FCSTD DOCUMENT  (FreeCAD 0.20R29410 (Git))
Label: trafficModuleV3-1
License: All rights reserved
LicenseURL: http://en.wikipedia.org/wiki/All_rights_reserved
objects: Part::Feature×180, Sketcher::SketchObject×122, Part::Extrusion×62, Part::MultiFuse×53, Part::MultiCommon×31, Part::Loft×30, Part::Cylinder×26, Part::Cut×23, Part::Fillet×23, App::Part×13, Part::Box×11, Part::Compound2×2, Part::Cone×1
note: 562 computed .brp shape members not serialized (recipe doc carries the construction recipe); baked Part::Feature solids carry a one-line shape summary decoded from their .brp

FEATURE [Sketcher::SketchObject] Sketch014
  FullyConstrained = true
  sketch-geometry (4):
    g0: LineSegment StartX=0 StartY=275 StartZ=0 EndX=275 EndY=275 EndZ=0
    g1: LineSegment StartX=275 StartY=275 StartZ=0 EndX=275 EndY=0 EndZ=0
    g2: LineSegment StartX=275 StartY=0 StartZ=0 EndX=0 EndY=0 EndZ=0
    g3: LineSegment StartX=0 StartY=0 StartZ=0 EndX=0 EndY=275 EndZ=0
  constraints (11):
    c: Coincident(g0,g1)
    c: Coincident(g1,g2)
    c: Coincident(g2,g3)
    c: Coincident(g3,g0)
    c: Horizontal(g0)
    c: Horizontal(g2)
    c: Vertical(g1)
    c: Vertical(g3)
    c: Coincident(g2,g-1)
    c: DistanceX(g2,g2) = 275
    c: DistanceY(g3,g3) = 275
FEATURE [Sketcher::SketchObject] Sketch015
  FullyConstrained = true
  Placement = pos=(0,0,175.1) rot=(0,0,1;0rad)
  sketch-geometry (5):
    g0: GeomPoint X=137.5 Y=137.5 Z=0
    g1: LineSegment StartX=137.55 StartY=137.55 StartZ=0 EndX=137.55 EndY=137.45 EndZ=0
    g2: LineSegment StartX=137.55 StartY=137.45 StartZ=0 EndX=137.45 EndY=137.45 EndZ=0
    g3: LineSegment StartX=137.45 StartY=137.45 StartZ=0 EndX=137.45 EndY=137.55 EndZ=0
    g4: LineSegment StartX=137.45 StartY=137.55 StartZ=0 EndX=137.55 EndY=137.55 EndZ=0
  constraints (14):
    c: Coincident(g1,g2)
    c: Horizontal(g2)
    c: Vertical(g1)
    c: DistanceX(g2,g2) = 0.1
    c: DistanceX(g2,g0) = 0.05
    c: DistanceY(g1,g1) = 0.1
    c: DistanceY(g1,g0) = -0.05
    c: DistanceX(g0) = 137.5
    c: DistanceY(g0) = 137.5
    c: Coincident(g3,g2)
    c: Vertical(g3)
    c: Coincident(g4,g3)
    c: Coincident(g4,g1)
    c: Horizontal(g4)
FEATURE [Part::Loft] Loft  label="outerLayer"
  Closed = false
  MaxDegree = 5
  Ruled = false
  Sections = -> [Sketch014,Sketch015]
  Solid = true
FEATURE [Part::Feature] Part__Feature025  label="CUI_VGS-35C-12"
  Placement = pos=(86,137.5,21.5) rot=(1,0,0;1.5708rad)
  shape: bbox 82.03 x 100 x 30.06 mm, 2215 faces, 10 solids (baked)
FEATURE [Part::Cylinder] Cylinder004 .. Cylinder009  x6 (patterned run collapsed; names and placements below)
  Angle = 360
  AttacherType = Attacher::AttachEngine3D
  FirstAngle = 0
  Height = 10
  Radius = 2
  SecondAngle = 0
FEATURE [Part::Cylinder] Cylinder010  label="Cylinder"
  Angle = 360
  AttacherType = Attacher::AttachEngine3D
  FirstAngle = 0
  Height = 10
  Radius = 2
  SecondAngle = 0
FEATURE [Part::Cylinder] Cylinder011 .. Cylinder018  x8 (patterned run collapsed; names and placements below)
  Angle = 360
  AttacherType = Attacher::AttachEngine3D
  FirstAngle = 0
  Height = 10
  Radius = 2
  SecondAngle = 0
FEATURE [Part::Feature] Part__Feature  label="MainBoard"
  shape: bbox 50 x 23 x 1.8 mm, 90 faces (baked)
FEATURE [Part::Feature] Part__Feature029  label="USB Type C Port (SMD Type)"
  Placement = pos=(-18.7,0.12,3.4) rot=(0.707107,-0.707107,0;3.14159rad)
  shape: bbox 7.901 x 8.941 x 4.201 mm, 394 faces, 24 solids (baked)
FEATURE [Part::Feature] Part__Feature030  label="LoRaSTM32Chip"
  Placement = pos=(8.97,0,1.8) rot=(0,0,1;0rad)
  shape: bbox 12 x 12 x 2.5 mm, 68 faces (baked)
FEATURE [Part::Feature] Part__Feature031  label="E10_433M_SMA122"
  Placement = pos=(13,-2.15,1.4) rot=(0,0,1;0rad)
  shape: bbox 11.33 x 1.55 x 1.55 mm, 34 faces (baked)
FEATURE [Part::Feature] Part__Feature032  label="E10_433M_SMA123"
  Placement = pos=(13,-2.15,1.4) rot=(0,0,1;0rad)
  shape: bbox 13.33 x 6.493 x 6.493 mm, 59 faces (baked)
FEATURE [Part::Feature] Part__Feature033  label="CP2012"
  Placement = pos=(-8.75,0.13,1.82) rot=(0,0,1;0rad)
  shape: bbox 4 x 4 x 0.7 mm, 6 faces (baked)
FEATURE [Part::Feature] Part__Feature034  label="u.Fl Antenna Connector - 523-A-1JB"
  Placement = pos=(24.2,5.8,1.8) rot=(0,0.707107,0.707107;3.14159rad)
  shape: bbox 3.1 x 3 x 1.25 mm, 82 faces, 5 solids (baked)
FEATURE [Part::Feature] Part__Feature035  label="Top Traces"
  shape: bbox 49.4 x 23 x 0.02 mm, 7906 faces, 207 solids (baked)
FEATURE [App::Part] LoRa_E5_Mini  label="LoRa-E5-Mini"
  Group = -> [Part__Feature,Part__Feature029,Part__Feature030,Part__Feature031,Part__Feature032,Part__Feature033,Part__Feature034,Part__Feature035,Cylinder004,Cylinder005,Cylinder006,Cylinder007,Cylinder008,Cylinder009,Cylinder010,Cylinder011,Cylinder012,Cylinder013,Cylinder014,Cylinder015,Cylinder016,Cylinder017,Cylinder018]
  Origin = -> Origin
  Placement = pos=(100,164,45) rot=(0,0,-1;4.71239rad)
FEATURE [Part::Feature] Part__Feature037  label="ips7100s"
  Placement = pos=(161.5,115,75) rot=(0,0,1;0rad)
  shape: bbox 48.08 x 13.98 x 44.07 mm, 1935 faces (baked)
FEATURE [Part::Cone] Cone
  Angle = 360
  AttacherType = Attacher::AttachEngine3D
  Height = 1.5
  Placement = pos=(0,0,25.5) rot=(0,0,1;0rad)
  Radius1 = 4
  Radius2 = 3.5
FEATURE [Part::Cylinder] Cylinder020
  Angle = 360
  AttacherType = Attacher::AttachEngine3D
  FirstAngle = 0
  Height = 22
  Placement = pos=(0,0,5) rot=(0,0,1;0rad)
  Radius = 3.2
  SecondAngle = 0
FEATURE [Part::Cylinder] Cylinder021
  Angle = 360
  AttacherType = Attacher::AttachEngine3D
  FirstAngle = 0
  Height = 2
  Placement = pos=(0,0,5) rot=(0,0,1;0rad)
  Radius = 3.55
  SecondAngle = 0
FEATURE [Part::Cylinder] Cylinder022
  Angle = 360
  AttacherType = Attacher::AttachEngine3D
  FirstAngle = 0
  Height = 1
  Placement = pos=(0,0,11) rot=(0,0,1;0rad)
  Radius = 3.55
  SecondAngle = 0
FEATURE [Part::Cylinder] Cylinder023
  Angle = 360
  AttacherType = Attacher::AttachEngine3D
  FirstAngle = 0
  Height = 8
  Placement = pos=(0,0,12) rot=(0,0,1;0rad)
  Radius = 3.25
  SecondAngle = 0
FEATURE [Part::Cylinder] Cylinder024
  Angle = 360
  AttacherType = Attacher::AttachEngine3D
  FirstAngle = 0
  Height = 5.5
  Placement = pos=(0,0,20) rot=(0,0,1;0rad)
  Radius = 4
  SecondAngle = 0
FEATURE [Part::Cylinder] Cylinder025
  Angle = 360
  AttacherType = Attacher::AttachEngine3D
  FirstAngle = 0
  Height = 2
  Placement = pos=(0,0,3) rot=(0,0,1;0rad)
  Radius = 1
  SecondAngle = 0
FEATURE [Part::MultiFuse] Fusion002
  Shapes = -> [Cone,Cylinder020,Cylinder021,Cylinder022,Cylinder023,Cylinder024]
FEATURE [Part::MultiFuse] Fusion055  label="mic"
  Placement = pos=(137.5,137.5,108.25) rot=(0,0,1;3.14159rad)
  Shapes = -> [Cylinder025,Fusion002]
FEATURE [Part::Feature] Part__Feature040  label="CeramicBody (1)"
  shape: bbox 1.8 x 1.23 x 1.23 mm, 10 faces (baked)
FEATURE [Part::Feature] Part__Feature126  label="scd30"
  Placement = pos=(137.5,170,95) rot=(1,0,0;3.14159rad)
  shape: bbox 35.11 x 7.027 x 23.02 mm, 2292 faces, 25 solids (baked)
FEATURE [Part::Feature] Part__Feature127  label="Board"
  shape: bbox 25.4 x 25.4 x 1.57 mm, 211 faces (baked)
FEATURE [Part::Feature] Part__Feature128  label="QFN24_4MM"
  Placement = pos=(12.1412,14.4526,1.57) rot=(0,0,1;3.92699rad)
  shape: bbox 5.657 x 5.657 x 0.9 mm, 172 faces (baked)
FEATURE [Part::Feature] Part__Feature129  label="Part 5"
  shape: bbox 0.48 x 0.6603 x 0.6 mm, 14 faces (baked)
FEATURE [Part::Feature] Part__Feature130  label="Part 6"
  shape: bbox 0.48 x 0.6603 x 0.6 mm, 14 faces (baked)
FEATURE [Part::Feature] Part__Feature131  label="Part 4"
  shape: bbox 0.48 x 0.6603 x 0.6 mm, 14 faces (baked)
FEATURE [Part::Feature] Part__Feature132  label="Part 3"
  shape: bbox 0.48 x 0.6603 x 0.6 mm, 14 faces (baked)
FEATURE [Part::Feature] Part__Feature133  label="Part 010"
  shape: bbox 0.48 x 0.6603 x 0.6 mm, 14 faces (baked)
FEATURE [Part::Feature] Part__Feature134  label="Part 011"
  shape: bbox 3 x 1.4 x 1 mm, 10 faces (baked)
FEATURE [Part::Feature] Part__Feature135  label="Pin1"
  shape: bbox 0.6224 x 1.252 x 1.252 mm, 37 faces (baked)
FEATURE [Part::Feature] Part__Feature136  label="Pin2"
  shape: bbox 0.6224 x 1.252 x 1.252 mm, 37 faces (baked)
FEATURE [Part::Feature] Part__Feature137  label="CeramicBody"
  shape: bbox 1.8 x 1.23 x 1.23 mm, 10 faces (baked)
FEATURE [Part::Feature] Part__Feature138  label="0603-NO (1)"
  Placement = pos=(23.241,6.223,1.57) rot=(0,0,1;0rad)
  shape: bbox 1.7 x 0.9 x 0.55 mm, 52 faces, 3 solids (baked)
FEATURE [Part::Feature] Part__Feature139  label="0603-NO (2)"
  Placement = pos=(13.3858,8.4328,1.57) rot=(0,0,1;0rad)
  shape: bbox 1.7 x 0.9 x 0.55 mm, 52 faces, 3 solids (baked)
FEATURE [Part::Feature] Part__Feature140  label="0603-NO (3)"
  Placement = pos=(1.905,18.923,1.57) rot=(0,0,1;3.14159rad)
  shape: bbox 1.7 x 0.9 x 0.55 mm, 52 faces, 3 solids (baked)
FEATURE [Part::Feature] Part__Feature141  label="Pin1 (1)"
  shape: bbox 0.6224 x 1.252 x 1.252 mm, 37 faces (baked)
FEATURE [Part::Feature] Part__Feature142  label="Pin2 (1)"
  shape: bbox 0.6224 x 1.252 x 1.252 mm, 37 faces (baked)
FEATURE [Part::Feature] Part__Feature143  label="Pin1 (2)"
  shape: bbox 0.6224 x 1.252 x 1.252 mm, 37 faces (baked)
FEATURE [Part::Feature] Part__Feature144  label="Pin2 (2)"
  shape: bbox 0.6224 x 1.252 x 1.252 mm, 37 faces (baked)
FEATURE [Part::Feature] Part__Feature145  label="CeramicBody (2)"
  shape: bbox 1.8 x 1.23 x 1.23 mm, 10 faces (baked)
FEATURE [Part::Feature] Part__Feature146  label="CHIPLED_0603_NOOUTLINE"
  Placement = pos=(23.368,8.509,1.57) rot=(0,0,1;1.5708rad)
  shape: bbox 1.616 x 0.8 x 0.4 mm, 133 faces (baked)
FEATURE [Part::Feature] Part__Feature147  label="CHIPLED_0603_NOOUTLINE (1)"
  Placement = pos=(1.905,16.764,1.57) rot=(0,0,-1;1.5708rad)
  shape: bbox 1.616 x 0.8 x 0.4 mm, 133 faces (baked)
FEATURE [Part::Feature] Part__Feature148  label="JST_SH4"
  Placement = pos=(22.86,12.7,1.57) rot=(0,0,1;1.5708rad)
  shape: bbox 4.95 x 6 x 2.96 mm, 229 faces, 7 solids (baked)
FEATURE [Part::Feature] Part__Feature149  label="JST_SH4 (1)"
  Placement = pos=(2.54,12.7,1.57) rot=(0,0,-1;1.5708rad)
  shape: bbox 4.95 x 6 x 2.96 mm, 229 faces, 7 solids (baked)
FEATURE [Part::Feature] Part__Feature150  label="NEO3535_REVERSE"
  Placement = pos=(12.7,23.114,0) rot=(0,1,0;3.14159rad)
  shape: bbox 5.88 x 2.8 x 1.78 mm, 41 faces, 5 solids (baked)
FEATURE [Part::Feature] Part__Feature151  label="RESPACK_4X0603"
  Placement = pos=(22.86,18.415,1.57) rot=(0,0,1;3.14159rad)
  shape: bbox 3.2 x 1.6 x 0.61 mm, 172 faces (baked)
FEATURE [Part::Feature] Part__Feature152  label="SOT363"
  Placement = pos=(17.399,12.192,1.57) rot=(0,0,-1;1.5708rad)
  shape: bbox 2.208 x 2.208 x 1.121 mm, 178 faces, 4 solids (baked)
FEATURE [Part::Feature] Part__Feature153  label="Printed Circuit Board001"
  shape: bbox 25.4 x 17.78 x 1.6 mm, 42 faces (baked)
FEATURE [Part::Feature] Part__Feature154  label="EAHC2835WD007"
  shape: bbox 3.513 x 2.813 x 0.7485 mm, 108 faces, 4 solids (baked)
FEATURE [Part::Feature] Part__Feature155  label="AS7341 v003"
  Placement = pos=(0,-0.339822,1.6) rot=(0,0,1;0rad)
  shape: bbox 2 x 3.1 x 1.1 mm, 267 faces, 26 solids (baked)
FEATURE [Part::Feature] Part__Feature156  label="CAPC-0805-T0.95-BN v004"
  Placement = pos=(-5.01759,-3.15294,1.6) rot=(0,0,1;0rad)
  shape: bbox 2.1 x 1.35 x 0.95 mm, 42 faces (baked)
FEATURE [Part::Feature] Part__Feature157  label="CAPC-0805-T0.95-BN v005"
  Placement = pos=(-5.48627,2.66154,1.6) rot=(0,0,-1;1.5708rad)
  shape: bbox 1.35 x 2.1 x 0.95 mm, 42 faces (baked)
FEATURE [Part::Feature] Part__Feature158  label="CAPC-0805-T0.95-BN v006"
  Placement = pos=(-3.43627,2.66154,1.6) rot=(0,0,-1;1.5708rad)
  shape: bbox 1.35 x 2.1 x 0.95 mm, 42 faces (baked)
FEATURE [Part::Feature] Part__Feature159  label="CAPC-0603-T0.9-BN v002"
  Placement = pos=(-1.69987,-3.28475,1.6) rot=(0,0,1;0rad)
  shape: bbox 1.7 x 0.9 x 0.9 mm, 42 faces (baked)
FEATURE [Part::Feature] Part__Feature160  label="BODY_MF06A001"
  Placement = pos=(0,0,0.762) rot=(0.57735,-0.57735,-0.57735;2.0944rad)
  shape: bbox 1.601 x 2.921 x 1.016 mm, 42 faces (baked)
FEATURE [Part::Feature] Part__Feature161  label="LEAD_MF06A006"
  Placement = pos=(-0.9652,-0.9525,0.1016) rot=(0.57735,-0.57735,-0.57735;2.0944rad)
  shape: bbox 0.6223 x 0.3749 x 0.8636 mm, 14 faces (baked)
FEATURE [Part::Feature] Part__Feature162  label="LEAD_MF06A007"
  Placement = pos=(-0.9652,0,0.1016) rot=(0.57735,-0.57735,-0.57735;2.0944rad)
  shape: bbox 0.6223 x 0.3749 x 0.8636 mm, 14 faces (baked)
FEATURE [Part::Feature] Part__Feature163  label="LEAD_MF06A008"
  Placement = pos=(-0.9652,0.9525,0.1016) rot=(0.57735,-0.57735,-0.57735;2.0944rad)
  shape: bbox 0.6223 x 0.3749 x 0.8636 mm, 14 faces (baked)
FEATURE [Part::Feature] Part__Feature164  label="LEAD_MF06A009"
  Placement = pos=(0.9652,-0.9525,0.1016) rot=(0.57735,0.57735,0.57735;2.0944rad)
  shape: bbox 0.6223 x 0.3749 x 0.8636 mm, 14 faces (baked)
FEATURE [Part::Feature] Part__Feature165  label="LEAD_MF06A010"
  Placement = pos=(0.9652,0,0.1016) rot=(0.57735,0.57735,0.57735;2.0944rad)
  shape: bbox 0.6223 x 0.3749 x 0.8636 mm, 14 faces (baked)
FEATURE [Part::Feature] Part__Feature166  label="LEAD_MF06A011"
  Placement = pos=(0.9652,0.9525,0.1016) rot=(0.57735,0.57735,0.57735;2.0944rad)
  shape: bbox 0.6223 x 0.3749 x 0.8636 mm, 14 faces (baked)
FEATURE [Part::Feature] Part__Feature167  label="SOT363 v003"
  Placement = pos=(4.97054,-0.645171,1.675) rot=(0,0,1;3.14159rad)
  shape: bbox 2.1 x 2 x 1.1 mm, 94 faces, 7 solids (baked)
FEATURE [Part::Feature] Part__Feature168  label="LED 0603 single color v002"
  Placement = pos=(-9.18406,3.72778,1.60762) rot=(0,0,1;1.5708rad)
  shape: bbox 1.961 x 0.7932 x 0.7145 mm, 63 faces, 5 solids (baked)
FEATURE [Part::Feature] Part__Feature169  label="RESC-0603 v003"
  Placement = pos=(4.83432,-3.67461,1.6) rot=(0,0,1;0rad)
  shape: bbox 1.7 x 0.9 x 0.55 mm, 52 faces, 3 solids (baked)
FEATURE [Part::Feature] Part__Feature170  label="RESC-0603 v004"
  Placement = pos=(-7.14949,3.61248,1.6) rot=(0,0,-1;1.5708rad)
  shape: bbox 0.9 x 1.7 x 0.55 mm, 52 faces, 3 solids (baked)
FEATURE [Part::Feature] Part__Feature171  label="YC164_RESPACK v002"
  Placement = pos=(2.99591,1.52916,1.6) rot=(0,0,1;0rad)
  shape: bbox 3.2 x 1.6 x 0.61 mm, 172 faces (baked)
FEATURE [Part::Feature] Part__Feature172  label="qwicc v004"
  Placement = pos=(-10.8364,0.0607456,1.65) rot=(0,0,-1;1.5708rad)
  shape: bbox 4.95 x 6 x 2.96 mm, 229 faces, 7 solids (baked)
FEATURE [Part::Feature] Part__Feature173  label="qwicc v005"
  Placement = pos=(10.8256,0.00556102,1.65) rot=(0,0,1;1.5708rad)
  shape: bbox 4.95 x 6 x 2.96 mm, 229 faces, 7 solids (baked)
FEATURE [App::Part] _603_NO  label="0603-NO"
  Group = -> [Part__Feature135,Part__Feature136,Part__Feature137]
  Origin = -> Origin012
  Placement = pos=(16.51,8.382,1.57) rot=(0,0,1;0rad)
FEATURE [App::Part] _6700497  label="36700497"
  Group = -> [Part__Feature129,Part__Feature130,Part__Feature131,Part__Feature132,Part__Feature133,Part__Feature134]
  Origin = -> Origin010
  Placement = pos=(0,0,0) rot=(0,0,1;3.14159rad)
FEATURE [App::Part] SOT23_5  label="SOT23-5"
  Group = -> [_6700497]
  Origin = -> Origin011
  Placement = pos=(2.54,6.985,1.57) rot=(0,0,1;3.14159rad)
FEATURE [App::Part] _805_NO  label="0805-NO"
  Group = -> [Part__Feature141,Part__Feature142,Part__Feature040]
  Origin = -> Origin013
  Placement = pos=(7.874,13.589,1.57) rot=(0,0,1;1.5708rad)
FEATURE [App::Part] _805_NO__1_  label="0805-NO (1)"
  Group = -> [Part__Feature143,Part__Feature144,Part__Feature145]
  Origin = -> Origin014
  Placement = pos=(12.827,6.223,1.57) rot=(0,0,1;3.14159rad)
FEATURE [App::Part] Packages
  Group = -> [Part__Feature128,SOT23_5,_603_NO,Part__Feature138,Part__Feature139,Part__Feature140,_805_NO,_805_NO__1_,Part__Feature146,Part__Feature147,Part__Feature148,Part__Feature149,Part__Feature150,Part__Feature151,Part__Feature152]
  Origin = -> Origin015
FEATURE [App::Part] Adafruit_I2C_QT_Rotary_Encoder_v2  label="gps"
  Group = -> [Part__Feature127,Packages]
  Origin = -> Origin016
  Placement = pos=(167.5,167.5,74) rot=(0,0,1;0rad)
FEATURE [App::Part] sot_23_6_v003  label="sot-23-6 v003"
  Group = -> [Part__Feature160,Part__Feature161,Part__Feature162,Part__Feature163,Part__Feature164,Part__Feature165,Part__Feature166]
  Origin = -> Origin017
  Placement = pos=(-4.47945,-0.603742,1.69152) rot=(0,0,1;0rad)
FEATURE [App::Part] Adafruit_AS7341_STEMMA_QT_v003  label="bme280"
  Group = -> [Part__Feature153,Part__Feature154,Part__Feature155,Part__Feature156,Part__Feature157,Part__Feature158,Part__Feature159,sot_23_6_v003,Part__Feature167,Part__Feature168,Part__Feature169,Part__Feature170,Part__Feature171,Part__Feature172,Part__Feature173]
  Origin = -> Origin018
  Placement = pos=(170.5,137.5,95) rot=(-0.707107,0,-0.707107;3.14159rad)
FEATURE [Part::Feature] Part__Feature174  label="Printed Circuit Board002"
  shape: bbox 25.4 x 17.78 x 1.6 mm, 42 faces (baked)
FEATURE [Part::Feature] Part__Feature175  label="EAHC2835WD008"
  shape: bbox 3.513 x 2.813 x 0.7485 mm, 108 faces, 4 solids (baked)
FEATURE [Part::Feature] Part__Feature176  label="AS7341 v004"
  Placement = pos=(0,-0.339822,1.6) rot=(0,0,1;0rad)
  shape: bbox 2 x 3.1 x 1.1 mm, 267 faces, 26 solids (baked)
FEATURE [Part::Feature] Part__Feature177  label="CAPC-0805-T0.95-BN v007"
  Placement = pos=(-5.01759,-3.15294,1.6) rot=(0,0,1;0rad)
  shape: bbox 2.1 x 1.35 x 0.95 mm, 42 faces (baked)
FEATURE [Part::Feature] Part__Feature178  label="CAPC-0805-T0.95-BN v008"
  Placement = pos=(-5.48627,2.66154,1.6) rot=(0,0,-1;1.5708rad)
  shape: bbox 1.35 x 2.1 x 0.95 mm, 42 faces (baked)
FEATURE [Part::Feature] Part__Feature179  label="CAPC-0805-T0.95-BN v009"
  Placement = pos=(-3.43627,2.66154,1.6) rot=(0,0,-1;1.5708rad)
  shape: bbox 1.35 x 2.1 x 0.95 mm, 42 faces (baked)
FEATURE [Part::Feature] Part__Feature180  label="CAPC-0603-T0.9-BN v003"
  Placement = pos=(-1.69987,-3.28475,1.6) rot=(0,0,1;0rad)
  shape: bbox 1.7 x 0.9 x 0.9 mm, 42 faces (baked)
FEATURE [Part::Feature] Part__Feature181  label="BODY_MF06A002"
  Placement = pos=(0,0,0.762) rot=(0.57735,-0.57735,-0.57735;2.0944rad)
  shape: bbox 1.601 x 2.921 x 1.016 mm, 42 faces (baked)
FEATURE [Part::Feature] Part__Feature182  label="LEAD_MF06A012"
  Placement = pos=(-0.9652,-0.9525,0.1016) rot=(0.57735,-0.57735,-0.57735;2.0944rad)
  shape: bbox 0.6223 x 0.3749 x 0.8636 mm, 14 faces (baked)
FEATURE [Part::Feature] Part__Feature183  label="LEAD_MF06A013"
  Placement = pos=(-0.9652,0,0.1016) rot=(0.57735,-0.57735,-0.57735;2.0944rad)
  shape: bbox 0.6223 x 0.3749 x 0.8636 mm, 14 faces (baked)
FEATURE [Part::Feature] Part__Feature184  label="LEAD_MF06A014"
  Placement = pos=(-0.9652,0.9525,0.1016) rot=(0.57735,-0.57735,-0.57735;2.0944rad)
  shape: bbox 0.6223 x 0.3749 x 0.8636 mm, 14 faces (baked)
FEATURE [Part::Feature] Part__Feature185  label="LEAD_MF06A015"
  Placement = pos=(0.9652,-0.9525,0.1016) rot=(0.57735,0.57735,0.57735;2.0944rad)
  shape: bbox 0.6223 x 0.3749 x 0.8636 mm, 14 faces (baked)
FEATURE [Part::Feature] Part__Feature186  label="LEAD_MF06A016"
  Placement = pos=(0.9652,0,0.1016) rot=(0.57735,0.57735,0.57735;2.0944rad)
  shape: bbox 0.6223 x 0.3749 x 0.8636 mm, 14 faces (baked)
FEATURE [Part::Feature] Part__Feature187  label="LEAD_MF06A017"
  Placement = pos=(0.9652,0.9525,0.1016) rot=(0.57735,0.57735,0.57735;2.0944rad)
  shape: bbox 0.6223 x 0.3749 x 0.8636 mm, 14 faces (baked)
FEATURE [Part::Feature] Part__Feature188  label="SOT363 v004"
  Placement = pos=(4.97054,-0.645171,1.675) rot=(0,0,1;3.14159rad)
  shape: bbox 2.1 x 2 x 1.1 mm, 94 faces, 7 solids (baked)
FEATURE [Part::Feature] Part__Feature189  label="LED 0603 single color v003"
  Placement = pos=(-9.18406,3.72778,1.60762) rot=(0,0,1;1.5708rad)
  shape: bbox 1.961 x 0.7932 x 0.7145 mm, 63 faces, 5 solids (baked)
FEATURE [Part::Feature] Part__Feature190  label="RESC-0603 v005"
  Placement = pos=(4.83432,-3.67461,1.6) rot=(0,0,1;0rad)
  shape: bbox 1.7 x 0.9 x 0.55 mm, 52 faces, 3 solids (baked)
FEATURE [Part::Feature] Part__Feature191  label="RESC-0603 v006"
  Placement = pos=(-7.14949,3.61248,1.6) rot=(0,0,-1;1.5708rad)
  shape: bbox 0.9 x 1.7 x 0.55 mm, 52 faces, 3 solids (baked)
FEATURE [Part::Feature] Part__Feature192  label="YC164_RESPACK v003"
  Placement = pos=(2.99591,1.52916,1.6) rot=(0,0,1;0rad)
  shape: bbox 3.2 x 1.6 x 0.61 mm, 172 faces (baked)
FEATURE [Part::Feature] Part__Feature193  label="qwicc v006"
  Placement = pos=(-10.8364,0.0607456,1.65) rot=(0,0,-1;1.5708rad)
  shape: bbox 4.95 x 6 x 2.96 mm, 229 faces, 7 solids (baked)
FEATURE [Part::Feature] Part__Feature194  label="qwicc v007"
  Placement = pos=(10.8256,0.00556102,1.65) rot=(0,0,1;1.5708rad)
  shape: bbox 4.95 x 6 x 2.96 mm, 229 faces, 7 solids (baked)
FEATURE [App::Part] sot_23_6_v004  label="sot-23-6 v004"
  Group = -> [Part__Feature181,Part__Feature182,Part__Feature183,Part__Feature184,Part__Feature185,Part__Feature186,Part__Feature187]
  Origin = -> Origin019
  Placement = pos=(-4.47945,-0.603742,1.69152) rot=(0,0,1;0rad)
FEATURE [App::Part] Adafruit_AS7341_STEMMA_QT_v004  label="bme281"
  Group = -> [Part__Feature174,Part__Feature175,Part__Feature176,Part__Feature177,Part__Feature178,Part__Feature179,Part__Feature180,sot_23_6_v004,Part__Feature188,Part__Feature189,Part__Feature190,Part__Feature191,Part__Feature192,Part__Feature193,Part__Feature194]
  Origin = -> Origin020
  Placement = pos=(104.5,137.5,95) rot=(0,1,0;4.71239rad)
FEATURE [Sketcher::SketchObject] Sketch016
  FullyConstrained = true
  sketch-geometry (4):
    g0: LineSegment StartX=0 StartY=275 StartZ=0 EndX=275 EndY=275 EndZ=0
    g1: LineSegment StartX=275 StartY=275 StartZ=0 EndX=275 EndY=0 EndZ=0
    g2: LineSegment StartX=275 StartY=0 StartZ=0 EndX=0 EndY=0 EndZ=0
    g3: LineSegment StartX=0 StartY=0 StartZ=0 EndX=0 EndY=275 EndZ=0
  constraints (11):
    c: Coincident(g0,g1)
    c: Coincident(g1,g2)
    c: Coincident(g2,g3)
    c: Coincident(g3,g0)
    c: Horizontal(g0)
    c: Horizontal(g2)
    c: Vertical(g1)
    c: Vertical(g3)
    c: Coincident(g2,g-1)
    c: DistanceX(g2,g2) = 275
    c: DistanceY(g3,g3) = 275
FEATURE [Sketcher::SketchObject] Sketch017
  FullyConstrained = true
  Placement = pos=(0,0,175.1) rot=(0,0,1;0rad)
  sketch-geometry (5):
    g0: GeomPoint X=137.5 Y=137.5 Z=0
    g1: LineSegment StartX=137.55 StartY=137.55 StartZ=0 EndX=137.55 EndY=137.45 EndZ=0
    g2: LineSegment StartX=137.55 StartY=137.45 StartZ=0 EndX=137.45 EndY=137.45 EndZ=0
    g3: LineSegment StartX=137.45 StartY=137.45 StartZ=0 EndX=137.45 EndY=137.55 EndZ=0
    g4: LineSegment StartX=137.45 StartY=137.55 StartZ=0 EndX=137.55 EndY=137.55 EndZ=0
  constraints (14):
    c: Coincident(g1,g2)
    c: Horizontal(g2)
    c: Vertical(g1)
    c: DistanceX(g2,g2) = 0.1
    c: DistanceX(g2,g0) = 0.05
    c: DistanceY(g1,g1) = 0.1
    c: DistanceY(g1,g0) = -0.05
    c: DistanceX(g0) = 137.5
    c: DistanceY(g0) = 137.5
    c: Coincident(g3,g2)
    c: Vertical(g3)
    c: Coincident(g4,g3)
    c: Coincident(g4,g1)
    c: Horizontal(g4)
FEATURE [Part::Loft] Loft001  label="outerLayer001"
  Closed = false
  MaxDegree = 5
  Ruled = false
  Sections = -> [Sketch016,Sketch017]
  Solid = true
FEATURE [Sketcher::SketchObject] Sketch018
  FullyConstrained = true
  sketch-geometry (4):
    g0: LineSegment StartX=0 StartY=275 StartZ=0 EndX=275 EndY=275 EndZ=0
    g1: LineSegment StartX=275 StartY=275 StartZ=0 EndX=275 EndY=0 EndZ=0
    g2: LineSegment StartX=275 StartY=0 StartZ=0 EndX=0 EndY=0 EndZ=0
    g3: LineSegment StartX=0 StartY=0 StartZ=0 EndX=0 EndY=275 EndZ=0
  constraints (11):
    c: Coincident(g0,g1)
    c: Coincident(g1,g2)
    c: Coincident(g2,g3)
    c: Coincident(g3,g0)
    c: Horizontal(g0)
    c: Horizontal(g2)
    c: Vertical(g1)
    c: Vertical(g3)
    c: Coincident(g2,g-1)
    c: DistanceX(g2,g2) = 275
    c: DistanceY(g3,g3) = 275
FEATURE [Sketcher::SketchObject] Sketch019
  FullyConstrained = true
  Placement = pos=(0,0,175.1) rot=(0,0,1;0rad)
  sketch-geometry (5):
    g0: GeomPoint X=137.5 Y=137.5 Z=0
    g1: LineSegment StartX=137.55 StartY=137.55 StartZ=0 EndX=137.55 EndY=137.45 EndZ=0
    g2: LineSegment StartX=137.55 StartY=137.45 StartZ=0 EndX=137.45 EndY=137.45 EndZ=0
    g3: LineSegment StartX=137.45 StartY=137.45 StartZ=0 EndX=137.45 EndY=137.55 EndZ=0
    g4: LineSegment StartX=137.45 StartY=137.55 StartZ=0 EndX=137.55 EndY=137.55 EndZ=0
  constraints (14):
    c: Coincident(g1,g2)
    c: Horizontal(g2)
    c: Vertical(g1)
    c: DistanceX(g2,g2) = 0.1
    c: DistanceX(g2,g0) = 0.05
    c: DistanceY(g1,g1) = 0.1
    c: DistanceY(g1,g0) = -0.05
    c: DistanceX(g0) = 137.5
    c: DistanceY(g0) = 137.5
    c: Coincident(g3,g2)
    c: Vertical(g3)
    c: Coincident(g4,g3)
    c: Coincident(g4,g1)
    c: Horizontal(g4)
FEATURE [Part::Loft] Loft002  label="outerLayer002"
  Closed = false
  MaxDegree = 5
  Placement = pos=(0,0,-8) rot=(0,0,1;0rad)
  Ruled = false
  Sections = -> [Sketch018,Sketch019]
  Solid = true
FEATURE [Part::Cut] Cut  label="Shell-Ref"
  Base = -> Loft001
  Tool = -> Loft002
FEATURE [Sketcher::SketchObject] Sketch020
  FullyConstrained = true
  sketch-geometry (4):
    g0: LineSegment StartX=0 StartY=275 StartZ=0 EndX=275 EndY=275 EndZ=0
    g1: LineSegment StartX=275 StartY=275 StartZ=0 EndX=275 EndY=0 EndZ=0
    g2: LineSegment StartX=275 StartY=0 StartZ=0 EndX=0 EndY=0 EndZ=0
    g3: LineSegment StartX=0 StartY=0 StartZ=0 EndX=0 EndY=275 EndZ=0
  constraints (11):
    c: Coincident(g0,g1)
    c: Coincident(g1,g2)
    c: Coincident(g2,g3)
    c: Coincident(g3,g0)
    c: Horizontal(g0)
    c: Horizontal(g2)
    c: Vertical(g1)
    c: Vertical(g3)
    c: Coincident(g2,g-1)
    c: DistanceX(g2,g2) = 275
    c: DistanceY(g3,g3) = 275
FEATURE [Part::Extrusion] Extrude  label="level01s"
  Base = -> Sketch020
  Dir = (0,0,1)
  DirMode = 2
  FaceMakerClass = Part::FaceMakerBullseye
  LengthFwd = 10
  LengthRev = 0
  Placement = pos=(0,0,64) rot=(0,0,1;0rad)
  Solid = true
  Symmetric = false
FEATURE [Sketcher::SketchObject] Sketch021
  FullyConstrained = true
  sketch-geometry (4):
    g0: LineSegment StartX=0 StartY=275 StartZ=0 EndX=275 EndY=275 EndZ=0
    g1: LineSegment StartX=275 StartY=275 StartZ=0 EndX=275 EndY=0 EndZ=0
    g2: LineSegment StartX=275 StartY=0 StartZ=0 EndX=0 EndY=0 EndZ=0
    g3: LineSegment StartX=0 StartY=0 StartZ=0 EndX=0 EndY=275 EndZ=0
  constraints (11):
    c: Coincident(g0,g1)
    c: Coincident(g1,g2)
    c: Coincident(g2,g3)
    c: Coincident(g3,g0)
    c: Horizontal(g0)
    c: Horizontal(g2)
    c: Vertical(g1)
    c: Vertical(g3)
    c: Coincident(g2,g-1)
    c: DistanceX(g2,g2) = 275
    c: DistanceY(g3,g3) = 275
FEATURE [Sketcher::SketchObject] Sketch022
  FullyConstrained = true
  Placement = pos=(0,0,175.1) rot=(0,0,1;0rad)
  sketch-geometry (5):
    g0: GeomPoint X=137.5 Y=137.5 Z=0
    g1: LineSegment StartX=137.55 StartY=137.55 StartZ=0 EndX=137.55 EndY=137.45 EndZ=0
    g2: LineSegment StartX=137.55 StartY=137.45 StartZ=0 EndX=137.45 EndY=137.45 EndZ=0
    g3: LineSegment StartX=137.45 StartY=137.45 StartZ=0 EndX=137.45 EndY=137.55 EndZ=0
    g4: LineSegment StartX=137.45 StartY=137.55 StartZ=0 EndX=137.55 EndY=137.55 EndZ=0
  constraints (14):
    c: Coincident(g1,g2)
    c: Horizontal(g2)
    c: Vertical(g1)
    c: DistanceX(g2,g2) = 0.1
    c: DistanceX(g2,g0) = 0.05
    c: DistanceY(g1,g1) = 0.1
    c: DistanceY(g1,g0) = -0.05
    c: DistanceX(g0) = 137.5
    c: DistanceY(g0) = 137.5
    c: Coincident(g3,g2)
    c: Vertical(g3)
    c: Coincident(g4,g3)
    c: Coincident(g4,g1)
    c: Horizontal(g4)
FEATURE [Part::Loft] Loft003  label="outerLayer003"
  Closed = false
  MaxDegree = 5
  Placement = pos=(0,0,-8.25) rot=(0,0,1;0rad)
  Ruled = false
  Sections = -> [Sketch021,Sketch022]
  Solid = true
FEATURE [Part::MultiCommon] Common  label="level1"
  Shapes = -> [Extrude,Loft003]
FEATURE [Sketcher::SketchObject] Sketch
  FullyConstrained = true
  sketch-geometry (5):
    g0: Circle CenterX=75 CenterY=200 CenterZ=0 NormalX=0 NormalY=0 NormalZ=1 AngleXU=0 Radius=7.5
    g1: Circle CenterX=125 CenterY=200 CenterZ=0 NormalX=0 NormalY=0 NormalZ=1 AngleXU=0 Radius=7.5
    g2: Circle CenterX=75 CenterY=75 CenterZ=0 NormalX=0 NormalY=0 NormalZ=1 AngleXU=0 Radius=7.5
    g3: Circle CenterX=200 CenterY=200 CenterZ=0 NormalX=0 NormalY=0 NormalZ=1 AngleXU=0 Radius=7.5
    g4: Circle CenterX=125 CenterY=75 CenterZ=0 NormalX=0 NormalY=0 NormalZ=1 AngleXU=0 Radius=7.5
  constraints (15):
    c: Equal(g0,g1)
    c: Equal(g0,g2)
    c: Diameter(g0) = 15
    c: DistanceX(g2) = 75
    c: DistanceY(g2) = 75
    c: DistanceX(g2,g0) = 0
    c: DistanceY(g0) = 200
    c: DistanceY(g1,g0) = 0
    c: DistanceX(g0,g1) = 50
    c: DistanceX(g3) = 200
    c: Horizontal(g3,g1)
    c: Equal(g3,g1)
    c: Equal(g1,g4)
    c: Horizontal(g4,g2)
    c: Vertical(g1,g4)
FEATURE [Part::Extrusion] Extrude001
  Base = -> Sketch
  Dir = (0,0,1)
  DirMode = 2
  FaceMakerClass = Part::FaceMakerBullseye
  LengthFwd = 63.75
  LengthRev = 0
  Solid = true
  Symmetric = false
FEATURE [Sketcher::SketchObject] Sketch023
  FullyConstrained = true
  sketch-geometry (4):
    g0: LineSegment StartX=0 StartY=275 StartZ=0 EndX=275 EndY=275 EndZ=0
    g1: LineSegment StartX=275 StartY=275 StartZ=0 EndX=275 EndY=0 EndZ=0
    g2: LineSegment StartX=275 StartY=0 StartZ=0 EndX=0 EndY=0 EndZ=0
    g3: LineSegment StartX=0 StartY=0 StartZ=0 EndX=0 EndY=275 EndZ=0
  constraints (11):
    c: Coincident(g0,g1)
    c: Coincident(g1,g2)
    c: Coincident(g2,g3)
    c: Coincident(g3,g0)
    c: Horizontal(g0)
    c: Horizontal(g2)
    c: Vertical(g1)
    c: Vertical(g3)
    c: Coincident(g2,g-1)
    c: DistanceX(g2,g2) = 275
    c: DistanceY(g3,g3) = 275
FEATURE [Sketcher::SketchObject] Sketch024
  FullyConstrained = true
  Placement = pos=(0,0,175.1) rot=(0,0,1;0rad)
  sketch-geometry (5):
    g0: GeomPoint X=137.5 Y=137.5 Z=0
    g1: LineSegment StartX=137.55 StartY=137.55 StartZ=0 EndX=137.55 EndY=137.45 EndZ=0
    g2: LineSegment StartX=137.55 StartY=137.45 StartZ=0 EndX=137.45 EndY=137.45 EndZ=0
    g3: LineSegment StartX=137.45 StartY=137.45 StartZ=0 EndX=137.45 EndY=137.55 EndZ=0
    g4: LineSegment StartX=137.45 StartY=137.55 StartZ=0 EndX=137.55 EndY=137.55 EndZ=0
  constraints (14):
    c: Coincident(g1,g2)
    c: Horizontal(g2)
    c: Vertical(g1)
    c: DistanceX(g2,g2) = 0.1
    c: DistanceX(g2,g0) = 0.05
    c: DistanceY(g1,g1) = 0.1
    c: DistanceY(g1,g0) = -0.05
    c: DistanceX(g0) = 137.5
    c: DistanceY(g0) = 137.5
    c: Coincident(g3,g2)
    c: Vertical(g3)
    c: Coincident(g4,g3)
    c: Coincident(g4,g1)
    c: Horizontal(g4)
FEATURE [Part::Loft] Loft004  label="outerLayer004"
  Closed = false
  MaxDegree = 5
  Placement = pos=(0,0,-8.25) rot=(0,0,1;0rad)
  Ruled = false
  Sections = -> [Sketch023,Sketch024]
  Solid = true
FEATURE [Sketcher::SketchObject] Sketch025
  FullyConstrained = true
  sketch-geometry (4):
    g0: LineSegment StartX=0 StartY=275 StartZ=0 EndX=275 EndY=275 EndZ=0
    g1: LineSegment StartX=275 StartY=275 StartZ=0 EndX=275 EndY=0 EndZ=0
    g2: LineSegment StartX=275 StartY=0 StartZ=0 EndX=0 EndY=0 EndZ=0
    g3: LineSegment StartX=0 StartY=0 StartZ=0 EndX=0 EndY=275 EndZ=0
  constraints (11):
    c: Coincident(g0,g1)
    c: Coincident(g1,g2)
    c: Coincident(g2,g3)
    c: Coincident(g3,g0)
    c: Horizontal(g0)
    c: Horizontal(g2)
    c: Vertical(g1)
    c: Vertical(g3)
    c: Coincident(g2,g-1)
    c: DistanceX(g2,g2) = 275
    c: DistanceY(g3,g3) = 275
FEATURE [Part::Extrusion] Extrude002  label="level01s001"
  Base = -> Sketch025
  Dir = (0,0,1)
  DirMode = 2
  FaceMakerClass = Part::FaceMakerBullseye
  LengthFwd = 5
  LengthRev = 0
  Solid = true
  Symmetric = false
FEATURE [Part::MultiCommon] Common001  label="BaseLevel"
  Shapes = -> [Loft004,Extrude002]
FEATURE [Part::MultiFuse] Fusion  label="level2"
  Shapes = -> [Extrude001,Common001]
FEATURE [Sketcher::SketchObject] Sketch026
  FullyConstrained = true
  Placement = pos=(0,0,0) rot=(1,0,0;1.5708rad)
  sketch-geometry (6):
    g0: LineSegment StartX=46 StartY=5 StartZ=0 EndX=40 EndY=5 EndZ=0
    g1: LineSegment StartX=40 StartY=5 StartZ=0 EndX=40 EndY=41.5 EndZ=0
    g2: LineSegment StartX=40 StartY=41.5 StartZ=0 EndX=115 EndY=41.5 EndZ=0
    g3: LineSegment StartX=115 StartY=41.5 StartZ=0 EndX=115 EndY=35.5 EndZ=0
    g4: LineSegment StartX=115 StartY=35.5 StartZ=0 EndX=46 EndY=35.5 EndZ=0
    g5: LineSegment StartX=46 StartY=35.5 StartZ=0 EndX=46 EndY=5 EndZ=0
  constraints (18):
    c: Horizontal(g0)
    c: Coincident(g1,g0)
    c: Vertical(g1)
    c: Coincident(g2,g1)
    c: Horizontal(g2)
    c: Coincident(g3,g2)
    c: Coincident(g4,g3)
    c: Horizontal(g4)
    c: Coincident(g5,g4)
    c: Coincident(g5,g0)
    c: Vertical(g5)
    c: Vertical(g3)
    c: DistanceY(g0) = 5
    c: DistanceY(g3,g3) = 6
    c: DistanceX(g0,g0) = 6
    c: DistanceX(g1) = 40
    c: DistanceX(g2) = 115
    c: DistanceY(g4) = 35.5
FEATURE [Part::Extrusion] Extrude003
  Base = -> Sketch026
  Dir = (0,-1,2e-16)
  DirMode = 2
  FaceMakerClass = Part::FaceMakerBullseye
  LengthFwd = 45
  LengthRev = 0
  Placement = pos=(0,190,0) rot=(0,0,1;0rad)
  Solid = true
  Symmetric = false
FEATURE [Part::MultiFuse] Fusion056  label="level2s"
  Shapes = -> [Fusion,Extrude003]
FEATURE [Sketcher::SketchObject] Sketch027
  FullyConstrained = true
  sketch-geometry (21):
    g0: Circle CenterX=51.75 CenterY=92.5 CenterZ=0 NormalX=0 NormalY=0 NormalZ=1 AngleXU=0 Radius=1.625
    g1: Circle CenterX=87.75 CenterY=108.5 CenterZ=0 NormalX=0 NormalY=0 NormalZ=1 AngleXU=0 Radius=1.625
    g2: Circle CenterX=121.75 CenterY=185.5 CenterZ=0 NormalX=0 NormalY=0 NormalZ=1 AngleXU=0 Radius=2
    g3: Circle CenterX=147.3 CenterY=147.75 CenterZ=0 NormalX=0 NormalY=0 NormalZ=1 AngleXU=0 Radius=1.625
    g4: Circle CenterX=218.8 CenterY=147.75 CenterZ=0 NormalX=0 NormalY=0 NormalZ=1 AngleXU=0 Radius=1.625
    g5: Circle CenterX=218.8 CenterY=219.25 CenterZ=0 NormalX=0 NormalY=0 NormalZ=1 AngleXU=0 Radius=1.625
    g6: Circle CenterX=147.3 CenterY=219.25 CenterZ=0 NormalX=0 NormalY=0 NormalZ=1 AngleXU=0 Radius=1.625
    g7: Circle CenterX=75 CenterY=200 CenterZ=0 NormalX=0 NormalY=0 NormalZ=1 AngleXU=0 Radius=2.8
    g8: Circle CenterX=125 CenterY=200 CenterZ=0 NormalX=0 NormalY=0 NormalZ=1 AngleXU=0 Radius=2.8
    g9: Circle CenterX=200 CenterY=75 CenterZ=0 NormalX=0 NormalY=0 NormalZ=1 AngleXU=0 Radius=2.8
    g10: Circle CenterX=75 CenterY=75 CenterZ=0 NormalX=0 NormalY=0 NormalZ=1 AngleXU=0 Radius=2.8
    g11: Circle CenterX=91 CenterY=186.5 CenterZ=0 NormalX=0 NormalY=0 NormalZ=1 AngleXU=0 Radius=1.65
    g12: Circle CenterX=109 CenterY=186.5 CenterZ=0 NormalX=0 NormalY=0 NormalZ=1 AngleXU=0 Radius=1.65
    g13: Circle CenterX=91 CenterY=151.5 CenterZ=0 NormalX=0 NormalY=0 NormalZ=1 AngleXU=0 Radius=1.65
    g14: Circle CenterX=109 CenterY=151.5 CenterZ=0 NormalX=0 NormalY=0 NormalZ=1 AngleXU=0 Radius=1.65
    g15: Circle CenterX=147.3 CenterY=128.25 CenterZ=0 NormalX=0 NormalY=0 NormalZ=1 AngleXU=0 Radius=1.625
    g16: Circle CenterX=218.8 CenterY=128.25 CenterZ=0 NormalX=0 NormalY=0 NormalZ=1 AngleXU=0 Radius=1.625
    g17: Circle CenterX=147.3 CenterY=56.75 CenterZ=0 NormalX=0 NormalY=0 NormalZ=1 AngleXU=0 Radius=1.625
    g18: Circle CenterX=218.8 CenterY=56.75 CenterZ=0 NormalX=0 NormalY=0 NormalZ=1 AngleXU=0 Radius=1.625
    g19: Circle CenterX=125 CenterY=75 CenterZ=0 NormalX=0 NormalY=0 NormalZ=1 AngleXU=0 Radius=2.8
    g20: Circle CenterX=200 CenterY=200 CenterZ=0 NormalX=0 NormalY=0 NormalZ=1 AngleXU=0 Radius=2.8
  constraints (60):
    c: Equal(g0,g1)
    c: Equal(g0, g3-g6) x4
    c: Diameter(g0) = 3.25
    c: DistanceX(g0) = 51.75
    c: DistanceY(g0) = 92.5
    c: DistanceY(g0,g1) = 16
    c: DistanceX(g0,g1) = 36
    c: DistanceY(g1,g2) = 77
    c: DistanceX(g1,g2) = 34
    c: Diameter(g2) = 4
    c: DistanceY(g3) = 147.75
    c: DistanceX(g3) = 147.3
    c: DistanceX(g3,g4) = 71.5
    c: DistanceY(g4,g3) = 0
    c: DistanceX(g3,g6) = 0
    c: DistanceY(g3,g6) = 71.5
    c: DistanceY(g6,g5) = 0
    c: DistanceX(g4,g5) = 0
    c: DistanceY(g10) = 75
    c: DistanceY(g10,g9) = 0
    c: DistanceX(g10) = 75
    c: DistanceX(g10,g9) = 125
    c: DistanceY(g10,g7) = 125
    c: DistanceX(g7,g10) = 0
    c: DistanceX(g7,g8) = 50
    c: DistanceY(g8,g7) = 0
    c: Equal(g7,g8)
    c: Equal(g7,g10)
    c: Equal(g7,g9)
    c: Diameter(g7) = 5.6
    c: Equal(g11,g12)
    c: Equal(g11,g13)
    c: Equal(g11,g14)
    c: Diameter(g11) = 3.3
    c: DistanceY(g13) = 151.5
    c: DistanceX(g13) = 91
    c: DistanceY(g14,g13) = 0
    c: DistanceX(g13,g14) = 18
    c: DistanceY(g13,g11) = 35
    c: DistanceX(g13,g11) = 0
    c: DistanceY(g11,g12) = 0
    c: DistanceX(g12,g14) = 0
    c: Equal(g16,g15)
    c: Equal(g16,g17)
    c: Equal(g16,g18)
    c: Diameter(g16) = 3.25
    c: Vertical(g15,g17)
    c: Vertical(g17,g3)
    c: Vertical(g18,g16)
    c: Vertical(g16,g4)
    c: Horizontal(g15,g16)
    c: Horizontal(g18,g17)
    c: DistanceY(g15,g3) = 19.5
    c: DistanceY(g17,g15) = 71.5
    c: Horizontal(g19,g10)
    c: Vertical(g19,g8)
    c: Equal(g19,g10)
    c: Horizontal(g8,g20)
    c: Vertical(g9,g20)
    c: Equal(g20,g8)
FEATURE [Part::Extrusion] Extrude004
  Base = -> Sketch027
  Dir = (0,0,1)
  DirMode = 2
  FaceMakerClass = Part::FaceMakerBullseye
  LengthFwd = 80
  LengthRev = 0
  Solid = true
  Symmetric = false
FEATURE [Part::Cut] Cut001  label="level02"
  Base = -> Fusion056
  Tool = -> Extrude004
FEATURE [Sketcher::SketchObject] Sketch029
  FullyConstrained = true
  Placement = pos=(0,0,0) rot=(1,0,0;1.5708rad)
  sketch-geometry (8):
    g0: LineSegment StartX=105 StartY=74 StartZ=0 EndX=111 EndY=74 EndZ=0
    g1: LineSegment StartX=164 StartY=115.5 StartZ=0 EndX=164 EndY=74 EndZ=0
    g2: LineSegment StartX=164 StartY=74 StartZ=0 EndX=170 EndY=74 EndZ=0
    g3: LineSegment StartX=170 StartY=74 StartZ=0 EndX=170 EndY=119 EndZ=0
    g4: LineSegment StartX=170 StartY=119 StartZ=0 EndX=105 EndY=119 EndZ=0
    g5: LineSegment StartX=105 StartY=119 StartZ=0 EndX=105 EndY=74 EndZ=0
    g6: LineSegment StartX=111 StartY=74 StartZ=0 EndX=111 EndY=115.5 EndZ=0
    g7: LineSegment StartX=111 StartY=115.5 StartZ=0 EndX=164 EndY=115.5 EndZ=0
  constraints (24):
    c: Horizontal(g0)
    c: Vertical(g1)
    c: Horizontal(g2)
    c: Vertical(g3)
    c: Coincident(g4,g3)
    c: Horizontal(g4)
    c: Coincident(g5,g4)
    c: Coincident(g5,g0)
    c: Vertical(g5)
    c: Coincident(g1,g2)
    c: Coincident(g2,g3)
    c: DistanceY(g0,g1) = 0
    c: DistanceY(g0) = 74
    c: DistanceX(g0) = 105
    c: DistanceX(g1,g2) = 6
    c: DistanceX(g2) = 170
    c: Vertical(g6)
    c: Coincident(g7,g6)
    c: Horizontal(g7)
    c: Coincident(g1,g7)
    c: DistanceY(g1,g3) = 3.5
    c: DistanceX(g4,g6) = 6
    c: Coincident(g0,g6)
    c: DistanceY(g0,g6) = 41.5
FEATURE [Part::Extrusion] Extrude005
  Base = -> Sketch029
  Dir = (0,-1,-6e-16)
  DirMode = 2
  FaceMakerClass = Part::FaceMakerBullseye
  LengthFwd = 20
  LengthRev = 0
  Placement = pos=(0,127.5,0) rot=(0,0,1;0rad)
  Reversed = true
  Solid = true
  Symmetric = false
FEATURE [Sketcher::SketchObject] Sketch030
  FullyConstrained = true
  Placement = pos=(0,0,0) rot=(1,0,0;1.5708rad)
  sketch-geometry (10):
    g0: LineSegment StartX=112 StartY=84 StartZ=0 EndX=122 EndY=84 EndZ=0
    g1: LineSegment StartX=122 StartY=84 StartZ=0 EndX=122 EndY=74 EndZ=0
    g2: LineSegment StartX=122 StartY=74 StartZ=0 EndX=112 EndY=74 EndZ=0
    g3: LineSegment StartX=112 StartY=74 StartZ=0 EndX=112 EndY=84 EndZ=0
    g4: LineSegment StartX=153 StartY=120 StartZ=0 EndX=163 EndY=120 EndZ=0
    g5: LineSegment StartX=163 StartY=120 StartZ=0 EndX=163 EndY=74 EndZ=0
    g6: LineSegment StartX=163 StartY=74 StartZ=0 EndX=153 EndY=74 EndZ=0
    g7: LineSegment StartX=153 StartY=74 StartZ=0 EndX=153 EndY=120 EndZ=0
    g8: Circle CenterX=117.1 CenterY=78.6 CenterZ=0 NormalX=0 NormalY=0 NormalZ=1 AngleXU=0 Radius=1.6
    g9: Circle CenterX=157.85 CenterY=115.4 CenterZ=0 NormalX=0 NormalY=0 NormalZ=1 AngleXU=0 Radius=1.6
  constraints (30):
    c: Coincident(g0,g1)
    c: Coincident(g1,g2)
    c: Coincident(g2,g3)
    c: Coincident(g3,g0)
    c: Horizontal(g0)
    c: Horizontal(g2)
    c: Vertical(g1)
    c: Vertical(g3)
    c: Coincident(g4,g5)
    c: Coincident(g5,g6)
    c: Coincident(g6,g7)
    c: Coincident(g7,g4)
    c: Horizontal(g4)
    c: Horizontal(g6)
    c: Vertical(g5)
    c: Vertical(g7)
    c: DistanceX(g2) = 112
    c: DistanceY(g2,g0) = 10
    c: DistanceX(g2,g0) = 10
    c: DistanceY(g2) = 74
    c: DistanceY(g1,g6) = 0
    c: DistanceX(g1,g6) = 31
    c: DistanceX(g4,g4) = 10
    c: DistanceY(g6,g4) = 46
    c: Equal(g8,g9)
    c: Diameter(g8) = 3.2
    c: DistanceY(g2,g8) = 4.6
    c: DistanceX(g2,g8) = 5.1
    c: DistanceX(g8,g9) = 40.75
    c: DistanceY(g8,g9) = 36.8
FEATURE [Part::Extrusion] Extrude006
  Base = -> Sketch030
  Dir = (0,-1,-6e-16)
  DirMode = 2
  FaceMakerClass = Part::FaceMakerBullseye
  LengthFwd = 10
  LengthRev = 0
  Placement = pos=(0,115.25,0) rot=(0,0,1;0rad)
  Reversed = true
  Solid = true
  Symmetric = false
FEATURE [Sketcher::SketchObject] Sketch031
  FullyConstrained = true
  Placement = pos=(0,0,0) rot=(1,0,0;1.5708rad)
  sketch-geometry (10):
    g0: LineSegment StartX=118 StartY=109 StartZ=0 EndX=128 EndY=109 EndZ=0
    g1: LineSegment StartX=128 StartY=109 StartZ=0 EndX=128 EndY=74 EndZ=0
    g2: LineSegment StartX=128 StartY=74 StartZ=0 EndX=118 EndY=74 EndZ=0
    g3: LineSegment StartX=118 StartY=74 StartZ=0 EndX=118 EndY=109 EndZ=0
    g4: LineSegment StartX=150 StartY=92 StartZ=0 EndX=160 EndY=92 EndZ=0
    g5: LineSegment StartX=160 StartY=92 StartZ=0 EndX=160 EndY=74 EndZ=0
    g6: LineSegment StartX=160 StartY=74 StartZ=0 EndX=150 EndY=74 EndZ=0
    g7: LineSegment StartX=150 StartY=74 StartZ=0 EndX=150 EndY=92 EndZ=0
    g8: Circle CenterX=122.95 CenterY=104.43 CenterZ=0 NormalX=0 NormalY=0 NormalZ=1 AngleXU=0 Radius=1.6
    g9: Circle CenterX=154.95 CenterY=88.19 CenterZ=0 NormalX=0 NormalY=0 NormalZ=1 AngleXU=0 Radius=1.6
  constraints (30):
    c: Coincident(g0,g1)
    c: Coincident(g1,g2)
    c: Coincident(g2,g3)
    c: Coincident(g3,g0)
    c: Horizontal(g0)
    c: Horizontal(g2)
    c: Vertical(g1)
    c: Vertical(g3)
    c: Coincident(g4,g5)
    c: Coincident(g5,g6)
    c: Coincident(g6,g7)
    c: Coincident(g7,g4)
    c: Horizontal(g4)
    c: Horizontal(g6)
    c: Vertical(g5)
    c: Vertical(g7)
    c: DistanceY(g2) = 74
    c: DistanceY(g2,g0) = 35
    c: DistanceX(g2,g2) = 10
    c: DistanceX(g2) = 118
    c: DistanceX(g1,g6) = 22
    c: DistanceX(g4,g4) = 10
    c: DistanceY(g6,g4) = 18
    c: DistanceY(g1,g6) = 0
    c: DistanceX(g2,g8) = 4.95
    c: DistanceY(g2,g8) = 30.43
    c: DistanceX(g8,g9) = 32
    c: DistanceY(g9,g8) = 16.24
    c: Equal(g8,g9)
    c: Diameter(g8) = 3.2
FEATURE [Part::Extrusion] Extrude007
  Base = -> Sketch031
  Dir = (0,-1,-3e-16)
  DirMode = 2
  FaceMakerClass = Part::FaceMakerBullseye
  LengthFwd = 10
  LengthRev = 0
  Placement = pos=(0,162.5,0) rot=(0,0,1;0rad)
  Solid = true
  Symmetric = false
FEATURE [Part::MultiFuse] Fusion057  label="levell1s"
  Shapes = -> [Extrude005,Extrude006,Extrude007,Common]
FEATURE [Sketcher::SketchObject] Sketch032
  FullyConstrained = true
  MapMode = 2
  Support = -> [Fusion057]
  sketch-geometry (17):
    g0: ArcOfCircle CenterX=137.5 CenterY=137.5 CenterZ=0 NormalX=0 NormalY=0 NormalZ=1 AngleXU=0 Radius=3.2 StartAngle=3.14159 EndAngle=6.28319
    g1: LineSegment StartX=134.3 StartY=137.5 StartZ=0 EndX=134.3 EndY=147.5 EndZ=0
    g2: LineSegment StartX=134.3 StartY=147.5 StartZ=0 EndX=140.7 EndY=147.5 EndZ=0
    g3: LineSegment StartX=140.7 StartY=147.5 StartZ=0 EndX=140.7 EndY=137.5 EndZ=0
    g4: Circle CenterX=75 CenterY=75 CenterZ=0 NormalX=0 NormalY=0 NormalZ=1 AngleXU=0 Radius=2.125
    g5: Circle CenterX=200 CenterY=75 CenterZ=0 NormalX=0 NormalY=0 NormalZ=1 AngleXU=0 Radius=2.125
    g6: Circle CenterX=75 CenterY=200 CenterZ=0 NormalX=0 NormalY=0 NormalZ=1 AngleXU=0 Radius=2.125
    g7: Circle CenterX=125 CenterY=200 CenterZ=0 NormalX=0 NormalY=0 NormalZ=1 AngleXU=0 Radius=2.125
    g8: Circle CenterX=200 CenterY=200 CenterZ=0 NormalX=0 NormalY=0 NormalZ=1 AngleXU=0 Radius=2.125
    g9: Circle CenterX=170.05 CenterY=190.35 CenterZ=0 NormalX=0 NormalY=0 NormalZ=1 AngleXU=0 Radius=1.6
    g10: Circle CenterX=190.35 CenterY=190.35 CenterZ=0 NormalX=0 NormalY=0 NormalZ=1 AngleXU=0 Radius=1.6
    g11: Circle CenterX=190.4 CenterY=170.05 CenterZ=0 NormalX=0 NormalY=0 NormalZ=1 AngleXU=0 Radius=1.6
    g12: Circle CenterX=170.05 CenterY=170.05 CenterZ=0 NormalX=0 NormalY=0 NormalZ=1 AngleXU=0 Radius=1.6
    g13: Circle CenterX=137.5 CenterY=85 CenterZ=0 NormalX=0 NormalY=0 NormalZ=1 AngleXU=0 Radius=2
    g14: Circle CenterX=85 CenterY=137.5 CenterZ=0 NormalX=0 NormalY=0 NormalZ=1 AngleXU=0 Radius=2
    g15: Circle CenterX=190 CenterY=137.5 CenterZ=0 NormalX=0 NormalY=0 NormalZ=1 AngleXU=0 Radius=2
    g16: Circle CenterX=137.5 CenterY=190 CenterZ=0 NormalX=0 NormalY=0 NormalZ=1 AngleXU=0 Radius=2
  constraints (50):
    c: Coincident(g1,g0)
    c: Vertical(g1)
    c: Coincident(g2,g1)
    c: Horizontal(g2)
    c: Coincident(g3,g2)
    c: Coincident(g3,g0)
    c: Vertical(g3)
    c: DistanceX(g0,g0) = 6.4
    c: Diameter(g0) = 6.4
    c: DistanceY(g0,g0) = 0
    c: DistanceX(g0) = 137.5
    c: DistanceY(g0) = 137.5
    c: DistanceY(g0,g1) = 10
    c: DistanceX(g4) = 75
    c: DistanceY(g4) = 75
    c: DistanceX(g4,g5) = 125
    c: DistanceX(g4,g6) = 0
    c: DistanceY(g4,g6) = 125
    c: DistanceY(g7,g6) = 0
    c: DistanceY(g7,g8) = 0
    c: DistanceX(g8,g5) = 0
    c: Equal(g5,g4)
    c: Equal(g5,g6)
    c: Equal(g5,g7)
    c: Equal(g5,g8)
    c: Diameter(g5) = 4.25
    c: DistanceX(g6,g7) = 50
    c: DistanceY(g5,g4) = 0
    c: DistanceX(g10,g8) = 9.65
    c: DistanceY(g11,g10) = 20.3
    c: DistanceY(g10,g8) = 9.65
    c: Equal(g9,g10)
    c: Equal(g9,g11)
    c: Equal(g9,g12)
    c: Diameter(g9) = 3.2
    c: DistanceX(g12,g11) = 20.35
    c: DistanceY(g12,g9) = 20.3
    c: DistanceX(g9,g10) = 20.3
    c: DistanceY(g12,g11) = 0
    c: DistanceX(g12,g9) = 0
    c: Equal(g14,g13)
    c: Equal(g14,g15)
    c: Equal(g14,g16)
    c: Diameter(g14) = 4
    c: DistanceX(g14) = 85
    c: Horizontal(g14,g0)
    c: Symmetric(g14,g15,g0)
    c: Vertical(g16,g13)
    c: Symmetric(g13,g16,g0)
    c: DistanceY(g13,g0) = 52.5
FEATURE [Part::Extrusion] Extrude008
  Base = -> Sketch032
  Dir = (0,0,1)
  DirMode = 2
  FaceMakerClass = Part::FaceMakerBullseye
  LengthFwd = 60
  LengthRev = 0
  Placement = pos=(0,0,64) rot=(0,0,1;0rad)
  Solid = true
  Symmetric = false
FEATURE [Part::Cut] Cut002
  Base = -> Fusion057
  Tool = -> Extrude008
FEATURE [Sketcher::SketchObject] Sketch033
  FullyConstrained = true
  MapMode = 4
  Placement = pos=(0,0,0) rot=(0.57735,0.57735,0.57735;2.0944rad)
  Support = -> [Cut002]
  sketch-geometry (4):
    g0: Circle CenterX=131.15 CenterY=84.85 CenterZ=0 NormalX=0 NormalY=0 NormalZ=1 AngleXU=0 Radius=1.6
    g1: Circle CenterX=143.85 CenterY=84.85 CenterZ=0 NormalX=0 NormalY=0 NormalZ=1 AngleXU=0 Radius=1.6
    g2: Circle CenterX=143.85 CenterY=105.15 CenterZ=0 NormalX=0 NormalY=0 NormalZ=1 AngleXU=0 Radius=1.6
    g3: Circle CenterX=131.15 CenterY=105.15 CenterZ=0 NormalX=0 NormalY=0 NormalZ=1 AngleXU=0 Radius=1.6
  constraints (12):
    c: Equal(g0,g1)
    c: Equal(g0,g2)
    c: Equal(g0,g3)
    c: Diameter(g0) = 3.2
    c: DistanceX(g0) = 131.15
    c: DistanceY(g0) = 84.85
    c: DistanceY(g0,g1) = 0
    c: DistanceX(g0,g1) = 12.7
    c: DistanceX(g0,g3) = 0
    c: DistanceX(g2,g1) = 0
    c: DistanceY(g0,g3) = 20.3
    c: DistanceY(g3,g2) = 0
FEATURE [Part::Extrusion] Extrude009
  Base = -> Sketch033
  Dir = (1,0,0)
  DirMode = 2
  FaceMakerClass = Part::FaceMakerBullseye
  LengthFwd = 75
  LengthRev = 0
  Placement = pos=(100,0,0) rot=(0,0,1;0rad)
  Solid = true
  Symmetric = false
FEATURE [Part::Cut] Cut003  label="level01s002"
  Base = -> Cut002
  Tool = -> Extrude009
FEATURE [Sketcher::SketchObject] Sketch035
  FullyConstrained = true
  Placement = pos=(0,0,0) rot=(1,0,0;1.5708rad)
  sketch-geometry (36):
    g0: LineSegment StartX=50 StartY=66 StartZ=0 EndX=97.5 EndY=93.4241 EndZ=0
    g1: LineSegment StartX=97.5 StartY=93.4241 StartZ=0 EndX=97.5 EndY=97.4241 EndZ=0
    g2: LineSegment StartX=97.5 StartY=97.4241 StartZ=0 EndX=50 EndY=70 EndZ=0
    g3: LineSegment StartX=50 StartY=70 StartZ=0 EndX=50 EndY=66 EndZ=0
    g4: LineSegment StartX=50 StartY=78 StartZ=0 EndX=97.5 EndY=105.424 EndZ=0
    g5: LineSegment StartX=97.5 StartY=105.424 StartZ=0 EndX=97.5 EndY=101.424 EndZ=0
    g6: LineSegment StartX=97.5 StartY=101.424 StartZ=0 EndX=50 EndY=74 EndZ=0
    g7: LineSegment StartX=50 StartY=78 StartZ=0 EndX=50 EndY=74 EndZ=0
    g8: LineSegment StartX=50 StartY=86 StartZ=0 EndX=50 EndY=82 EndZ=0
    g9: LineSegment StartX=50 StartY=82 StartZ=0 EndX=97.5 EndY=109.424 EndZ=0
    g10: LineSegment StartX=97.5 StartY=109.424 StartZ=0 EndX=97.5 EndY=113.424 EndZ=0
    g11: LineSegment StartX=97.5 StartY=113.424 StartZ=0 EndX=50 EndY=86 EndZ=0
    g12: LineSegment StartX=75 StartY=120.424 StartZ=0 EndX=137.5 EndY=156.509 EndZ=0
    g13: LineSegment StartX=75 StartY=120.424 StartZ=0 EndX=75 EndY=116.424 EndZ=0
    g14: LineSegment StartX=75 StartY=116.424 StartZ=0 EndX=137.5 EndY=152.509 EndZ=0
    g15: LineSegment StartX=75 StartY=112.424 StartZ=0 EndX=137.5 EndY=148.509 EndZ=0
    g16: LineSegment StartX=137.5 StartY=144.509 StartZ=0 EndX=75 EndY=108.424 EndZ=0
    g17: LineSegment StartX=75 StartY=108.424 StartZ=0 EndX=75 EndY=112.424 EndZ=0
    g18: LineSegment StartX=137.5 StartY=156.509 StartZ=0 EndX=200 EndY=120.424 EndZ=0
    g19: LineSegment StartX=200 StartY=120.424 StartZ=0 EndX=200 EndY=116.424 EndZ=0
    g20: LineSegment StartX=200 StartY=116.424 StartZ=0 EndX=137.5 EndY=152.509 EndZ=0
    g21: LineSegment StartX=137.5 StartY=148.509 StartZ=0 EndX=200 EndY=112.424 EndZ=0
    g22: LineSegment StartX=200 StartY=112.424 StartZ=0 EndX=200 EndY=108.424 EndZ=0
    g23: LineSegment StartX=200 StartY=108.424 StartZ=0 EndX=137.5 EndY=144.509 EndZ=0
    g24: LineSegment StartX=177.5 StartY=113.424 StartZ=0 EndX=225 EndY=86 EndZ=0
    g25: LineSegment StartX=225 StartY=86 StartZ=0 EndX=225 EndY=82 EndZ=0
    g26: LineSegment StartX=225 StartY=82 StartZ=0 EndX=177.5 EndY=109.424 EndZ=0
    g27: LineSegment StartX=177.5 StartY=109.424 StartZ=0 EndX=177.5 EndY=113.424 EndZ=0
    g28: LineSegment StartX=177.5 StartY=105.424 StartZ=0 EndX=225 EndY=78 EndZ=0
    g29: LineSegment StartX=225 StartY=78 StartZ=0 EndX=225 EndY=74 EndZ=0
    g30: LineSegment StartX=225 StartY=74 StartZ=0 EndX=177.5 EndY=101.424 EndZ=0
    g31: LineSegment StartX=177.5 StartY=101.424 StartZ=0 EndX=177.5 EndY=105.424 EndZ=0
    g32: LineSegment StartX=177.5 StartY=97.4241 StartZ=0 EndX=225 EndY=70 EndZ=0
    g33: LineSegment StartX=225 StartY=70 StartZ=0 EndX=225 EndY=66 EndZ=0
    g34: LineSegment StartX=225 StartY=66 StartZ=0 EndX=177.5 EndY=93.4241 EndZ=0
    g35: LineSegment StartX=177.5 StartY=97.4241 StartZ=0 EndX=177.5 EndY=93.4241 EndZ=0
  constraints (108):
    c: Angle(g0) = 0.523599
    c: DistanceX(g0) = 50
    c: Coincident(g1,g0)
    c: Vertical(g1)
    c: Coincident(g2,g1)
    c: Coincident(g3,g2)
    c: Vertical(g3)
    c: DistanceY(g0,g2) = 4
    c: Parallel(g0,g2)
    c: Coincident(g0,g3)
    c: Coincident(g5,g4)
    c: Coincident(g7,g4)
    c: Coincident(g7,g6)
    c: Coincident(g10,g9)
    c: Coincident(g11,g8)
    c: Vertical(g8)
    c: Vertical(g7)
    c: Vertical(g5)
    c: Vertical(g10)
    c: Coincident(g5,g6)
    c: Coincident(g10,g11)
    c: Coincident(g8,g9)
    c: Parallel(g2,g6)
    c: Parallel(g6,g4)
    c: Parallel(g4,g9)
    c: Parallel(g9,g11)
    c: DistanceX(g6,g2) = 0
    c: DistanceX(g8,g4) = 0
    c: DistanceY(g2,g6) = 4
    c: DistanceY(g6,g4) = 4
    c: DistanceY(g4,g8) = 4
    c: DistanceY(g8,g8) = 4
    c: DistanceX(g5,g1) = 0
    c: DistanceX(g4,g9) = 0
    c: DistanceY(g0) = 66
    c: Coincident(g13,g12)
    c: Vertical(g13)
    c: Coincident(g17,g16)
    c: Coincident(g17,g15)
    c: DistanceY(g16,g10) = 5
    c: Vertical(g17)
    c: Parallel(g16,g11)
    c: DistanceY(g16,g15) = 4
    c: DistanceY(g15,g13) = 4
    c: Coincident(g13,g14)
    c: Parallel(g12,g14)
    c: Parallel(g14,g15)
    c: Parallel(g15,g16)
    c: DistanceY(g13,g12) = 4
    c: DistanceX(g15,g13) = 0
    c: DistanceX(g16,g16) = 62.5
    c: DistanceX(g14,g15) = 0
    c: Coincident(g18,g12)
    c: Coincident(g19,g18)
    c: Vertical(g19)
    c: Coincident(g20,g19)
    c: Coincident(g20,g14)
    c: Coincident(g21,g15)
    c: Coincident(g22,g21)
    c: Coincident(g23,g22)
    c: Coincident(g23,g16)
    c: Parallel(g23,g21)
    c: Parallel(g21,g20)
    c: Parallel(g20,g18)
    c: DistanceX(g14,g12) = 0
    c: DistanceX(g21,g19) = 0
    c: Vertical(g22)
    c: Coincident(g25,g24)
    c: Coincident(g26,g25)
    c: Coincident(g27,g26)
    c: Coincident(g27,g24)
    c: Vertical(g27)
    c: Coincident(g29,g28)
    c: Vertical(g29)
    c: Coincident(g31,g30)
    c: Coincident(g31,g28)
    c: Coincident(g33,g32)
    c: Vertical(g33)
    c: Coincident(g34,g33)
    c: Coincident(g35,g32)
    c: Coincident(g35,g34)
    c: DistanceY(g10,g24) = 0
    c: Vertical(g35)
    c: Vertical(g31)
    c: DistanceX(g28,g24) = 0
    c: DistanceX(g32,g30) = 0
    c: Vertical(g25)
    c: DistanceY(g26,g24) = 4
    c: DistanceY(g28,g26) = 4
    c: DistanceY(g30,g28) = 4
    c: DistanceY(g32,g30) = 4
    c: DistanceY(g34,g32) = 4
    c: Parallel(g34,g32)
    c: Parallel(g32,g30)
    c: Parallel(g30,g28)
    c: Parallel(g28,g26)
    c: Parallel(g26,g24)
    c: Parallel(g24,g23)
    c: Coincident(g29,g30)
    c: DistanceY(g33,g0) = 0
    c: DistanceX(g32,g29) = 0
    c: DistanceX(g28,g25) = 0
    c: DistanceX(g12) = 137.5
    c: DistanceY(g16,g15) = 4
    c: DistanceX(g12,g18) = 125
    c: DistanceY(g22,g16) = 0
    c: DistanceX(g10) = 97.5
    c: DistanceX(g10,g24) = 80
FEATURE [Part::Extrusion] Extrude010
  Base = -> Sketch035
  Dir = (0,-1,2e-16)
  DirMode = 2
  FaceMakerClass = Part::FaceMakerBullseye
  LengthFwd = 275
  LengthRev = 0
  Reversed = true
  Solid = true
  Symmetric = false
FEATURE [Sketcher::SketchObject] Sketch036
  FullyConstrained = true
  Placement = pos=(0,0,0) rot=(1,0,0;1.5708rad)
  sketch-geometry (36):
    g0: LineSegment StartX=50 StartY=66 StartZ=0 EndX=97.5 EndY=93.4241 EndZ=0
    g1: LineSegment StartX=97.5 StartY=93.4241 StartZ=0 EndX=97.5 EndY=97.4241 EndZ=0
    g2: LineSegment StartX=97.5 StartY=97.4241 StartZ=0 EndX=50 EndY=70 EndZ=0
    g3: LineSegment StartX=50 StartY=70 StartZ=0 EndX=50 EndY=66 EndZ=0
    g4: LineSegment StartX=50 StartY=78 StartZ=0 EndX=97.5 EndY=105.424 EndZ=0
    g5: LineSegment StartX=97.5 StartY=105.424 StartZ=0 EndX=97.5 EndY=101.424 EndZ=0
    g6: LineSegment StartX=97.5 StartY=101.424 StartZ=0 EndX=50 EndY=74 EndZ=0
    g7: LineSegment StartX=50 StartY=78 StartZ=0 EndX=50 EndY=74 EndZ=0
    g8: LineSegment StartX=50 StartY=86 StartZ=0 EndX=50 EndY=82 EndZ=0
    g9: LineSegment StartX=50 StartY=82 StartZ=0 EndX=97.5 EndY=109.424 EndZ=0
    g10: LineSegment StartX=97.5 StartY=109.424 StartZ=0 EndX=97.5 EndY=113.424 EndZ=0
    g11: LineSegment StartX=97.5 StartY=113.424 StartZ=0 EndX=50 EndY=86 EndZ=0
    g12: LineSegment StartX=75 StartY=120.424 StartZ=0 EndX=75 EndY=116.424 EndZ=0
    g13: LineSegment StartX=75 StartY=112.424 StartZ=0 EndX=137.5 EndY=148.509 EndZ=0
    g14: LineSegment StartX=137.5 StartY=144.509 StartZ=0 EndX=75 EndY=108.424 EndZ=0
    g15: LineSegment StartX=75 StartY=108.424 StartZ=0 EndX=75 EndY=112.424 EndZ=0
    g16: LineSegment StartX=137.5 StartY=148.509 StartZ=0 EndX=200 EndY=112.424 EndZ=0
    g17: LineSegment StartX=200 StartY=112.424 StartZ=0 EndX=200 EndY=108.424 EndZ=0
    g18: LineSegment StartX=200 StartY=108.424 StartZ=0 EndX=137.5 EndY=144.509 EndZ=0
    g19: LineSegment StartX=177.5 StartY=113.424 StartZ=0 EndX=225 EndY=86 EndZ=0
    g20: LineSegment StartX=225 StartY=86 StartZ=0 EndX=225 EndY=82 EndZ=0
    g21: LineSegment StartX=225 StartY=82 StartZ=0 EndX=177.5 EndY=109.424 EndZ=0
    g22: LineSegment StartX=177.5 StartY=109.424 StartZ=0 EndX=177.5 EndY=113.424 EndZ=0
    g23: LineSegment StartX=177.5 StartY=105.424 StartZ=0 EndX=225 EndY=78 EndZ=0
    g24: LineSegment StartX=225 StartY=78 StartZ=0 EndX=225 EndY=74 EndZ=0
    g25: LineSegment StartX=225 StartY=74 StartZ=0 EndX=177.5 EndY=101.424 EndZ=0
    g26: LineSegment StartX=177.5 StartY=101.424 StartZ=0 EndX=177.5 EndY=105.424 EndZ=0
    g27: LineSegment StartX=177.5 StartY=97.4241 StartZ=0 EndX=225 EndY=70 EndZ=0
    g28: LineSegment StartX=225 StartY=70 StartZ=0 EndX=225 EndY=66 EndZ=0
    g29: LineSegment StartX=225 StartY=66 StartZ=0 EndX=177.5 EndY=93.4241 EndZ=0
    g30: LineSegment StartX=177.5 StartY=97.4241 StartZ=0 EndX=177.5 EndY=93.4241 EndZ=0
    g31: LineSegment StartX=75 StartY=116.424 StartZ=0 EndX=137.5 EndY=152.509 EndZ=0
    g32: LineSegment StartX=137.5 StartY=152.509 StartZ=0 EndX=200 EndY=116.424 EndZ=0
    g33: LineSegment StartX=200 StartY=116.424 StartZ=0 EndX=200 EndY=120.424 EndZ=0
    g34: LineSegment StartX=200 StartY=120.424 StartZ=0 EndX=137.5 EndY=156.509 EndZ=0
    g35: LineSegment StartX=137.5 StartY=156.509 StartZ=0 EndX=75 EndY=120.424 EndZ=0
  constraints (108):
    c: Angle(g0) = 0.523599
    c: DistanceX(g0) = 50
    c: Coincident(g1,g0)
    c: Vertical(g1)
    c: Coincident(g2,g1)
    c: Coincident(g3,g2)
    c: Vertical(g3)
    c: DistanceY(g0,g2) = 4
    c: Parallel(g0,g2)
    c: Coincident(g0,g3)
    c: Coincident(g5,g4)
    c: Coincident(g7,g4)
    c: Coincident(g7,g6)
    c: Coincident(g10,g9)
    c: Coincident(g11,g8)
    c: Vertical(g8)
    c: Vertical(g7)
    c: Vertical(g5)
    c: Vertical(g10)
    c: Coincident(g5,g6)
    c: Coincident(g10,g11)
    c: Coincident(g8,g9)
    c: Parallel(g2,g6)
    c: Parallel(g6,g4)
    c: Parallel(g4,g9)
    c: Parallel(g9,g11)
    c: DistanceX(g6,g2) = 0
    c: DistanceX(g8,g4) = 0
    c: DistanceY(g2,g6) = 4
    c: DistanceY(g6,g4) = 4
    c: DistanceY(g4,g8) = 4
    c: DistanceY(g8,g8) = 4
    c: DistanceX(g5,g1) = 0
    c: DistanceX(g4,g9) = 0
    c: DistanceY(g0) = 66
    c: Vertical(g12)
    c: Coincident(g15,g14)
    c: Coincident(g15,g13)
    c: DistanceY(g14,g10) = 5
    c: Vertical(g15)
    c: Parallel(g14,g11)
    c: DistanceY(g14,g13) = 4
    c: DistanceY(g13,g12) = 4
    c: Parallel(g13,g14)
    c: DistanceY(g12,g12) = 4
    c: DistanceX(g13,g12) = 0
    c: DistanceX(g14,g14) = 62.5
    c: Coincident(g16,g13)
    c: Coincident(g17,g16)
    c: Coincident(g18,g17)
    c: Coincident(g18,g14)
    c: Parallel(g18,g16)
    c: Vertical(g17)
    c: Coincident(g20,g19)
    c: Coincident(g21,g20)
    c: Coincident(g22,g21)
    c: Coincident(g22,g19)
    c: Vertical(g22)
    c: Coincident(g24,g23)
    c: Vertical(g24)
    c: Coincident(g26,g25)
    c: Coincident(g26,g23)
    c: Coincident(g28,g27)
    c: Vertical(g28)
    c: Coincident(g29,g28)
    c: Coincident(g30,g27)
    c: Coincident(g30,g29)
    c: DistanceY(g10,g19) = 0
    c: Vertical(g30)
    c: Vertical(g26)
    c: DistanceX(g23,g19) = 0
    c: DistanceX(g27,g25) = 0
    c: Vertical(g20)
    c: DistanceY(g21,g19) = 4
    c: DistanceY(g23,g21) = 4
    c: DistanceY(g25,g23) = 4
    c: DistanceY(g27,g25) = 4
    c: DistanceY(g29,g27) = 4
    c: Parallel(g29,g27)
    c: Parallel(g27,g25)
    c: Parallel(g25,g23)
    c: Parallel(g23,g21)
    c: Parallel(g21,g19)
    c: Parallel(g19,g18)
    c: Coincident(g24,g25)
    c: DistanceY(g28,g0) = 0
    c: DistanceX(g27,g24) = 0
    c: DistanceX(g23,g20) = 0
    c: DistanceX(g13) = 137.5
    c: DistanceX(g14,g10) = 22.5
    c: DistanceX(g19,g17) = 22.5
    c: DistanceX(g14,g17) = 125
    c: DistanceX(g14,g13) = 0
    c: DistanceY(g17,g14) = 0
    c: Coincident(g31,g12)
    c: Coincident(g32,g31)
    c: Vertical(g33)
    c: Coincident(g34,g33)
    c: Coincident(g35,g12)
    c: DistanceX(g13,g31) = 0
    c: Coincident(g34,g35)
    c: DistanceX(g34,g31) = 0
    c: Parallel(g13,g31)
    c: Parallel(g31,g35)
    c: Parallel(g16,g32)
    c: Parallel(g32,g34)
    c: Coincident(g32,g33)
    c: DistanceX(g16,g32) = 0
FEATURE [Part::Extrusion] Extrude011
  Base = -> Sketch036
  Dir = (0,-1,2e-16)
  DirMode = 2
  FaceMakerClass = Part::FaceMakerBullseye
  LengthFwd = 275
  LengthRev = 0
  Placement = pos=(275,0,0) rot=(0,0,1;1.5708rad)
  Reversed = true
  Solid = true
  Symmetric = false
FEATURE [Part::MultiFuse] Fusion058  label="keeps-legacy"
  Shapes = -> [Extrude010,Extrude011]
FEATURE [Sketcher::SketchObject] Sketch037
  FullyConstrained = true
  sketch-geometry (4):
    g0: LineSegment StartX=0 StartY=275 StartZ=0 EndX=275 EndY=275 EndZ=0
    g1: LineSegment StartX=275 StartY=275 StartZ=0 EndX=275 EndY=0 EndZ=0
    g2: LineSegment StartX=275 StartY=0 StartZ=0 EndX=0 EndY=0 EndZ=0
    g3: LineSegment StartX=0 StartY=0 StartZ=0 EndX=0 EndY=275 EndZ=0
  constraints (11):
    c: Coincident(g0,g1)
    c: Coincident(g1,g2)
    c: Coincident(g2,g3)
    c: Coincident(g3,g0)
    c: Horizontal(g0)
    c: Horizontal(g2)
    c: Vertical(g1)
    c: Vertical(g3)
    c: Coincident(g2,g-1)
    c: DistanceX(g2,g2) = 275
    c: DistanceY(g3,g3) = 275
FEATURE [Sketcher::SketchObject] Sketch038
  FullyConstrained = true
  Placement = pos=(0,0,175.1) rot=(0,0,1;0rad)
  sketch-geometry (5):
    g0: GeomPoint X=137.5 Y=137.5 Z=0
    g1: LineSegment StartX=137.55 StartY=137.55 StartZ=0 EndX=137.55 EndY=137.45 EndZ=0
    g2: LineSegment StartX=137.55 StartY=137.45 StartZ=0 EndX=137.45 EndY=137.45 EndZ=0
    g3: LineSegment StartX=137.45 StartY=137.45 StartZ=0 EndX=137.45 EndY=137.55 EndZ=0
    g4: LineSegment StartX=137.45 StartY=137.55 StartZ=0 EndX=137.55 EndY=137.55 EndZ=0
  constraints (14):
    c: Coincident(g1,g2)
    c: Horizontal(g2)
    c: Vertical(g1)
    c: DistanceX(g2,g2) = 0.1
    c: DistanceX(g2,g0) = 0.05
    c: DistanceY(g1,g1) = 0.1
    c: DistanceY(g1,g0) = -0.05
    c: DistanceX(g0) = 137.5
    c: DistanceY(g0) = 137.5
    c: Coincident(g3,g2)
    c: Vertical(g3)
    c: Coincident(g4,g3)
    c: Coincident(g4,g1)
    c: Horizontal(g4)
FEATURE [Part::Loft] Loft005  label="outerLayer005"
  Closed = false
  MaxDegree = 5
  Ruled = false
  Sections = -> [Sketch037,Sketch038]
  Solid = true
FEATURE [Sketcher::SketchObject] Sketch039
  FullyConstrained = true
  Placement = pos=(0,0,0) rot=(1,0,0;1.5708rad)
  sketch-geometry (28):
    g0: LineSegment StartX=50 StartY=70 StartZ=0 EndX=97.5 EndY=97.4241 EndZ=0
    g1: LineSegment StartX=97.5 StartY=97.4241 StartZ=0 EndX=97.5 EndY=101.424 EndZ=0
    g2: LineSegment StartX=97.5 StartY=101.424 StartZ=0 EndX=50 EndY=74 EndZ=0
    g3: LineSegment StartX=50 StartY=74 StartZ=0 EndX=50 EndY=70 EndZ=0
    g4: LineSegment StartX=50 StartY=82 StartZ=0 EndX=97.5 EndY=109.424 EndZ=0
    g5: LineSegment StartX=97.5 StartY=109.424 StartZ=0 EndX=97.5 EndY=105.424 EndZ=0
    g6: LineSegment StartX=97.5 StartY=105.424 StartZ=0 EndX=50 EndY=78 EndZ=0
    g7: LineSegment StartX=50 StartY=82 StartZ=0 EndX=50 EndY=78 EndZ=0
    g8: LineSegment StartX=75 StartY=116.424 StartZ=0 EndX=137.5 EndY=152.509 EndZ=0
    g9: LineSegment StartX=137.5 StartY=148.509 StartZ=0 EndX=75 EndY=112.424 EndZ=0
    g10: LineSegment StartX=75 StartY=112.424 StartZ=0 EndX=75 EndY=116.424 EndZ=0
    g11: LineSegment StartX=137.5 StartY=152.509 StartZ=0 EndX=200 EndY=116.424 EndZ=0
    g12: LineSegment StartX=200 StartY=116.424 StartZ=0 EndX=200 EndY=112.424 EndZ=0
    g13: LineSegment StartX=200 StartY=112.424 StartZ=0 EndX=137.5 EndY=148.509 EndZ=0
    g14: LineSegment StartX=177.5 StartY=109.424 StartZ=0 EndX=225 EndY=82 EndZ=0
    g15: LineSegment StartX=225 StartY=82 StartZ=0 EndX=225 EndY=78 EndZ=0
    g16: LineSegment StartX=225 StartY=78 StartZ=0 EndX=177.5 EndY=105.424 EndZ=0
    g17: LineSegment StartX=177.5 StartY=105.424 StartZ=0 EndX=177.5 EndY=109.424 EndZ=0
    g18: LineSegment StartX=177.5 StartY=101.424 StartZ=0 EndX=225 EndY=74 EndZ=0
    g19: LineSegment StartX=225 StartY=74 StartZ=0 EndX=225 EndY=70 EndZ=0
    g20: LineSegment StartX=225 StartY=70 StartZ=0 EndX=177.5 EndY=97.4241 EndZ=0
    g21: LineSegment StartX=177.5 StartY=101.424 StartZ=0 EndX=177.5 EndY=97.4241 EndZ=0
    g22: LineSegment StartX=75 StartY=120.424 StartZ=0 EndX=137.5 EndY=156.509 EndZ=0
    g23: LineSegment StartX=137.5 StartY=156.509 StartZ=0 EndX=200 EndY=120.424 EndZ=0
    g24: LineSegment StartX=200 StartY=120.424 StartZ=0 EndX=200 EndY=124.424 EndZ=0
    g25: LineSegment StartX=200 StartY=124.424 StartZ=0 EndX=137.5 EndY=160.509 EndZ=0
    g26: LineSegment StartX=137.5 StartY=160.509 StartZ=0 EndX=75 EndY=124.424 EndZ=0
    g27: LineSegment StartX=75 StartY=124.424 StartZ=0 EndX=75 EndY=120.424 EndZ=0
  constraints (84):
    c: Angle(g0) = 0.523599
    c: DistanceX(g0) = 50
    c: Coincident(g1,g0)
    c: Vertical(g1)
    c: Coincident(g2,g1)
    c: Coincident(g3,g2)
    c: Vertical(g3)
    c: DistanceY(g0,g2) = 4
    c: Parallel(g0,g2)
    c: Coincident(g0,g3)
    c: Coincident(g5,g4)
    c: Coincident(g7,g4)
    c: Coincident(g7,g6)
    c: Vertical(g7)
    c: Vertical(g5)
    c: Coincident(g5,g6)
    c: Parallel(g2,g6)
    c: Parallel(g6,g4)
    c: DistanceX(g6,g2) = 0
    c: DistanceY(g2,g6) = 4
    c: DistanceY(g6,g4) = 4
    c: DistanceX(g5,g1) = 0
    c: DistanceY(g0) = 70
    c: Coincident(g10,g9)
    c: Coincident(g10,g8)
    c: Vertical(g10)
    c: DistanceY(g9,g8) = 4
    c: Parallel(g8,g9)
    c: DistanceX(g9,g9) = 62.5
    c: Coincident(g11,g8)
    c: Coincident(g12,g11)
    c: Coincident(g13,g12)
    c: Coincident(g13,g9)
    c: Parallel(g13,g11)
    c: Vertical(g12)
    c: Coincident(g15,g14)
    c: Vertical(g15)
    c: Coincident(g17,g16)
    c: Coincident(g17,g14)
    c: Coincident(g19,g18)
    c: Vertical(g19)
    c: Coincident(g20,g19)
    c: Coincident(g21,g18)
    c: Coincident(g21,g20)
    c: Vertical(g21)
    c: Vertical(g17)
    c: DistanceX(g18,g16) = 0
    c: DistanceY(g16,g14) = 4
    c: DistanceY(g18,g16) = 4
    c: DistanceY(g20,g18) = 4
    c: Parallel(g20,g18)
    c: Parallel(g18,g16)
    c: Parallel(g16,g14)
    c: Coincident(g15,g16)
    c: DistanceY(g19,g0) = 0
    c: DistanceX(g18,g15) = 0
    c: DistanceY(g4,g9) = 3
    c: DistanceY(g4,g14) = 0
    c: DistanceY(g9,g12) = 0
    c: DistanceX(g9,g8) = 0
    c: Angle(g9) = -2.61799
    c: DistanceX(g9,g4) = 22.5
    c: DistanceX(g14,g12) = 22.5
    c: DistanceX(g9,g14) = 87.5
    c: DistanceX(g8) = 137.5
    c: DistanceX(g9,g12) = 125
    c: Coincident(g23,g22)
    c: Coincident(g24,g23)
    c: Vertical(g24)
    c: Coincident(g26,g25)
    c: Coincident(g27,g22)
    c: Vertical(g27)
    c: DistanceX(g22,g8) = 0
    c: DistanceX(g8,g22) = 0
    c: DistanceX(g25,g22) = 0
    c: Coincident(g24,g25)
    c: Coincident(g26,g27)
    c: DistanceY(g8,g22) = 4
    c: DistanceY(g22,g25) = 4
    c: DistanceY(g11,g23) = 4
    c: DistanceY(g23,g24) = 4
    c: DistanceX(g23,g11) = 0
    c: DistanceY(g8,g22) = 4
    c: DistanceY(g22,g26) = 4
FEATURE [Part::Extrusion] Extrude012  label="cuts"
  Base = -> Sketch039
  Dir = (0,-1,2e-16)
  DirMode = 2
  FaceMakerClass = Part::FaceMakerBullseye
  LengthFwd = 275
  LengthRev = 0
  Reversed = true
  Solid = true
  Symmetric = false
FEATURE [Sketcher::SketchObject] Sketch040
  FullyConstrained = true
  Placement = pos=(0,0,0) rot=(1,0,0;1.5708rad)
  sketch-geometry (28):
    g0: LineSegment StartX=50 StartY=70 StartZ=0 EndX=97.5 EndY=97.4241 EndZ=0
    g1: LineSegment StartX=97.5 StartY=97.4241 StartZ=0 EndX=97.5 EndY=101.424 EndZ=0
    g2: LineSegment StartX=97.5 StartY=101.424 StartZ=0 EndX=50 EndY=74 EndZ=0
    g3: LineSegment StartX=50 StartY=74 StartZ=0 EndX=50 EndY=70 EndZ=0
    g4: LineSegment StartX=50 StartY=82 StartZ=0 EndX=97.5 EndY=109.424 EndZ=0
    g5: LineSegment StartX=97.5 StartY=109.424 StartZ=0 EndX=97.5 EndY=105.424 EndZ=0
    g6: LineSegment StartX=97.5 StartY=105.424 StartZ=0 EndX=50 EndY=78 EndZ=0
    g7: LineSegment StartX=50 StartY=82 StartZ=0 EndX=50 EndY=78 EndZ=0
    g8: LineSegment StartX=75 StartY=116.424 StartZ=0 EndX=137.5 EndY=152.509 EndZ=0
    g9: LineSegment StartX=137.5 StartY=148.509 StartZ=0 EndX=75 EndY=112.424 EndZ=0
    g10: LineSegment StartX=75 StartY=112.424 StartZ=0 EndX=75 EndY=116.424 EndZ=0
    g11: LineSegment StartX=137.5 StartY=152.509 StartZ=0 EndX=200 EndY=116.424 EndZ=0
    g12: LineSegment StartX=200 StartY=116.424 StartZ=0 EndX=200 EndY=112.424 EndZ=0
    g13: LineSegment StartX=200 StartY=112.424 StartZ=0 EndX=137.5 EndY=148.509 EndZ=0
    g14: LineSegment StartX=177.5 StartY=109.424 StartZ=0 EndX=225 EndY=82 EndZ=0
    g15: LineSegment StartX=225 StartY=82 StartZ=0 EndX=225 EndY=78 EndZ=0
    g16: LineSegment StartX=225 StartY=78 StartZ=0 EndX=177.5 EndY=105.424 EndZ=0
    g17: LineSegment StartX=177.5 StartY=105.424 StartZ=0 EndX=177.5 EndY=109.424 EndZ=0
    g18: LineSegment StartX=177.5 StartY=101.424 StartZ=0 EndX=225 EndY=74 EndZ=0
    g19: LineSegment StartX=225 StartY=74 StartZ=0 EndX=225 EndY=70 EndZ=0
    g20: LineSegment StartX=225 StartY=70 StartZ=0 EndX=177.5 EndY=97.4241 EndZ=0
    g21: LineSegment StartX=177.5 StartY=101.424 StartZ=0 EndX=177.5 EndY=97.4241 EndZ=0
    g22: LineSegment StartX=75 StartY=120.424 StartZ=0 EndX=75 EndY=124.424 EndZ=0
    g23: LineSegment StartX=75 StartY=124.424 StartZ=0 EndX=137.5 EndY=160.509 EndZ=0
    g24: LineSegment StartX=137.5 StartY=160.509 StartZ=0 EndX=200 EndY=124.424 EndZ=0
    g25: LineSegment StartX=200 StartY=124.424 StartZ=0 EndX=200 EndY=120.424 EndZ=0
    g26: LineSegment StartX=200 StartY=120.424 StartZ=0 EndX=137.5 EndY=156.509 EndZ=0
    g27: LineSegment StartX=137.5 StartY=156.509 StartZ=0 EndX=75 EndY=120.424 EndZ=0
  constraints (84):
    c: Angle(g0) = 0.523599
    c: DistanceX(g0) = 50
    c: Coincident(g1,g0)
    c: Vertical(g1)
    c: Coincident(g2,g1)
    c: Coincident(g3,g2)
    c: Vertical(g3)
    c: DistanceY(g0,g2) = 4
    c: Parallel(g0,g2)
    c: Coincident(g0,g3)
    c: Coincident(g5,g4)
    c: Coincident(g7,g4)
    c: Coincident(g7,g6)
    c: Vertical(g7)
    c: Vertical(g5)
    c: Coincident(g5,g6)
    c: Parallel(g2,g6)
    c: Parallel(g6,g4)
    c: DistanceX(g6,g2) = 0
    c: DistanceY(g2,g6) = 4
    c: DistanceY(g6,g4) = 4
    c: DistanceX(g5,g1) = 0
    c: DistanceY(g0) = 70
    c: Coincident(g10,g9)
    c: Coincident(g10,g8)
    c: Vertical(g10)
    c: DistanceY(g9,g8) = 4
    c: Parallel(g8,g9)
    c: DistanceX(g9,g9) = 62.5
    c: Coincident(g11,g8)
    c: Coincident(g12,g11)
    c: Coincident(g13,g12)
    c: Coincident(g13,g9)
    c: Parallel(g13,g11)
    c: Vertical(g12)
    c: Coincident(g15,g14)
    c: Vertical(g15)
    c: Coincident(g17,g16)
    c: Coincident(g17,g14)
    c: Coincident(g19,g18)
    c: Vertical(g19)
    c: Coincident(g20,g19)
    c: Coincident(g21,g18)
    c: Coincident(g21,g20)
    c: Vertical(g21)
    c: Vertical(g17)
    c: DistanceX(g18,g16) = 0
    c: DistanceY(g16,g14) = 4
    c: DistanceY(g18,g16) = 4
    c: DistanceY(g20,g18) = 4
    c: Parallel(g20,g18)
    c: Parallel(g18,g16)
    c: Parallel(g16,g14)
    c: Coincident(g15,g16)
    c: DistanceY(g19,g0) = 0
    c: DistanceX(g18,g15) = 0
    c: DistanceX(g14,g14) = 47.5
    c: DistanceX(g4,g4) = 47.5
    c: DistanceX(g4,g14) = 80
    c: Parallel(g9,g4)
    c: DistanceX(g9,g8) = 0
    c: DistanceY(g4,g9) = 3
    c: DistanceY(g14,g12) = 3
    c: DistanceY(g14,g4) = 0
    c: DistanceX(g8) = 137.5
    c: DistanceX(g9,g12) = 125
    c: Vertical(g22)
    c: Coincident(g23,g22)
    c: Coincident(g24,g23)
    c: Coincident(g25,g24)
    c: Vertical(g25)
    c: Coincident(g26,g25)
    c: Coincident(g27,g22)
    c: DistanceX(g22,g8) = 0
    c: DistanceY(g8,g22) = 4
    c: DistanceY(g22,g22) = 4
    c: Coincident(g26,g27)
    c: DistanceX(g26,g8) = 0
    c: DistanceY(g26,g23) = 4
    c: DistanceY(g8,g26) = 4
    c: DistanceX(g23,g26) = 0
    c: DistanceX(g25,g11) = 0
    c: DistanceY(g11,g25) = 4
    c: DistanceY(g25,g24) = 4
FEATURE [Part::Extrusion] Extrude013  label="cuts001"
  Base = -> Sketch040
  Dir = (0,-1,2e-16)
  DirMode = 2
  FaceMakerClass = Part::FaceMakerBullseye
  LengthFwd = 275
  LengthRev = 0
  Placement = pos=(275,0,0) rot=(0,0,1;1.5708rad)
  Reversed = true
  Solid = true
  Symmetric = false
FEATURE [Sketcher::SketchObject] Sketch041
  FullyConstrained = true
  sketch-geometry (4):
    g0: LineSegment StartX=0 StartY=275 StartZ=0 EndX=275 EndY=275 EndZ=0
    g1: LineSegment StartX=275 StartY=275 StartZ=0 EndX=275 EndY=0 EndZ=0
    g2: LineSegment StartX=275 StartY=0 StartZ=0 EndX=0 EndY=0 EndZ=0
    g3: LineSegment StartX=0 StartY=0 StartZ=0 EndX=0 EndY=275 EndZ=0
  constraints (11):
    c: Coincident(g0,g1)
    c: Coincident(g1,g2)
    c: Coincident(g2,g3)
    c: Coincident(g3,g0)
    c: Horizontal(g0)
    c: Horizontal(g2)
    c: Vertical(g1)
    c: Vertical(g3)
    c: Coincident(g2,g-1)
    c: DistanceX(g2,g2) = 275
    c: DistanceY(g3,g3) = 275
FEATURE [Sketcher::SketchObject] Sketch042
  FullyConstrained = true
  Placement = pos=(0,0,175.1) rot=(0,0,1;0rad)
  sketch-geometry (5):
    g0: GeomPoint X=137.5 Y=137.5 Z=0
    g1: LineSegment StartX=137.55 StartY=137.55 StartZ=0 EndX=137.55 EndY=137.45 EndZ=0
    g2: LineSegment StartX=137.55 StartY=137.45 StartZ=0 EndX=137.45 EndY=137.45 EndZ=0
    g3: LineSegment StartX=137.45 StartY=137.45 StartZ=0 EndX=137.45 EndY=137.55 EndZ=0
    g4: LineSegment StartX=137.45 StartY=137.55 StartZ=0 EndX=137.55 EndY=137.55 EndZ=0
  constraints (14):
    c: Coincident(g1,g2)
    c: Horizontal(g2)
    c: Vertical(g1)
    c: DistanceX(g2,g2) = 0.1
    c: DistanceX(g2,g0) = 0.05
    c: DistanceY(g1,g1) = 0.1
    c: DistanceY(g1,g0) = -0.05
    c: DistanceX(g0) = 137.5
    c: DistanceY(g0) = 137.5
    c: Coincident(g3,g2)
    c: Vertical(g3)
    c: Coincident(g4,g3)
    c: Coincident(g4,g1)
    c: Horizontal(g4)
FEATURE [Part::Loft] Loft006  label="outerLayer006"
  Closed = false
  MaxDegree = 5
  Ruled = false
  Sections = -> [Sketch041,Sketch042]
  Solid = true
FEATURE [Sketcher::SketchObject] Sketch043
  FullyConstrained = true
  sketch-geometry (4):
    g0: LineSegment StartX=0 StartY=275 StartZ=0 EndX=275 EndY=275 EndZ=0
    g1: LineSegment StartX=275 StartY=275 StartZ=0 EndX=275 EndY=0 EndZ=0
    g2: LineSegment StartX=275 StartY=0 StartZ=0 EndX=0 EndY=0 EndZ=0
    g3: LineSegment StartX=0 StartY=0 StartZ=0 EndX=0 EndY=275 EndZ=0
  constraints (11):
    c: Coincident(g0,g1)
    c: Coincident(g1,g2)
    c: Coincident(g2,g3)
    c: Coincident(g3,g0)
    c: Horizontal(g0)
    c: Horizontal(g2)
    c: Vertical(g1)
    c: Vertical(g3)
    c: Coincident(g2,g-1)
    c: DistanceX(g2,g2) = 275
    c: DistanceY(g3,g3) = 275
FEATURE [Sketcher::SketchObject] Sketch044
  FullyConstrained = true
  Placement = pos=(0,0,175.1) rot=(0,0,1;0rad)
  sketch-geometry (5):
    g0: GeomPoint X=137.5 Y=137.5 Z=0
    g1: LineSegment StartX=137.55 StartY=137.55 StartZ=0 EndX=137.55 EndY=137.45 EndZ=0
    g2: LineSegment StartX=137.55 StartY=137.45 StartZ=0 EndX=137.45 EndY=137.45 EndZ=0
    g3: LineSegment StartX=137.45 StartY=137.45 StartZ=0 EndX=137.45 EndY=137.55 EndZ=0
    g4: LineSegment StartX=137.45 StartY=137.55 StartZ=0 EndX=137.55 EndY=137.55 EndZ=0
  constraints (14):
    c: Coincident(g1,g2)
    c: Horizontal(g2)
    c: Vertical(g1)
    c: DistanceX(g2,g2) = 0.1
    c: DistanceX(g2,g0) = 0.05
    c: DistanceY(g1,g1) = 0.1
    c: DistanceY(g1,g0) = -0.05
    c: DistanceX(g0) = 137.5
    c: DistanceY(g0) = 137.5
    c: Coincident(g3,g2)
    c: Vertical(g3)
    c: Coincident(g4,g3)
    c: Coincident(g4,g1)
    c: Horizontal(g4)
FEATURE [Part::Loft] Loft007  label="outerLayer007"
  Closed = false
  MaxDegree = 5
  Placement = pos=(0,0,-8) rot=(0,0,1;0rad)
  Ruled = false
  Sections = -> [Sketch043,Sketch044]
  Solid = true
FEATURE [Part::Cut] Cut004  label="Shell001"
  Base = -> Loft006
  Tool = -> Loft007
FEATURE [Sketcher::SketchObject] Sketch045
  FullyConstrained = true
  Placement = pos=(0,0,0) rot=(1,0,0;1.5708rad)
  sketch-geometry (3):
    g0: LineSegment StartX=15 StartY=0 StartZ=0 EndX=260 EndY=0 EndZ=0
    g1: LineSegment StartX=260 StartY=0 StartZ=0 EndX=137.5 EndY=160 EndZ=0
    g2: LineSegment StartX=137.5 StartY=160 StartZ=0 EndX=15 EndY=0 EndZ=0
  constraints (9):
    c: Horizontal(g0)
    c: Coincident(g1,g0)
    c: Coincident(g2,g1)
    c: DistanceX(g0) = 260
    c: DistanceX(g1) = 137.5
    c: DistanceY(g1) = 160
    c: Coincident(g0,g2)
    c: DistanceY(g0,g-1) = 0
    c: DistanceX(g-1,g0) = 15
FEATURE [Part::Extrusion] Extrude014
  Base = -> Sketch045
  Dir = (0,-1,-6e-16)
  DirMode = 2
  FaceMakerClass = Part::FaceMakerBullseye
  LengthFwd = 275
  LengthRev = 0
  Placement = pos=(0,0,0) rot=(0,0,1;1.5708rad)
  Solid = true
  Symmetric = false
FEATURE [Sketcher::SketchObject] Sketch046
  FullyConstrained = true
  Placement = pos=(0,0,0) rot=(1,0,0;1.5708rad)
  sketch-geometry (3):
    g0: LineSegment StartX=15 StartY=0 StartZ=0 EndX=260 EndY=0 EndZ=0
    g1: LineSegment StartX=260 StartY=0 StartZ=0 EndX=137.5 EndY=160 EndZ=0
    g2: LineSegment StartX=137.5 StartY=160 StartZ=0 EndX=15 EndY=0 EndZ=0
  constraints (9):
    c: Horizontal(g0)
    c: Coincident(g1,g0)
    c: Coincident(g2,g1)
    c: DistanceX(g0) = 260
    c: DistanceX(g1) = 137.5
    c: DistanceY(g1) = 160
    c: Coincident(g0,g2)
    c: DistanceY(g0,g-1) = 0
    c: DistanceX(g-1,g0) = 15
FEATURE [Part::Extrusion] Extrude015
  Base = -> Sketch046
  Dir = (0,-1,2e-16)
  DirMode = 2
  FaceMakerClass = Part::FaceMakerBullseye
  LengthFwd = 275
  LengthRev = 0
  Reversed = true
  Solid = true
  Symmetric = false
FEATURE [Part::MultiCommon] Common003  label="cuts002"
  Shapes = -> [Extrude014,Extrude012]
FEATURE [Part::MultiCommon] Common004  label="cuts003"
  Shapes = -> [Extrude015,Extrude013]
FEATURE [Part::MultiFuse] Fusion059  label="cuts004"
  Shapes = -> [Common004,Common003]
FEATURE [Sketcher::SketchObject] Sketch047
  FullyConstrained = true
  Placement = pos=(0,0,0) rot=(1,0,0;1.5708rad)
  sketch-geometry (28):
    g0: LineSegment StartX=50 StartY=70 StartZ=0 EndX=97.5 EndY=97.4241 EndZ=0
    g1: LineSegment StartX=97.5 StartY=97.4241 StartZ=0 EndX=97.5 EndY=101.424 EndZ=0
    g2: LineSegment StartX=97.5 StartY=101.424 StartZ=0 EndX=50 EndY=74 EndZ=0
    g3: LineSegment StartX=50 StartY=74 StartZ=0 EndX=50 EndY=70 EndZ=0
    g4: LineSegment StartX=50 StartY=82 StartZ=0 EndX=97.5 EndY=109.424 EndZ=0
    g5: LineSegment StartX=97.5 StartY=109.424 StartZ=0 EndX=97.5 EndY=105.424 EndZ=0
    g6: LineSegment StartX=97.5 StartY=105.424 StartZ=0 EndX=50 EndY=78 EndZ=0
    g7: LineSegment StartX=50 StartY=82 StartZ=0 EndX=50 EndY=78 EndZ=0
    g8: LineSegment StartX=75 StartY=116.424 StartZ=0 EndX=137.5 EndY=152.509 EndZ=0
    g9: LineSegment StartX=137.5 StartY=148.509 StartZ=0 EndX=75 EndY=112.424 EndZ=0
    g10: LineSegment StartX=75 StartY=112.424 StartZ=0 EndX=75 EndY=116.424 EndZ=0
    g11: LineSegment StartX=137.5 StartY=152.509 StartZ=0 EndX=200 EndY=116.424 EndZ=0
    g12: LineSegment StartX=200 StartY=116.424 StartZ=0 EndX=200 EndY=112.424 EndZ=0
    g13: LineSegment StartX=200 StartY=112.424 StartZ=0 EndX=137.5 EndY=148.509 EndZ=0
    g14: LineSegment StartX=177.5 StartY=109.424 StartZ=0 EndX=225 EndY=82 EndZ=0
    g15: LineSegment StartX=225 StartY=82 StartZ=0 EndX=225 EndY=78 EndZ=0
    g16: LineSegment StartX=225 StartY=78 StartZ=0 EndX=177.5 EndY=105.424 EndZ=0
    g17: LineSegment StartX=177.5 StartY=105.424 StartZ=0 EndX=177.5 EndY=109.424 EndZ=0
    g18: LineSegment StartX=177.5 StartY=101.424 StartZ=0 EndX=225 EndY=74 EndZ=0
    g19: LineSegment StartX=225 StartY=74 StartZ=0 EndX=225 EndY=70 EndZ=0
    g20: LineSegment StartX=225 StartY=70 StartZ=0 EndX=177.5 EndY=97.4241 EndZ=0
    g21: LineSegment StartX=177.5 StartY=101.424 StartZ=0 EndX=177.5 EndY=97.4241 EndZ=0
    g22: LineSegment StartX=75 StartY=120.424 StartZ=0 EndX=137.5 EndY=156.509 EndZ=0
    g23: LineSegment StartX=137.5 StartY=156.509 StartZ=0 EndX=200 EndY=120.424 EndZ=0
    g24: LineSegment StartX=200 StartY=120.424 StartZ=0 EndX=200 EndY=124.424 EndZ=0
    g25: LineSegment StartX=200 StartY=124.424 StartZ=0 EndX=137.5 EndY=160.509 EndZ=0
    g26: LineSegment StartX=137.5 StartY=160.509 StartZ=0 EndX=75 EndY=124.424 EndZ=0
    g27: LineSegment StartX=75 StartY=124.424 StartZ=0 EndX=75 EndY=120.424 EndZ=0
  constraints (84):
    c: Angle(g0) = 0.523599
    c: DistanceX(g0) = 50
    c: Coincident(g1,g0)
    c: Vertical(g1)
    c: Coincident(g2,g1)
    c: Coincident(g3,g2)
    c: Vertical(g3)
    c: DistanceY(g0,g2) = 4
    c: Parallel(g0,g2)
    c: Coincident(g0,g3)
    c: Coincident(g5,g4)
    c: Coincident(g7,g4)
    c: Coincident(g7,g6)
    c: Vertical(g7)
    c: Vertical(g5)
    c: Coincident(g5,g6)
    c: Parallel(g2,g6)
    c: Parallel(g6,g4)
    c: DistanceX(g6,g2) = 0
    c: DistanceY(g2,g6) = 4
    c: DistanceY(g6,g4) = 4
    c: DistanceX(g5,g1) = 0
    c: DistanceY(g0) = 70
    c: Coincident(g10,g9)
    c: Coincident(g10,g8)
    c: Vertical(g10)
    c: DistanceY(g9,g8) = 4
    c: Parallel(g8,g9)
    c: DistanceX(g9,g9) = 62.5
    c: Coincident(g11,g8)
    c: Coincident(g12,g11)
    c: Coincident(g13,g12)
    c: Coincident(g13,g9)
    c: Parallel(g13,g11)
    c: Vertical(g12)
    c: Coincident(g15,g14)
    c: Vertical(g15)
    c: Coincident(g17,g16)
    c: Coincident(g17,g14)
    c: Coincident(g19,g18)
    c: Vertical(g19)
    c: Coincident(g20,g19)
    c: Coincident(g21,g18)
    c: Coincident(g21,g20)
    c: Vertical(g21)
    c: Vertical(g17)
    c: DistanceX(g18,g16) = 0
    c: DistanceY(g16,g14) = 4
    c: DistanceY(g18,g16) = 4
    c: DistanceY(g20,g18) = 4
    c: Parallel(g20,g18)
    c: Parallel(g18,g16)
    c: Parallel(g16,g14)
    c: Coincident(g15,g16)
    c: DistanceY(g19,g0) = 0
    c: DistanceX(g18,g15) = 0
    c: DistanceY(g4,g9) = 3
    c: DistanceY(g4,g14) = 0
    c: DistanceY(g9,g12) = 0
    c: DistanceX(g9,g8) = 0
    c: Angle(g9) = -2.61799
    c: DistanceX(g9,g4) = 22.5
    c: DistanceX(g14,g12) = 22.5
    c: DistanceX(g9,g14) = 87.5
    c: DistanceX(g8) = 137.5
    c: DistanceX(g9,g12) = 125
    c: Coincident(g23,g22)
    c: Coincident(g24,g23)
    c: Vertical(g24)
    c: Coincident(g26,g25)
    c: Coincident(g27,g22)
    c: Vertical(g27)
    c: DistanceX(g22,g8) = 0
    c: DistanceX(g8,g22) = 0
    c: DistanceX(g25,g22) = 0
    c: Coincident(g24,g25)
    c: Coincident(g26,g27)
    c: DistanceY(g8,g22) = 4
    c: DistanceY(g22,g25) = 4
    c: DistanceY(g11,g23) = 4
    c: DistanceY(g23,g24) = 4
    c: DistanceX(g23,g11) = 0
    c: DistanceY(g8,g22) = 4
    c: DistanceY(g22,g26) = 4
FEATURE [Part::Extrusion] Extrude016  label="cuts007"
  Base = -> Sketch047
  Dir = (0,-1,2e-16)
  DirMode = 2
  FaceMakerClass = Part::FaceMakerBullseye
  LengthFwd = 275
  LengthRev = 0
  Reversed = true
  Solid = true
  Symmetric = false
FEATURE [Sketcher::SketchObject] Sketch048
  FullyConstrained = true
  Placement = pos=(0,0,0) rot=(1,0,0;1.5708rad)
  sketch-geometry (28):
    g0: LineSegment StartX=50 StartY=70 StartZ=0 EndX=97.5 EndY=97.4241 EndZ=0
    g1: LineSegment StartX=97.5 StartY=97.4241 StartZ=0 EndX=97.5 EndY=101.424 EndZ=0
    g2: LineSegment StartX=97.5 StartY=101.424 StartZ=0 EndX=50 EndY=74 EndZ=0
    g3: LineSegment StartX=50 StartY=74 StartZ=0 EndX=50 EndY=70 EndZ=0
    g4: LineSegment StartX=50 StartY=82 StartZ=0 EndX=97.5 EndY=109.424 EndZ=0
    g5: LineSegment StartX=97.5 StartY=109.424 StartZ=0 EndX=97.5 EndY=105.424 EndZ=0
    g6: LineSegment StartX=97.5 StartY=105.424 StartZ=0 EndX=50 EndY=78 EndZ=0
    g7: LineSegment StartX=50 StartY=82 StartZ=0 EndX=50 EndY=78 EndZ=0
    g8: LineSegment StartX=75 StartY=116.424 StartZ=0 EndX=137.5 EndY=152.509 EndZ=0
    g9: LineSegment StartX=137.5 StartY=148.509 StartZ=0 EndX=75 EndY=112.424 EndZ=0
    g10: LineSegment StartX=75 StartY=112.424 StartZ=0 EndX=75 EndY=116.424 EndZ=0
    g11: LineSegment StartX=137.5 StartY=152.509 StartZ=0 EndX=200 EndY=116.424 EndZ=0
    g12: LineSegment StartX=200 StartY=116.424 StartZ=0 EndX=200 EndY=112.424 EndZ=0
    g13: LineSegment StartX=200 StartY=112.424 StartZ=0 EndX=137.5 EndY=148.509 EndZ=0
    g14: LineSegment StartX=177.5 StartY=109.424 StartZ=0 EndX=225 EndY=82 EndZ=0
    g15: LineSegment StartX=225 StartY=82 StartZ=0 EndX=225 EndY=78 EndZ=0
    g16: LineSegment StartX=225 StartY=78 StartZ=0 EndX=177.5 EndY=105.424 EndZ=0
    g17: LineSegment StartX=177.5 StartY=105.424 StartZ=0 EndX=177.5 EndY=109.424 EndZ=0
    g18: LineSegment StartX=177.5 StartY=101.424 StartZ=0 EndX=225 EndY=74 EndZ=0
    g19: LineSegment StartX=225 StartY=74 StartZ=0 EndX=225 EndY=70 EndZ=0
    g20: LineSegment StartX=225 StartY=70 StartZ=0 EndX=177.5 EndY=97.4241 EndZ=0
    g21: LineSegment StartX=177.5 StartY=101.424 StartZ=0 EndX=177.5 EndY=97.4241 EndZ=0
    g22: LineSegment StartX=75 StartY=120.424 StartZ=0 EndX=75 EndY=124.424 EndZ=0
    g23: LineSegment StartX=75 StartY=124.424 StartZ=0 EndX=137.5 EndY=160.509 EndZ=0
    g24: LineSegment StartX=137.5 StartY=160.509 StartZ=0 EndX=200 EndY=124.424 EndZ=0
    g25: LineSegment StartX=200 StartY=124.424 StartZ=0 EndX=200 EndY=120.424 EndZ=0
    g26: LineSegment StartX=200 StartY=120.424 StartZ=0 EndX=137.5 EndY=156.509 EndZ=0
    g27: LineSegment StartX=137.5 StartY=156.509 StartZ=0 EndX=75 EndY=120.424 EndZ=0
  constraints (84):
    c: Angle(g0) = 0.523599
    c: DistanceX(g0) = 50
    c: Coincident(g1,g0)
    c: Vertical(g1)
    c: Coincident(g2,g1)
    c: Coincident(g3,g2)
    c: Vertical(g3)
    c: DistanceY(g0,g2) = 4
    c: Parallel(g0,g2)
    c: Coincident(g0,g3)
    c: Coincident(g5,g4)
    c: Coincident(g7,g4)
    c: Coincident(g7,g6)
    c: Vertical(g7)
    c: Vertical(g5)
    c: Coincident(g5,g6)
    c: Parallel(g2,g6)
    c: Parallel(g6,g4)
    c: DistanceX(g6,g2) = 0
    c: DistanceY(g2,g6) = 4
    c: DistanceY(g6,g4) = 4
    c: DistanceX(g5,g1) = 0
    c: DistanceY(g0) = 70
    c: Coincident(g10,g9)
    c: Coincident(g10,g8)
    c: Vertical(g10)
    c: DistanceY(g9,g8) = 4
    c: Parallel(g8,g9)
    c: DistanceX(g9,g9) = 62.5
    c: Coincident(g11,g8)
    c: Coincident(g12,g11)
    c: Coincident(g13,g12)
    c: Coincident(g13,g9)
    c: Parallel(g13,g11)
    c: Vertical(g12)
    c: Coincident(g15,g14)
    c: Vertical(g15)
    c: Coincident(g17,g16)
    c: Coincident(g17,g14)
    c: Coincident(g19,g18)
    c: Vertical(g19)
    c: Coincident(g20,g19)
    c: Coincident(g21,g18)
    c: Coincident(g21,g20)
    c: Vertical(g21)
    c: Vertical(g17)
    c: DistanceX(g18,g16) = 0
    c: DistanceY(g16,g14) = 4
    c: DistanceY(g18,g16) = 4
    c: DistanceY(g20,g18) = 4
    c: Parallel(g20,g18)
    c: Parallel(g18,g16)
    c: Parallel(g16,g14)
    c: Coincident(g15,g16)
    c: DistanceY(g19,g0) = 0
    c: DistanceX(g18,g15) = 0
    c: DistanceX(g14,g14) = 47.5
    c: DistanceX(g4,g4) = 47.5
    c: DistanceX(g4,g14) = 80
    c: Parallel(g9,g4)
    c: DistanceX(g9,g8) = 0
    c: DistanceY(g4,g9) = 3
    c: DistanceY(g14,g12) = 3
    c: DistanceY(g14,g4) = 0
    c: DistanceX(g8) = 137.5
    c: DistanceX(g9,g12) = 125
    c: Vertical(g22)
    c: Coincident(g23,g22)
    c: Coincident(g24,g23)
    c: Coincident(g25,g24)
    c: Vertical(g25)
    c: Coincident(g26,g25)
    c: Coincident(g27,g22)
    c: DistanceX(g22,g8) = 0
    c: DistanceY(g8,g22) = 4
    c: DistanceY(g22,g22) = 4
    c: Coincident(g26,g27)
    c: DistanceX(g26,g8) = 0
    c: DistanceY(g26,g23) = 4
    c: DistanceY(g8,g26) = 4
    c: DistanceX(g23,g26) = 0
    c: DistanceX(g25,g11) = 0
    c: DistanceY(g11,g25) = 4
    c: DistanceY(g25,g24) = 4
FEATURE [Part::Extrusion] Extrude017  label="cuts008"
  Base = -> Sketch048
  Dir = (0,-1,2e-16)
  DirMode = 2
  FaceMakerClass = Part::FaceMakerBullseye
  LengthFwd = 275
  LengthRev = 0
  Placement = pos=(275,0,0) rot=(0,0,1;1.5708rad)
  Reversed = true
  Solid = true
  Symmetric = false
FEATURE [Sketcher::SketchObject] Sketch049
  FullyConstrained = true
  Placement = pos=(0,0,0) rot=(1,0,0;1.5708rad)
  sketch-geometry (3):
    g0: LineSegment StartX=15 StartY=0 StartZ=0 EndX=260 EndY=0 EndZ=0
    g1: LineSegment StartX=260 StartY=0 StartZ=0 EndX=137.5 EndY=160 EndZ=0
    g2: LineSegment StartX=137.5 StartY=160 StartZ=0 EndX=15 EndY=0 EndZ=0
  constraints (9):
    c: Horizontal(g0)
    c: Coincident(g1,g0)
    c: Coincident(g2,g1)
    c: DistanceX(g0) = 260
    c: DistanceX(g1) = 137.5
    c: DistanceY(g1) = 160
    c: Coincident(g0,g2)
    c: DistanceY(g0,g-1) = 0
    c: DistanceX(g-1,g0) = 15
FEATURE [Part::Extrusion] Extrude018
  Base = -> Sketch049
  Dir = (0,-1,-6e-16)
  DirMode = 2
  FaceMakerClass = Part::FaceMakerBullseye
  LengthFwd = 275
  LengthRev = 0
  Placement = pos=(0,0,0) rot=(0,0,1;1.5708rad)
  Solid = true
  Symmetric = false
FEATURE [Part::MultiCommon] Common005  label="cuts005"
  Shapes = -> [Extrude018,Extrude016]
FEATURE [Sketcher::SketchObject] Sketch050
  FullyConstrained = true
  Placement = pos=(0,0,0) rot=(1,0,0;1.5708rad)
  sketch-geometry (3):
    g0: LineSegment StartX=15 StartY=0 StartZ=0 EndX=260 EndY=0 EndZ=0
    g1: LineSegment StartX=260 StartY=0 StartZ=0 EndX=137.5 EndY=160 EndZ=0
    g2: LineSegment StartX=137.5 StartY=160 StartZ=0 EndX=15 EndY=0 EndZ=0
  constraints (9):
    c: Horizontal(g0)
    c: Coincident(g1,g0)
    c: Coincident(g2,g1)
    c: DistanceX(g0) = 260
    c: DistanceX(g1) = 137.5
    c: DistanceY(g1) = 160
    c: Coincident(g0,g2)
    c: DistanceY(g0,g-1) = 0
    c: DistanceX(g-1,g0) = 15
FEATURE [Part::Extrusion] Extrude019
  Base = -> Sketch050
  Dir = (0,-1,2e-16)
  DirMode = 2
  FaceMakerClass = Part::FaceMakerBullseye
  LengthFwd = 275
  LengthRev = 0
  Reversed = true
  Solid = true
  Symmetric = false
FEATURE [Part::MultiCommon] Common006  label="cuts006"
  Shapes = -> [Extrude019,Extrude017]
FEATURE [Part::MultiFuse] Fusion060  label="keep001"
  Placement = pos=(0,0,4) rot=(0,0,1;0rad)
  Shapes = -> [Common006,Common005]
FEATURE [Part::MultiCommon] Common007  label="keeps001"
  Shapes = -> [Loft005,Fusion060]
FEATURE [Part::MultiFuse] Fusion061  label="shell"
  Shapes = -> [Cut004,Common007]
FEATURE [Part::Cut] Cut005  label="shell001-Ref"
  Base = -> Fusion061
  Tool = -> Fusion059
FEATURE [Sketcher::SketchObject] Sketch051
  FullyConstrained = true
  sketch-geometry (4):
    g0: LineSegment StartX=0 StartY=275 StartZ=0 EndX=275 EndY=275 EndZ=0
    g1: LineSegment StartX=275 StartY=275 StartZ=0 EndX=275 EndY=0 EndZ=0
    g2: LineSegment StartX=275 StartY=0 StartZ=0 EndX=0 EndY=0 EndZ=0
    g3: LineSegment StartX=0 StartY=0 StartZ=0 EndX=0 EndY=275 EndZ=0
  constraints (11):
    c: Coincident(g0,g1)
    c: Coincident(g1,g2)
    c: Coincident(g2,g3)
    c: Coincident(g3,g0)
    c: Horizontal(g0)
    c: Horizontal(g2)
    c: Vertical(g1)
    c: Vertical(g3)
    c: Coincident(g2,g-1)
    c: DistanceX(g2,g2) = 275
    c: DistanceY(g3,g3) = 275
FEATURE [Sketcher::SketchObject] Sketch052
  FullyConstrained = true
  Placement = pos=(0,0,175.1) rot=(0,0,1;0rad)
  sketch-geometry (5):
    g0: GeomPoint X=137.5 Y=137.5 Z=0
    g1: LineSegment StartX=137.55 StartY=137.55 StartZ=0 EndX=137.55 EndY=137.45 EndZ=0
    g2: LineSegment StartX=137.55 StartY=137.45 StartZ=0 EndX=137.45 EndY=137.45 EndZ=0
    g3: LineSegment StartX=137.45 StartY=137.45 StartZ=0 EndX=137.45 EndY=137.55 EndZ=0
    g4: LineSegment StartX=137.45 StartY=137.55 StartZ=0 EndX=137.55 EndY=137.55 EndZ=0
  constraints (14):
    c: Coincident(g1,g2)
    c: Horizontal(g2)
    c: Vertical(g1)
    c: DistanceX(g2,g2) = 0.1
    c: DistanceX(g2,g0) = 0.05
    c: DistanceY(g1,g1) = 0.1
    c: DistanceY(g1,g0) = -0.05
    c: DistanceX(g0) = 137.5
    c: DistanceY(g0) = 137.5
    c: Coincident(g3,g2)
    c: Vertical(g3)
    c: Coincident(g4,g3)
    c: Coincident(g4,g1)
    c: Horizontal(g4)
FEATURE [Part::Loft] Loft008  label="outerLayer008"
  Closed = false
  MaxDegree = 5
  Ruled = false
  Sections = -> [Sketch051,Sketch052]
  Solid = true
FEATURE [Sketcher::SketchObject] Sketch053
  FullyConstrained = true
  sketch-geometry (4):
    g0: LineSegment StartX=0 StartY=275 StartZ=0 EndX=275 EndY=275 EndZ=0
    g1: LineSegment StartX=275 StartY=275 StartZ=0 EndX=275 EndY=0 EndZ=0
    g2: LineSegment StartX=275 StartY=0 StartZ=0 EndX=0 EndY=0 EndZ=0
    g3: LineSegment StartX=0 StartY=0 StartZ=0 EndX=0 EndY=275 EndZ=0
  constraints (11):
    c: Coincident(g0,g1)
    c: Coincident(g1,g2)
    c: Coincident(g2,g3)
    c: Coincident(g3,g0)
    c: Horizontal(g0)
    c: Horizontal(g2)
    c: Vertical(g1)
    c: Vertical(g3)
    c: Coincident(g2,g-1)
    c: DistanceX(g2,g2) = 275
    c: DistanceY(g3,g3) = 275
FEATURE [Sketcher::SketchObject] Sketch054
  FullyConstrained = true
  Placement = pos=(0,0,175.1) rot=(0,0,1;0rad)
  sketch-geometry (5):
    g0: GeomPoint X=137.5 Y=137.5 Z=0
    g1: LineSegment StartX=137.55 StartY=137.55 StartZ=0 EndX=137.55 EndY=137.45 EndZ=0
    g2: LineSegment StartX=137.55 StartY=137.45 StartZ=0 EndX=137.45 EndY=137.45 EndZ=0
    g3: LineSegment StartX=137.45 StartY=137.45 StartZ=0 EndX=137.45 EndY=137.55 EndZ=0
    g4: LineSegment StartX=137.45 StartY=137.55 StartZ=0 EndX=137.55 EndY=137.55 EndZ=0
  constraints (14):
    c: Coincident(g1,g2)
    c: Horizontal(g2)
    c: Vertical(g1)
    c: DistanceX(g2,g2) = 0.1
    c: DistanceX(g2,g0) = 0.05
    c: DistanceY(g1,g1) = 0.1
    c: DistanceY(g1,g0) = -0.05
    c: DistanceX(g0) = 137.5
    c: DistanceY(g0) = 137.5
    c: Coincident(g3,g2)
    c: Vertical(g3)
    c: Coincident(g4,g3)
    c: Coincident(g4,g1)
    c: Horizontal(g4)
FEATURE [Part::Loft] Loft009  label="outerLayer009"
  Closed = false
  MaxDegree = 5
  Placement = pos=(0,0,-8) rot=(0,0,1;0rad)
  Ruled = false
  Sections = -> [Sketch053,Sketch054]
  Solid = true
FEATURE [Part::Cut] Cut006  label="Shell002"
  Base = -> Loft008
  Tool = -> Loft009
FEATURE [Part::MultiCommon] Common008  label="keepLegacy"
  Shapes = -> [Fusion058,Cut006]
FEATURE [Sketcher::SketchObject] Sketch055
  FullyConstrained = true
  Placement = pos=(0,0,0) rot=(1,0,0;1.5708rad)
  sketch-geometry (28):
    g0: LineSegment StartX=50 StartY=70 StartZ=0 EndX=97.5 EndY=97.4241 EndZ=0
    g1: LineSegment StartX=97.5 StartY=97.4241 StartZ=0 EndX=97.5 EndY=101.424 EndZ=0
    g2: LineSegment StartX=97.5 StartY=101.424 StartZ=0 EndX=50 EndY=74 EndZ=0
    g3: LineSegment StartX=50 StartY=74 StartZ=0 EndX=50 EndY=70 EndZ=0
    g4: LineSegment StartX=50 StartY=82 StartZ=0 EndX=97.5 EndY=109.424 EndZ=0
    g5: LineSegment StartX=97.5 StartY=109.424 StartZ=0 EndX=97.5 EndY=105.424 EndZ=0
    g6: LineSegment StartX=97.5 StartY=105.424 StartZ=0 EndX=50 EndY=78 EndZ=0
    g7: LineSegment StartX=50 StartY=82 StartZ=0 EndX=50 EndY=78 EndZ=0
    g8: LineSegment StartX=75 StartY=116.424 StartZ=0 EndX=137.5 EndY=152.509 EndZ=0
    g9: LineSegment StartX=137.5 StartY=148.509 StartZ=0 EndX=75 EndY=112.424 EndZ=0
    g10: LineSegment StartX=75 StartY=112.424 StartZ=0 EndX=75 EndY=116.424 EndZ=0
    g11: LineSegment StartX=137.5 StartY=152.509 StartZ=0 EndX=200 EndY=116.424 EndZ=0
    g12: LineSegment StartX=200 StartY=116.424 StartZ=0 EndX=200 EndY=112.424 EndZ=0
    g13: LineSegment StartX=200 StartY=112.424 StartZ=0 EndX=137.5 EndY=148.509 EndZ=0
    g14: LineSegment StartX=177.5 StartY=109.424 StartZ=0 EndX=225 EndY=82 EndZ=0
    g15: LineSegment StartX=225 StartY=82 StartZ=0 EndX=225 EndY=78 EndZ=0
    g16: LineSegment StartX=225 StartY=78 StartZ=0 EndX=177.5 EndY=105.424 EndZ=0
    g17: LineSegment StartX=177.5 StartY=105.424 StartZ=0 EndX=177.5 EndY=109.424 EndZ=0
    g18: LineSegment StartX=177.5 StartY=101.424 StartZ=0 EndX=225 EndY=74 EndZ=0
    g19: LineSegment StartX=225 StartY=74 StartZ=0 EndX=225 EndY=70 EndZ=0
    g20: LineSegment StartX=225 StartY=70 StartZ=0 EndX=177.5 EndY=97.4241 EndZ=0
    g21: LineSegment StartX=177.5 StartY=101.424 StartZ=0 EndX=177.5 EndY=97.4241 EndZ=0
    g22: LineSegment StartX=75 StartY=120.424 StartZ=0 EndX=137.5 EndY=156.509 EndZ=0
    g23: LineSegment StartX=137.5 StartY=156.509 StartZ=0 EndX=200 EndY=120.424 EndZ=0
    g24: LineSegment StartX=200 StartY=120.424 StartZ=0 EndX=200 EndY=124.424 EndZ=0
    g25: LineSegment StartX=200 StartY=124.424 StartZ=0 EndX=137.5 EndY=160.509 EndZ=0
    g26: LineSegment StartX=137.5 StartY=160.509 StartZ=0 EndX=75 EndY=124.424 EndZ=0
    g27: LineSegment StartX=75 StartY=124.424 StartZ=0 EndX=75 EndY=120.424 EndZ=0
  constraints (84):
    c: Angle(g0) = 0.523599
    c: DistanceX(g0) = 50
    c: Coincident(g1,g0)
    c: Vertical(g1)
    c: Coincident(g2,g1)
    c: Coincident(g3,g2)
    c: Vertical(g3)
    c: DistanceY(g0,g2) = 4
    c: Parallel(g0,g2)
    c: Coincident(g0,g3)
    c: Coincident(g5,g4)
    c: Coincident(g7,g4)
    c: Coincident(g7,g6)
    c: Vertical(g7)
    c: Vertical(g5)
    c: Coincident(g5,g6)
    c: Parallel(g2,g6)
    c: Parallel(g6,g4)
    c: DistanceX(g6,g2) = 0
    c: DistanceY(g2,g6) = 4
    c: DistanceY(g6,g4) = 4
    c: DistanceX(g5,g1) = 0
    c: DistanceY(g0) = 70
    c: Coincident(g10,g9)
    c: Coincident(g10,g8)
    c: Vertical(g10)
    c: DistanceY(g9,g8) = 4
    c: Parallel(g8,g9)
    c: DistanceX(g9,g9) = 62.5
    c: Coincident(g11,g8)
    c: Coincident(g12,g11)
    c: Coincident(g13,g12)
    c: Coincident(g13,g9)
    c: Parallel(g13,g11)
    c: Vertical(g12)
    c: Coincident(g15,g14)
    c: Vertical(g15)
    c: Coincident(g17,g16)
    c: Coincident(g17,g14)
    c: Coincident(g19,g18)
    c: Vertical(g19)
    c: Coincident(g20,g19)
    c: Coincident(g21,g18)
    c: Coincident(g21,g20)
    c: Vertical(g21)
    c: Vertical(g17)
    c: DistanceX(g18,g16) = 0
    c: DistanceY(g16,g14) = 4
    c: DistanceY(g18,g16) = 4
    c: DistanceY(g20,g18) = 4
    c: Parallel(g20,g18)
    c: Parallel(g18,g16)
    c: Parallel(g16,g14)
    c: Coincident(g15,g16)
    c: DistanceY(g19,g0) = 0
    c: DistanceX(g18,g15) = 0
    c: DistanceY(g4,g9) = 3
    c: DistanceY(g4,g14) = 0
    c: DistanceY(g9,g12) = 0
    c: DistanceX(g9,g8) = 0
    c: Angle(g9) = -2.61799
    c: DistanceX(g9,g4) = 22.5
    c: DistanceX(g14,g12) = 22.5
    c: DistanceX(g9,g14) = 87.5
    c: DistanceX(g8) = 137.5
    c: DistanceX(g9,g12) = 125
    c: Coincident(g23,g22)
    c: Coincident(g24,g23)
    c: Vertical(g24)
    c: Coincident(g26,g25)
    c: Coincident(g27,g22)
    c: Vertical(g27)
    c: DistanceX(g22,g8) = 0
    c: DistanceX(g8,g22) = 0
    c: DistanceX(g25,g22) = 0
    c: Coincident(g24,g25)
    c: Coincident(g26,g27)
    c: DistanceY(g8,g22) = 4
    c: DistanceY(g22,g25) = 4
    c: DistanceY(g11,g23) = 4
    c: DistanceY(g23,g24) = 4
    c: DistanceX(g23,g11) = 0
    c: DistanceY(g8,g22) = 4
    c: DistanceY(g22,g26) = 4
FEATURE [Part::Extrusion] Extrude020  label="cuts011"
  Base = -> Sketch055
  Dir = (0,-1,2e-16)
  DirMode = 2
  FaceMakerClass = Part::FaceMakerBullseye
  LengthFwd = 275
  LengthRev = 0
  Reversed = true
  Solid = true
  Symmetric = false
FEATURE [Sketcher::SketchObject] Sketch056
  FullyConstrained = true
  Placement = pos=(0,0,0) rot=(1,0,0;1.5708rad)
  sketch-geometry (28):
    g0: LineSegment StartX=50 StartY=70 StartZ=0 EndX=97.5 EndY=97.4241 EndZ=0
    g1: LineSegment StartX=97.5 StartY=97.4241 StartZ=0 EndX=97.5 EndY=101.424 EndZ=0
    g2: LineSegment StartX=97.5 StartY=101.424 StartZ=0 EndX=50 EndY=74 EndZ=0
    g3: LineSegment StartX=50 StartY=74 StartZ=0 EndX=50 EndY=70 EndZ=0
    g4: LineSegment StartX=50 StartY=82 StartZ=0 EndX=97.5 EndY=109.424 EndZ=0
    g5: LineSegment StartX=97.5 StartY=109.424 StartZ=0 EndX=97.5 EndY=105.424 EndZ=0
    g6: LineSegment StartX=97.5 StartY=105.424 StartZ=0 EndX=50 EndY=78 EndZ=0
    g7: LineSegment StartX=50 StartY=82 StartZ=0 EndX=50 EndY=78 EndZ=0
    g8: LineSegment StartX=75 StartY=116.424 StartZ=0 EndX=137.5 EndY=152.509 EndZ=0
    g9: LineSegment StartX=137.5 StartY=148.509 StartZ=0 EndX=75 EndY=112.424 EndZ=0
    g10: LineSegment StartX=75 StartY=112.424 StartZ=0 EndX=75 EndY=116.424 EndZ=0
    g11: LineSegment StartX=137.5 StartY=152.509 StartZ=0 EndX=200 EndY=116.424 EndZ=0
    g12: LineSegment StartX=200 StartY=116.424 StartZ=0 EndX=200 EndY=112.424 EndZ=0
    g13: LineSegment StartX=200 StartY=112.424 StartZ=0 EndX=137.5 EndY=148.509 EndZ=0
    g14: LineSegment StartX=177.5 StartY=109.424 StartZ=0 EndX=225 EndY=82 EndZ=0
    g15: LineSegment StartX=225 StartY=82 StartZ=0 EndX=225 EndY=78 EndZ=0
    g16: LineSegment StartX=225 StartY=78 StartZ=0 EndX=177.5 EndY=105.424 EndZ=0
    g17: LineSegment StartX=177.5 StartY=105.424 StartZ=0 EndX=177.5 EndY=109.424 EndZ=0
    g18: LineSegment StartX=177.5 StartY=101.424 StartZ=0 EndX=225 EndY=74 EndZ=0
    g19: LineSegment StartX=225 StartY=74 StartZ=0 EndX=225 EndY=70 EndZ=0
    g20: LineSegment StartX=225 StartY=70 StartZ=0 EndX=177.5 EndY=97.4241 EndZ=0
    g21: LineSegment StartX=177.5 StartY=101.424 StartZ=0 EndX=177.5 EndY=97.4241 EndZ=0
    g22: LineSegment StartX=75 StartY=120.424 StartZ=0 EndX=75 EndY=124.424 EndZ=0
    g23: LineSegment StartX=75 StartY=124.424 StartZ=0 EndX=137.5 EndY=160.509 EndZ=0
    g24: LineSegment StartX=137.5 StartY=160.509 StartZ=0 EndX=200 EndY=124.424 EndZ=0
    g25: LineSegment StartX=200 StartY=124.424 StartZ=0 EndX=200 EndY=120.424 EndZ=0
    g26: LineSegment StartX=200 StartY=120.424 StartZ=0 EndX=137.5 EndY=156.509 EndZ=0
    g27: LineSegment StartX=137.5 StartY=156.509 StartZ=0 EndX=75 EndY=120.424 EndZ=0
  constraints (84):
    c: Angle(g0) = 0.523599
    c: DistanceX(g0) = 50
    c: Coincident(g1,g0)
    c: Vertical(g1)
    c: Coincident(g2,g1)
    c: Coincident(g3,g2)
    c: Vertical(g3)
    c: DistanceY(g0,g2) = 4
    c: Parallel(g0,g2)
    c: Coincident(g0,g3)
    c: Coincident(g5,g4)
    c: Coincident(g7,g4)
    c: Coincident(g7,g6)
    c: Vertical(g7)
    c: Vertical(g5)
    c: Coincident(g5,g6)
    c: Parallel(g2,g6)
    c: Parallel(g6,g4)
    c: DistanceX(g6,g2) = 0
    c: DistanceY(g2,g6) = 4
    c: DistanceY(g6,g4) = 4
    c: DistanceX(g5,g1) = 0
    c: DistanceY(g0) = 70
    c: Coincident(g10,g9)
    c: Coincident(g10,g8)
    c: Vertical(g10)
    c: DistanceY(g9,g8) = 4
    c: Parallel(g8,g9)
    c: DistanceX(g9,g9) = 62.5
    c: Coincident(g11,g8)
    c: Coincident(g12,g11)
    c: Coincident(g13,g12)
    c: Coincident(g13,g9)
    c: Parallel(g13,g11)
    c: Vertical(g12)
    c: Coincident(g15,g14)
    c: Vertical(g15)
    c: Coincident(g17,g16)
    c: Coincident(g17,g14)
    c: Coincident(g19,g18)
    c: Vertical(g19)
    c: Coincident(g20,g19)
    c: Coincident(g21,g18)
    c: Coincident(g21,g20)
    c: Vertical(g21)
    c: Vertical(g17)
    c: DistanceX(g18,g16) = 0
    c: DistanceY(g16,g14) = 4
    c: DistanceY(g18,g16) = 4
    c: DistanceY(g20,g18) = 4
    c: Parallel(g20,g18)
    c: Parallel(g18,g16)
    c: Parallel(g16,g14)
    c: Coincident(g15,g16)
    c: DistanceY(g19,g0) = 0
    c: DistanceX(g18,g15) = 0
    c: DistanceX(g14,g14) = 47.5
    c: DistanceX(g4,g4) = 47.5
    c: DistanceX(g4,g14) = 80
    c: Parallel(g9,g4)
    c: DistanceX(g9,g8) = 0
    c: DistanceY(g4,g9) = 3
    c: DistanceY(g14,g12) = 3
    c: DistanceY(g14,g4) = 0
    c: DistanceX(g8) = 137.5
    c: DistanceX(g9,g12) = 125
    c: Vertical(g22)
    c: Coincident(g23,g22)
    c: Coincident(g24,g23)
    c: Coincident(g25,g24)
    c: Vertical(g25)
    c: Coincident(g26,g25)
    c: Coincident(g27,g22)
    c: DistanceX(g22,g8) = 0
    c: DistanceY(g8,g22) = 4
    c: DistanceY(g22,g22) = 4
    c: Coincident(g26,g27)
    c: DistanceX(g26,g8) = 0
    c: DistanceY(g26,g23) = 4
    c: DistanceY(g8,g26) = 4
    c: DistanceX(g23,g26) = 0
    c: DistanceX(g25,g11) = 0
    c: DistanceY(g11,g25) = 4
    c: DistanceY(g25,g24) = 4
FEATURE [Part::Extrusion] Extrude021  label="cuts012"
  Base = -> Sketch056
  Dir = (0,-1,2e-16)
  DirMode = 2
  FaceMakerClass = Part::FaceMakerBullseye
  LengthFwd = 275
  LengthRev = 0
  Placement = pos=(275,0,0) rot=(0,0,1;1.5708rad)
  Reversed = true
  Solid = true
  Symmetric = false
FEATURE [Sketcher::SketchObject] Sketch057
  FullyConstrained = true
  Placement = pos=(0,0,0) rot=(1,0,0;1.5708rad)
  sketch-geometry (3):
    g0: LineSegment StartX=15 StartY=0 StartZ=0 EndX=260 EndY=0 EndZ=0
    g1: LineSegment StartX=260 StartY=0 StartZ=0 EndX=137.5 EndY=160 EndZ=0
    g2: LineSegment StartX=137.5 StartY=160 StartZ=0 EndX=15 EndY=0 EndZ=0
  constraints (9):
    c: Horizontal(g0)
    c: Coincident(g1,g0)
    c: Coincident(g2,g1)
    c: DistanceX(g0) = 260
    c: DistanceX(g1) = 137.5
    c: DistanceY(g1) = 160
    c: Coincident(g0,g2)
    c: DistanceY(g0,g-1) = 0
    c: DistanceX(g-1,g0) = 15
FEATURE [Part::Extrusion] Extrude022
  Base = -> Sketch057
  Dir = (0,-1,-6e-16)
  DirMode = 2
  FaceMakerClass = Part::FaceMakerBullseye
  LengthFwd = 275
  LengthRev = 0
  Placement = pos=(0,0,0) rot=(0,0,1;1.5708rad)
  Solid = true
  Symmetric = false
FEATURE [Part::MultiCommon] Common009  label="cuts009"
  Shapes = -> [Extrude022,Extrude020]
FEATURE [Sketcher::SketchObject] Sketch058
  FullyConstrained = true
  Placement = pos=(0,0,0) rot=(1,0,0;1.5708rad)
  sketch-geometry (3):
    g0: LineSegment StartX=15 StartY=0 StartZ=0 EndX=260 EndY=0 EndZ=0
    g1: LineSegment StartX=260 StartY=0 StartZ=0 EndX=137.5 EndY=160 EndZ=0
    g2: LineSegment StartX=137.5 StartY=160 StartZ=0 EndX=15 EndY=0 EndZ=0
  constraints (9):
    c: Horizontal(g0)
    c: Coincident(g1,g0)
    c: Coincident(g2,g1)
    c: DistanceX(g0) = 260
    c: DistanceX(g1) = 137.5
    c: DistanceY(g1) = 160
    c: Coincident(g0,g2)
    c: DistanceY(g0,g-1) = 0
    c: DistanceX(g-1,g0) = 15
FEATURE [Part::Extrusion] Extrude023
  Base = -> Sketch058
  Dir = (0,-1,2e-16)
  DirMode = 2
  FaceMakerClass = Part::FaceMakerBullseye
  LengthFwd = 275
  LengthRev = 0
  Reversed = true
  Solid = true
  Symmetric = false
FEATURE [Part::MultiCommon] Common010  label="cuts010"
  Shapes = -> [Extrude023,Extrude021]
FEATURE [Part::MultiFuse] Fusion062  label="cuts013"
  Shapes = -> [Common010,Common009]
FEATURE [Sketcher::SketchObject] Sketch059
  FullyConstrained = true
  sketch-geometry (4):
    g0: LineSegment StartX=0 StartY=275 StartZ=0 EndX=275 EndY=275 EndZ=0
    g1: LineSegment StartX=275 StartY=275 StartZ=0 EndX=275 EndY=0 EndZ=0
    g2: LineSegment StartX=275 StartY=0 StartZ=0 EndX=0 EndY=0 EndZ=0
    g3: LineSegment StartX=0 StartY=0 StartZ=0 EndX=0 EndY=275 EndZ=0
  constraints (11):
    c: Coincident(g0,g1)
    c: Coincident(g1,g2)
    c: Coincident(g2,g3)
    c: Coincident(g3,g0)
    c: Horizontal(g0)
    c: Horizontal(g2)
    c: Vertical(g1)
    c: Vertical(g3)
    c: Coincident(g2,g-1)
    c: DistanceX(g2,g2) = 275
    c: DistanceY(g3,g3) = 275
FEATURE [Sketcher::SketchObject] Sketch060
  FullyConstrained = true
  Placement = pos=(0,0,175.1) rot=(0,0,1;0rad)
  sketch-geometry (5):
    g0: GeomPoint X=137.5 Y=137.5 Z=0
    g1: LineSegment StartX=137.55 StartY=137.55 StartZ=0 EndX=137.55 EndY=137.45 EndZ=0
    g2: LineSegment StartX=137.55 StartY=137.45 StartZ=0 EndX=137.45 EndY=137.45 EndZ=0
    g3: LineSegment StartX=137.45 StartY=137.45 StartZ=0 EndX=137.45 EndY=137.55 EndZ=0
    g4: LineSegment StartX=137.45 StartY=137.55 StartZ=0 EndX=137.55 EndY=137.55 EndZ=0
  constraints (14):
    c: Coincident(g1,g2)
    c: Horizontal(g2)
    c: Vertical(g1)
    c: DistanceX(g2,g2) = 0.1
    c: DistanceX(g2,g0) = 0.05
    c: DistanceY(g1,g1) = 0.1
    c: DistanceY(g1,g0) = -0.05
    c: DistanceX(g0) = 137.5
    c: DistanceY(g0) = 137.5
    c: Coincident(g3,g2)
    c: Vertical(g3)
    c: Coincident(g4,g3)
    c: Coincident(g4,g1)
    c: Horizontal(g4)
FEATURE [Part::Loft] Loft010  label="outerLayer010"
  Closed = false
  MaxDegree = 5
  Ruled = false
  Sections = -> [Sketch059,Sketch060]
  Solid = true
FEATURE [Sketcher::SketchObject] Sketch061
  FullyConstrained = true
  sketch-geometry (4):
    g0: LineSegment StartX=0 StartY=275 StartZ=0 EndX=275 EndY=275 EndZ=0
    g1: LineSegment StartX=275 StartY=275 StartZ=0 EndX=275 EndY=0 EndZ=0
    g2: LineSegment StartX=275 StartY=0 StartZ=0 EndX=0 EndY=0 EndZ=0
    g3: LineSegment StartX=0 StartY=0 StartZ=0 EndX=0 EndY=275 EndZ=0
  constraints (11):
    c: Coincident(g0,g1)
    c: Coincident(g1,g2)
    c: Coincident(g2,g3)
    c: Coincident(g3,g0)
    c: Horizontal(g0)
    c: Horizontal(g2)
    c: Vertical(g1)
    c: Vertical(g3)
    c: Coincident(g2,g-1)
    c: DistanceX(g2,g2) = 275
    c: DistanceY(g3,g3) = 275
FEATURE [Sketcher::SketchObject] Sketch062
  FullyConstrained = true
  Placement = pos=(0,0,175.1) rot=(0,0,1;0rad)
  sketch-geometry (5):
    g0: GeomPoint X=137.5 Y=137.5 Z=0
    g1: LineSegment StartX=137.55 StartY=137.55 StartZ=0 EndX=137.55 EndY=137.45 EndZ=0
    g2: LineSegment StartX=137.55 StartY=137.45 StartZ=0 EndX=137.45 EndY=137.45 EndZ=0
    g3: LineSegment StartX=137.45 StartY=137.45 StartZ=0 EndX=137.45 EndY=137.55 EndZ=0
    g4: LineSegment StartX=137.45 StartY=137.55 StartZ=0 EndX=137.55 EndY=137.55 EndZ=0
  constraints (14):
    c: Coincident(g1,g2)
    c: Horizontal(g2)
    c: Vertical(g1)
    c: DistanceX(g2,g2) = 0.1
    c: DistanceX(g2,g0) = 0.05
    c: DistanceY(g1,g1) = 0.1
    c: DistanceY(g1,g0) = -0.05
    c: DistanceX(g0) = 137.5
    c: DistanceY(g0) = 137.5
    c: Coincident(g3,g2)
    c: Vertical(g3)
    c: Coincident(g4,g3)
    c: Coincident(g4,g1)
    c: Horizontal(g4)
FEATURE [Part::Loft] Loft011  label="outerLayer011"
  Closed = false
  MaxDegree = 5
  Ruled = false
  Sections = -> [Sketch061,Sketch062]
  Solid = true
FEATURE [Sketcher::SketchObject] Sketch063
  FullyConstrained = true
  sketch-geometry (4):
    g0: LineSegment StartX=0 StartY=275 StartZ=0 EndX=275 EndY=275 EndZ=0
    g1: LineSegment StartX=275 StartY=275 StartZ=0 EndX=275 EndY=0 EndZ=0
    g2: LineSegment StartX=275 StartY=0 StartZ=0 EndX=0 EndY=0 EndZ=0
    g3: LineSegment StartX=0 StartY=0 StartZ=0 EndX=0 EndY=275 EndZ=0
  constraints (11):
    c: Coincident(g0,g1)
    c: Coincident(g1,g2)
    c: Coincident(g2,g3)
    c: Coincident(g3,g0)
    c: Horizontal(g0)
    c: Horizontal(g2)
    c: Vertical(g1)
    c: Vertical(g3)
    c: Coincident(g2,g-1)
    c: DistanceX(g2,g2) = 275
    c: DistanceY(g3,g3) = 275
FEATURE [Sketcher::SketchObject] Sketch064
  FullyConstrained = true
  Placement = pos=(0,0,175.1) rot=(0,0,1;0rad)
  sketch-geometry (5):
    g0: GeomPoint X=137.5 Y=137.5 Z=0
    g1: LineSegment StartX=137.55 StartY=137.55 StartZ=0 EndX=137.55 EndY=137.45 EndZ=0
    g2: LineSegment StartX=137.55 StartY=137.45 StartZ=0 EndX=137.45 EndY=137.45 EndZ=0
    g3: LineSegment StartX=137.45 StartY=137.45 StartZ=0 EndX=137.45 EndY=137.55 EndZ=0
    g4: LineSegment StartX=137.45 StartY=137.55 StartZ=0 EndX=137.55 EndY=137.55 EndZ=0
  constraints (14):
    c: Coincident(g1,g2)
    c: Horizontal(g2)
    c: Vertical(g1)
    c: DistanceX(g2,g2) = 0.1
    c: DistanceX(g2,g0) = 0.05
    c: DistanceY(g1,g1) = 0.1
    c: DistanceY(g1,g0) = -0.05
    c: DistanceX(g0) = 137.5
    c: DistanceY(g0) = 137.5
    c: Coincident(g3,g2)
    c: Vertical(g3)
    c: Coincident(g4,g3)
    c: Coincident(g4,g1)
    c: Horizontal(g4)
FEATURE [Part::Loft] Loft012  label="outerLayer012"
  Closed = false
  MaxDegree = 5
  Placement = pos=(0,0,-8) rot=(0,0,1;0rad)
  Ruled = false
  Sections = -> [Sketch063,Sketch064]
  Solid = true
FEATURE [Part::Cut] Cut007  label="Shell003"
  Base = -> Loft011
  Tool = -> Loft012
FEATURE [Sketcher::SketchObject] Sketch065
  FullyConstrained = true
  Placement = pos=(0,0,0) rot=(1,0,0;1.5708rad)
  sketch-geometry (28):
    g0: LineSegment StartX=50 StartY=70 StartZ=0 EndX=97.5 EndY=97.4241 EndZ=0
    g1: LineSegment StartX=97.5 StartY=97.4241 StartZ=0 EndX=97.5 EndY=101.424 EndZ=0
    g2: LineSegment StartX=97.5 StartY=101.424 StartZ=0 EndX=50 EndY=74 EndZ=0
    g3: LineSegment StartX=50 StartY=74 StartZ=0 EndX=50 EndY=70 EndZ=0
    g4: LineSegment StartX=50 StartY=82 StartZ=0 EndX=97.5 EndY=109.424 EndZ=0
    g5: LineSegment StartX=97.5 StartY=109.424 StartZ=0 EndX=97.5 EndY=105.424 EndZ=0
    g6: LineSegment StartX=97.5 StartY=105.424 StartZ=0 EndX=50 EndY=78 EndZ=0
    g7: LineSegment StartX=50 StartY=82 StartZ=0 EndX=50 EndY=78 EndZ=0
    g8: LineSegment StartX=75 StartY=116.424 StartZ=0 EndX=137.5 EndY=152.509 EndZ=0
    g9: LineSegment StartX=137.5 StartY=148.509 StartZ=0 EndX=75 EndY=112.424 EndZ=0
    g10: LineSegment StartX=75 StartY=112.424 StartZ=0 EndX=75 EndY=116.424 EndZ=0
    g11: LineSegment StartX=137.5 StartY=152.509 StartZ=0 EndX=200 EndY=116.424 EndZ=0
    g12: LineSegment StartX=200 StartY=116.424 StartZ=0 EndX=200 EndY=112.424 EndZ=0
    g13: LineSegment StartX=200 StartY=112.424 StartZ=0 EndX=137.5 EndY=148.509 EndZ=0
    g14: LineSegment StartX=177.5 StartY=109.424 StartZ=0 EndX=225 EndY=82 EndZ=0
    g15: LineSegment StartX=225 StartY=82 StartZ=0 EndX=225 EndY=78 EndZ=0
    g16: LineSegment StartX=225 StartY=78 StartZ=0 EndX=177.5 EndY=105.424 EndZ=0
    g17: LineSegment StartX=177.5 StartY=105.424 StartZ=0 EndX=177.5 EndY=109.424 EndZ=0
    g18: LineSegment StartX=177.5 StartY=101.424 StartZ=0 EndX=225 EndY=74 EndZ=0
    g19: LineSegment StartX=225 StartY=74 StartZ=0 EndX=225 EndY=70 EndZ=0
    g20: LineSegment StartX=225 StartY=70 StartZ=0 EndX=177.5 EndY=97.4241 EndZ=0
    g21: LineSegment StartX=177.5 StartY=101.424 StartZ=0 EndX=177.5 EndY=97.4241 EndZ=0
    g22: LineSegment StartX=75 StartY=120.424 StartZ=0 EndX=137.5 EndY=156.509 EndZ=0
    g23: LineSegment StartX=137.5 StartY=156.509 StartZ=0 EndX=200 EndY=120.424 EndZ=0
    g24: LineSegment StartX=200 StartY=120.424 StartZ=0 EndX=200 EndY=124.424 EndZ=0
    g25: LineSegment StartX=200 StartY=124.424 StartZ=0 EndX=137.5 EndY=160.509 EndZ=0
    g26: LineSegment StartX=137.5 StartY=160.509 StartZ=0 EndX=75 EndY=124.424 EndZ=0
    g27: LineSegment StartX=75 StartY=124.424 StartZ=0 EndX=75 EndY=120.424 EndZ=0
  constraints (84):
    c: Angle(g0) = 0.523599
    c: DistanceX(g0) = 50
    c: Coincident(g1,g0)
    c: Vertical(g1)
    c: Coincident(g2,g1)
    c: Coincident(g3,g2)
    c: Vertical(g3)
    c: DistanceY(g0,g2) = 4
    c: Parallel(g0,g2)
    c: Coincident(g0,g3)
    c: Coincident(g5,g4)
    c: Coincident(g7,g4)
    c: Coincident(g7,g6)
    c: Vertical(g7)
    c: Vertical(g5)
    c: Coincident(g5,g6)
    c: Parallel(g2,g6)
    c: Parallel(g6,g4)
    c: DistanceX(g6,g2) = 0
    c: DistanceY(g2,g6) = 4
    c: DistanceY(g6,g4) = 4
    c: DistanceX(g5,g1) = 0
    c: DistanceY(g0) = 70
    c: Coincident(g10,g9)
    c: Coincident(g10,g8)
    c: Vertical(g10)
    c: DistanceY(g9,g8) = 4
    c: Parallel(g8,g9)
    c: DistanceX(g9,g9) = 62.5
    c: Coincident(g11,g8)
    c: Coincident(g12,g11)
    c: Coincident(g13,g12)
    c: Coincident(g13,g9)
    c: Parallel(g13,g11)
    c: Vertical(g12)
    c: Coincident(g15,g14)
    c: Vertical(g15)
    c: Coincident(g17,g16)
    c: Coincident(g17,g14)
    c: Coincident(g19,g18)
    c: Vertical(g19)
    c: Coincident(g20,g19)
    c: Coincident(g21,g18)
    c: Coincident(g21,g20)
    c: Vertical(g21)
    c: Vertical(g17)
    c: DistanceX(g18,g16) = 0
    c: DistanceY(g16,g14) = 4
    c: DistanceY(g18,g16) = 4
    c: DistanceY(g20,g18) = 4
    c: Parallel(g20,g18)
    c: Parallel(g18,g16)
    c: Parallel(g16,g14)
    c: Coincident(g15,g16)
    c: DistanceY(g19,g0) = 0
    c: DistanceX(g18,g15) = 0
    c: DistanceY(g4,g9) = 3
    c: DistanceY(g4,g14) = 0
    c: DistanceY(g9,g12) = 0
    c: DistanceX(g9,g8) = 0
    c: Angle(g9) = -2.61799
    c: DistanceX(g9,g4) = 22.5
    c: DistanceX(g14,g12) = 22.5
    c: DistanceX(g9,g14) = 87.5
    c: DistanceX(g8) = 137.5
    c: DistanceX(g9,g12) = 125
    c: Coincident(g23,g22)
    c: Coincident(g24,g23)
    c: Vertical(g24)
    c: Coincident(g26,g25)
    c: Coincident(g27,g22)
    c: Vertical(g27)
    c: DistanceX(g22,g8) = 0
    c: DistanceX(g8,g22) = 0
    c: DistanceX(g25,g22) = 0
    c: Coincident(g24,g25)
    c: Coincident(g26,g27)
    c: DistanceY(g8,g22) = 4
    c: DistanceY(g22,g25) = 4
    c: DistanceY(g11,g23) = 4
    c: DistanceY(g23,g24) = 4
    c: DistanceX(g23,g11) = 0
    c: DistanceY(g8,g22) = 4
    c: DistanceY(g22,g26) = 4
FEATURE [Part::Extrusion] Extrude024  label="cuts016"
  Base = -> Sketch065
  Dir = (0,-1,2e-16)
  DirMode = 2
  FaceMakerClass = Part::FaceMakerBullseye
  LengthFwd = 275
  LengthRev = 0
  Reversed = true
  Solid = true
  Symmetric = false
FEATURE [Sketcher::SketchObject] Sketch066
  FullyConstrained = true
  Placement = pos=(0,0,0) rot=(1,0,0;1.5708rad)
  sketch-geometry (28):
    g0: LineSegment StartX=50 StartY=70 StartZ=0 EndX=97.5 EndY=97.4241 EndZ=0
    g1: LineSegment StartX=97.5 StartY=97.4241 StartZ=0 EndX=97.5 EndY=101.424 EndZ=0
    g2: LineSegment StartX=97.5 StartY=101.424 StartZ=0 EndX=50 EndY=74 EndZ=0
    g3: LineSegment StartX=50 StartY=74 StartZ=0 EndX=50 EndY=70 EndZ=0
    g4: LineSegment StartX=50 StartY=82 StartZ=0 EndX=97.5 EndY=109.424 EndZ=0
    g5: LineSegment StartX=97.5 StartY=109.424 StartZ=0 EndX=97.5 EndY=105.424 EndZ=0
    g6: LineSegment StartX=97.5 StartY=105.424 StartZ=0 EndX=50 EndY=78 EndZ=0
    g7: LineSegment StartX=50 StartY=82 StartZ=0 EndX=50 EndY=78 EndZ=0
    g8: LineSegment StartX=75 StartY=116.424 StartZ=0 EndX=137.5 EndY=152.509 EndZ=0
    g9: LineSegment StartX=137.5 StartY=148.509 StartZ=0 EndX=75 EndY=112.424 EndZ=0
    g10: LineSegment StartX=75 StartY=112.424 StartZ=0 EndX=75 EndY=116.424 EndZ=0
    g11: LineSegment StartX=137.5 StartY=152.509 StartZ=0 EndX=200 EndY=116.424 EndZ=0
    g12: LineSegment StartX=200 StartY=116.424 StartZ=0 EndX=200 EndY=112.424 EndZ=0
    g13: LineSegment StartX=200 StartY=112.424 StartZ=0 EndX=137.5 EndY=148.509 EndZ=0
    g14: LineSegment StartX=177.5 StartY=109.424 StartZ=0 EndX=225 EndY=82 EndZ=0
    g15: LineSegment StartX=225 StartY=82 StartZ=0 EndX=225 EndY=78 EndZ=0
    g16: LineSegment StartX=225 StartY=78 StartZ=0 EndX=177.5 EndY=105.424 EndZ=0
    g17: LineSegment StartX=177.5 StartY=105.424 StartZ=0 EndX=177.5 EndY=109.424 EndZ=0
    g18: LineSegment StartX=177.5 StartY=101.424 StartZ=0 EndX=225 EndY=74 EndZ=0
    g19: LineSegment StartX=225 StartY=74 StartZ=0 EndX=225 EndY=70 EndZ=0
    g20: LineSegment StartX=225 StartY=70 StartZ=0 EndX=177.5 EndY=97.4241 EndZ=0
    g21: LineSegment StartX=177.5 StartY=101.424 StartZ=0 EndX=177.5 EndY=97.4241 EndZ=0
    g22: LineSegment StartX=75 StartY=120.424 StartZ=0 EndX=75 EndY=124.424 EndZ=0
    g23: LineSegment StartX=75 StartY=124.424 StartZ=0 EndX=137.5 EndY=160.509 EndZ=0
    g24: LineSegment StartX=137.5 StartY=160.509 StartZ=0 EndX=200 EndY=124.424 EndZ=0
    g25: LineSegment StartX=200 StartY=124.424 StartZ=0 EndX=200 EndY=120.424 EndZ=0
    g26: LineSegment StartX=200 StartY=120.424 StartZ=0 EndX=137.5 EndY=156.509 EndZ=0
    g27: LineSegment StartX=137.5 StartY=156.509 StartZ=0 EndX=75 EndY=120.424 EndZ=0
  constraints (84):
    c: Angle(g0) = 0.523599
    c: DistanceX(g0) = 50
    c: Coincident(g1,g0)
    c: Vertical(g1)
    c: Coincident(g2,g1)
    c: Coincident(g3,g2)
    c: Vertical(g3)
    c: DistanceY(g0,g2) = 4
    c: Parallel(g0,g2)
    c: Coincident(g0,g3)
    c: Coincident(g5,g4)
    c: Coincident(g7,g4)
    c: Coincident(g7,g6)
    c: Vertical(g7)
    c: Vertical(g5)
    c: Coincident(g5,g6)
    c: Parallel(g2,g6)
    c: Parallel(g6,g4)
    c: DistanceX(g6,g2) = 0
    c: DistanceY(g2,g6) = 4
    c: DistanceY(g6,g4) = 4
    c: DistanceX(g5,g1) = 0
    c: DistanceY(g0) = 70
    c: Coincident(g10,g9)
    c: Coincident(g10,g8)
    c: Vertical(g10)
    c: DistanceY(g9,g8) = 4
    c: Parallel(g8,g9)
    c: DistanceX(g9,g9) = 62.5
    c: Coincident(g11,g8)
    c: Coincident(g12,g11)
    c: Coincident(g13,g12)
    c: Coincident(g13,g9)
    c: Parallel(g13,g11)
    c: Vertical(g12)
    c: Coincident(g15,g14)
    c: Vertical(g15)
    c: Coincident(g17,g16)
    c: Coincident(g17,g14)
    c: Coincident(g19,g18)
    c: Vertical(g19)
    c: Coincident(g20,g19)
    c: Coincident(g21,g18)
    c: Coincident(g21,g20)
    c: Vertical(g21)
    c: Vertical(g17)
    c: DistanceX(g18,g16) = 0
    c: DistanceY(g16,g14) = 4
    c: DistanceY(g18,g16) = 4
    c: DistanceY(g20,g18) = 4
    c: Parallel(g20,g18)
    c: Parallel(g18,g16)
    c: Parallel(g16,g14)
    c: Coincident(g15,g16)
    c: DistanceY(g19,g0) = 0
    c: DistanceX(g18,g15) = 0
    c: DistanceX(g14,g14) = 47.5
    c: DistanceX(g4,g4) = 47.5
    c: DistanceX(g4,g14) = 80
    c: Parallel(g9,g4)
    c: DistanceX(g9,g8) = 0
    c: DistanceY(g4,g9) = 3
    c: DistanceY(g14,g12) = 3
    c: DistanceY(g14,g4) = 0
    c: DistanceX(g8) = 137.5
    c: DistanceX(g9,g12) = 125
    c: Vertical(g22)
    c: Coincident(g23,g22)
    c: Coincident(g24,g23)
    c: Coincident(g25,g24)
    c: Vertical(g25)
    c: Coincident(g26,g25)
    c: Coincident(g27,g22)
    c: DistanceX(g22,g8) = 0
    c: DistanceY(g8,g22) = 4
    c: DistanceY(g22,g22) = 4
    c: Coincident(g26,g27)
    c: DistanceX(g26,g8) = 0
    c: DistanceY(g26,g23) = 4
    c: DistanceY(g8,g26) = 4
    c: DistanceX(g23,g26) = 0
    c: DistanceX(g25,g11) = 0
    c: DistanceY(g11,g25) = 4
    c: DistanceY(g25,g24) = 4
FEATURE [Part::Extrusion] Extrude025  label="cuts017"
  Base = -> Sketch066
  Dir = (0,-1,2e-16)
  DirMode = 2
  FaceMakerClass = Part::FaceMakerBullseye
  LengthFwd = 275
  LengthRev = 0
  Placement = pos=(275,0,0) rot=(0,0,1;1.5708rad)
  Reversed = true
  Solid = true
  Symmetric = false
FEATURE [Sketcher::SketchObject] Sketch067
  FullyConstrained = true
  Placement = pos=(0,0,0) rot=(1,0,0;1.5708rad)
  sketch-geometry (3):
    g0: LineSegment StartX=15 StartY=0 StartZ=0 EndX=260 EndY=0 EndZ=0
    g1: LineSegment StartX=260 StartY=0 StartZ=0 EndX=137.5 EndY=160 EndZ=0
    g2: LineSegment StartX=137.5 StartY=160 StartZ=0 EndX=15 EndY=0 EndZ=0
  constraints (9):
    c: Horizontal(g0)
    c: Coincident(g1,g0)
    c: Coincident(g2,g1)
    c: DistanceX(g0) = 260
    c: DistanceX(g1) = 137.5
    c: DistanceY(g1) = 160
    c: Coincident(g0,g2)
    c: DistanceY(g0,g-1) = 0
    c: DistanceX(g-1,g0) = 15
FEATURE [Part::Extrusion] Extrude026
  Base = -> Sketch067
  Dir = (0,-1,-6e-16)
  DirMode = 2
  FaceMakerClass = Part::FaceMakerBullseye
  LengthFwd = 275
  LengthRev = 0
  Placement = pos=(0,0,0) rot=(0,0,1;1.5708rad)
  Solid = true
  Symmetric = false
FEATURE [Part::MultiCommon] Common011  label="cuts014"
  Shapes = -> [Extrude026,Extrude024]
FEATURE [Sketcher::SketchObject] Sketch068
  FullyConstrained = true
  Placement = pos=(0,0,0) rot=(1,0,0;1.5708rad)
  sketch-geometry (3):
    g0: LineSegment StartX=15 StartY=0 StartZ=0 EndX=260 EndY=0 EndZ=0
    g1: LineSegment StartX=260 StartY=0 StartZ=0 EndX=137.5 EndY=160 EndZ=0
    g2: LineSegment StartX=137.5 StartY=160 StartZ=0 EndX=15 EndY=0 EndZ=0
  constraints (9):
    c: Horizontal(g0)
    c: Coincident(g1,g0)
    c: Coincident(g2,g1)
    c: DistanceX(g0) = 260
    c: DistanceX(g1) = 137.5
    c: DistanceY(g1) = 160
    c: Coincident(g0,g2)
    c: DistanceY(g0,g-1) = 0
    c: DistanceX(g-1,g0) = 15
FEATURE [Part::Extrusion] Extrude027
  Base = -> Sketch068
  Dir = (0,-1,2e-16)
  DirMode = 2
  FaceMakerClass = Part::FaceMakerBullseye
  LengthFwd = 275
  LengthRev = 0
  Reversed = true
  Solid = true
  Symmetric = false
FEATURE [Part::MultiCommon] Common012  label="cuts015"
  Shapes = -> [Extrude027,Extrude025]
FEATURE [Part::MultiFuse] Fusion063  label="keep002"
  Placement = pos=(0,0,4) rot=(0,0,1;0rad)
  Shapes = -> [Common012,Common011]
FEATURE [Part::MultiCommon] Common013  label="keeps002"
  Shapes = -> [Loft010,Fusion063]
FEATURE [Part::MultiFuse] Fusion064  label="shell002"
  Shapes = -> [Cut007,Common013]
FEATURE [Part::MultiFuse] Fusion065  label="shellLegacy"
  Shapes = -> [Common008,Fusion064]
FEATURE [Part::Cut] Cut008  label="shellNow-Ref"
  Base = -> Fusion065
  Tool = -> Fusion062
FEATURE [Part::Feature] Part__Feature195  label="Heat Sink001"
  shape: bbox 100 x 91 x 19 mm, 161 faces (baked)
FEATURE [Part::Feature] Part__Feature196  label="Battery Holder001"
  shape: bbox 28.5 x 16 x 6 mm, 91 faces (baked)
FEATURE [Part::Feature] Part__Feature197  label="DC Jack001"
  shape: bbox 7.6 x 11.5 x 9.75 mm, 10 faces (baked)
FEATURE [Part::Feature] Part__Feature198  label="PCB001"
  shape: bbox 90 x 90 x 3.3 mm, 59 faces (baked)
FEATURE [Part::Feature] Part__Feature199  label="HDMI001"
  shape: bbox 14.51 x 11.61 x 5.506 mm, 31 faces (baked)
FEATURE [Part::Feature] Part__Feature200  label="Ethernet001"
  shape: bbox 15.9 x 21.4 x 13.5 mm, 25 faces (baked)
FEATURE [Part::Feature] Part__Feature201  label="USB 3.0 B001"
  shape: bbox 14.55 x 17.5 x 16.15 mm, 36 faces (baked)
FEATURE [Part::Feature] Part__Feature202  label="USB 3.0 A001"
  shape: bbox 14.55 x 17.5 x 16.15 mm, 36 faces (baked)
FEATURE [Part::Feature] Part__Feature203  label="Audio Jack001"
  shape: bbox 6.5 x 14 x 4 mm, 10 faces (baked)
FEATURE [Part::Feature] Part__Feature204  label="Fan Plug001"
  shape: bbox 3.75 x 7.5 x 4.75 mm, 32 faces (baked)
FEATURE [Part::Feature] Part__Feature205  label="REMOCON001"
  shape: bbox 7.006 x 5.006 x 12.01 mm, 30 faces (baked)
FEATURE [Part::Feature] Part__Feature206  label="eMMC001"
  shape: bbox 13.5 x 18.5 x 2.8 mm, 33 faces (baked)
FEATURE [Part::Feature] Part__Feature207  label="MicroUSB001"
  shape: bbox 7.012 x 4.616 x 3.511 mm, 31 faces (baked)
FEATURE [Part::Feature] Part__Feature208  label="Switch001"
  shape: bbox 9 x 5.74 x 3.5 mm, 11 faces (baked)
FEATURE [Part::Feature] Part__Feature209  label="MicroSD Card Socket001"
  shape: bbox 11.5 x 5.5 x 3.5 mm, 11 faces (baked)
FEATURE [Part::Feature] Part__Feature210  label="7 Pin Header001"
  shape: bbox 17.5 x 2.5 x 8 mm, 41 faces (baked)
FEATURE [Part::Feature] Part__Feature211  label="UART001"
  shape: bbox 5 x 12.5 x 6 mm, 43 faces (baked)
FEATURE [Part::Feature] Part__Feature212  label="40 Pin Header001"
  shape: bbox 5 x 50 x 8 mm, 206 faces (baked)
FEATURE [App::Part] Odroid_N2__v005  label="Odroid-N2+ v005"
  Group = -> [Part__Feature195,Part__Feature196,Part__Feature197,Part__Feature198,Part__Feature199,Part__Feature200,Part__Feature201,Part__Feature202,Part__Feature203,Part__Feature204,Part__Feature205,Part__Feature206,Part__Feature207,Part__Feature208,Part__Feature209,Part__Feature210,Part__Feature211,Part__Feature212]
  Origin = -> Origin021
  Placement = pos=(202.1,952,-21.5) rot=(0,0,1;3.14159rad)
FEATURE [Part::Feature] Part__Feature028  label="DCP-RJ6ST-F"
  Placement = pos=(160,215,6) rot=(1,0,0;3.80482rad)
  shape: bbox 40.26 x 41.22 x 44.64 mm, 485 faces, 2 solids (baked)
FEATURE [Part::Feature] Part__Feature027  label="DCC-RJ6ST-310"
  Placement = pos=(160,216.65,3) rot=(1,0,0;0.663225rad)
  shape: bbox 40.36 x 68.78 x 64.36 mm, 441 faces (baked)
FEATURE [Part::Feature] Shell029
  shape: bbox 36.98 x 21.68 x 36.68 mm, 152 faces, 0 solids (baked)
FEATURE [Part::Feature] Shell030
  shape: bbox 22.66 x 11.43 x 22.66 mm, 6 faces, 0 solids (baked)
FEATURE [Part::Feature] Shell031
  shape: bbox 0.3612 x 0.889 x 0.6255 mm, 1 faces, 0 solids (baked)
FEATURE [Part::Feature] Shell032
  shape: bbox 35.58 x 29.16 x 35.58 mm, 49 faces, 0 solids (baked)
FEATURE [Part::Feature] Shell033
  shape: bbox 24.46 x 14.2 x 24.46 mm, 102 faces, 0 solids (baked)
FEATURE [Part::Feature] Shell034
  shape: bbox 0.3892 x 1.194 x 0.6742 mm, 1 faces, 0 solids (baked)
FEATURE [Part::Feature] Shell035
  shape: bbox 0.2703 x 0.381 x 0.4682 mm, 1 faces, 0 solids (baked)
FEATURE [Part::Feature] Shell036
  shape: bbox 0.2577 x 0.3048 x 0.4459 mm, 1 faces, 0 solids (baked)
FEATURE [Part::Feature] Shell037
  shape: bbox 36.98 x 18.12 x 36.6 mm, 205 faces, 0 solids (baked)
FEATURE [Part::Compound2] Compound003  label="M3222GBH_SW0002"
  Links = -> [Shell037,Shell029,Shell030,Shell033,Shell032,Shell036,Shell034,Shell031,Shell035]
  Placement = pos=(230,212,0) rot=(1,0,0;4.71239rad)
FEATURE [Part::Box] Box018  label="Cube"
  AttacherType = Attacher::AttachEngine3D
  Height = 75
  Length = 100
  Width = 100
FEATURE [Part::Box] Box019  label="Cube001"
  AttacherType = Attacher::AttachEngine3D
  Height = 75
  Length = 100
  Placement = pos=(175,0,0) rot=(0,0,1;0rad)
  Width = 100
FEATURE [Part::Box] Box020  label="Cube002"
  AttacherType = Attacher::AttachEngine3D
  Height = 75
  Length = 100
  Placement = pos=(175,175,0) rot=(0,0,1;0rad)
  Width = 100
FEATURE [Part::Box] Box021  label="Cube003"
  AttacherType = Attacher::AttachEngine3D
  Height = 75
  Length = 100
  Placement = pos=(0,175,0) rot=(0,0,1;0rad)
  Width = 100
FEATURE [Sketcher::SketchObject] Sketch069
  FullyConstrained = true
  sketch-geometry (4):
    g0: LineSegment StartX=0 StartY=275 StartZ=0 EndX=275 EndY=275 EndZ=0
    g1: LineSegment StartX=275 StartY=275 StartZ=0 EndX=275 EndY=0 EndZ=0
    g2: LineSegment StartX=275 StartY=0 StartZ=0 EndX=0 EndY=0 EndZ=0
    g3: LineSegment StartX=0 StartY=0 StartZ=0 EndX=0 EndY=275 EndZ=0
  constraints (11):
    c: Coincident(g0,g1)
    c: Coincident(g1,g2)
    c: Coincident(g2,g3)
    c: Coincident(g3,g0)
    c: Horizontal(g0)
    c: Horizontal(g2)
    c: Vertical(g1)
    c: Vertical(g3)
    c: Coincident(g2,g-1)
    c: DistanceX(g2,g2) = 275
    c: DistanceY(g3,g3) = 275
FEATURE [Sketcher::SketchObject] Sketch070
  FullyConstrained = true
  Placement = pos=(0,0,175.1) rot=(0,0,1;0rad)
  sketch-geometry (5):
    g0: GeomPoint X=137.5 Y=137.5 Z=0
    g1: LineSegment StartX=137.55 StartY=137.55 StartZ=0 EndX=137.55 EndY=137.45 EndZ=0
    g2: LineSegment StartX=137.55 StartY=137.45 StartZ=0 EndX=137.45 EndY=137.45 EndZ=0
    g3: LineSegment StartX=137.45 StartY=137.45 StartZ=0 EndX=137.45 EndY=137.55 EndZ=0
    g4: LineSegment StartX=137.45 StartY=137.55 StartZ=0 EndX=137.55 EndY=137.55 EndZ=0
  constraints (14):
    c: Coincident(g1,g2)
    c: Horizontal(g2)
    c: Vertical(g1)
    c: DistanceX(g2,g2) = 0.1
    c: DistanceX(g2,g0) = 0.05
    c: DistanceY(g1,g1) = 0.1
    c: DistanceY(g1,g0) = -0.05
    c: DistanceX(g0) = 137.5
    c: DistanceY(g0) = 137.5
    c: Coincident(g3,g2)
    c: Vertical(g3)
    c: Coincident(g4,g3)
    c: Coincident(g4,g1)
    c: Horizontal(g4)
FEATURE [Part::Loft] Loft013  label="outerLayer013"
  Closed = false
  MaxDegree = 5
  Ruled = false
  Sections = -> [Sketch069,Sketch070]
  Solid = true
FEATURE [Part::MultiCommon] Common014  label="legs001"
  Placement = pos=(-58.87,-58.87,-75) rot=(0,0,1;0rad)
  Shapes = -> [Loft013,Box018]
FEATURE [Sketcher::SketchObject] Sketch071
  FullyConstrained = true
  sketch-geometry (4):
    g0: LineSegment StartX=0 StartY=275 StartZ=0 EndX=275 EndY=275 EndZ=0
    g1: LineSegment StartX=275 StartY=275 StartZ=0 EndX=275 EndY=0 EndZ=0
    g2: LineSegment StartX=275 StartY=0 StartZ=0 EndX=0 EndY=0 EndZ=0
    g3: LineSegment StartX=0 StartY=0 StartZ=0 EndX=0 EndY=275 EndZ=0
  constraints (11):
    c: Coincident(g0,g1)
    c: Coincident(g1,g2)
    c: Coincident(g2,g3)
    c: Coincident(g3,g0)
    c: Horizontal(g0)
    c: Horizontal(g2)
    c: Vertical(g1)
    c: Vertical(g3)
    c: Coincident(g2,g-1)
    c: DistanceX(g2,g2) = 275
    c: DistanceY(g3,g3) = 275
FEATURE [Sketcher::SketchObject] Sketch072
  FullyConstrained = true
  Placement = pos=(0,0,175.1) rot=(0,0,1;0rad)
  sketch-geometry (5):
    g0: GeomPoint X=137.5 Y=137.5 Z=0
    g1: LineSegment StartX=137.55 StartY=137.55 StartZ=0 EndX=137.55 EndY=137.45 EndZ=0
    g2: LineSegment StartX=137.55 StartY=137.45 StartZ=0 EndX=137.45 EndY=137.45 EndZ=0
    g3: LineSegment StartX=137.45 StartY=137.45 StartZ=0 EndX=137.45 EndY=137.55 EndZ=0
    g4: LineSegment StartX=137.45 StartY=137.55 StartZ=0 EndX=137.55 EndY=137.55 EndZ=0
  constraints (14):
    c: Coincident(g1,g2)
    c: Horizontal(g2)
    c: Vertical(g1)
    c: DistanceX(g2,g2) = 0.1
    c: DistanceX(g2,g0) = 0.05
    c: DistanceY(g1,g1) = 0.1
    c: DistanceY(g1,g0) = -0.05
    c: DistanceX(g0) = 137.5
    c: DistanceY(g0) = 137.5
    c: Coincident(g3,g2)
    c: Vertical(g3)
    c: Coincident(g4,g3)
    c: Coincident(g4,g1)
    c: Horizontal(g4)
FEATURE [Part::Loft] Loft018  label="outerLayer014"
  Closed = false
  MaxDegree = 5
  Ruled = false
  Sections = -> [Sketch071,Sketch072]
  Solid = true
FEATURE [Part::MultiCommon] Common015  label="legs002"
  Placement = pos=(58.87,-58.87,-75) rot=(0,0,1;0rad)
  Shapes = -> [Loft018,Box019]
FEATURE [Sketcher::SketchObject] Sketch073
  FullyConstrained = true
  sketch-geometry (4):
    g0: LineSegment StartX=0 StartY=275 StartZ=0 EndX=275 EndY=275 EndZ=0
    g1: LineSegment StartX=275 StartY=275 StartZ=0 EndX=275 EndY=0 EndZ=0
    g2: LineSegment StartX=275 StartY=0 StartZ=0 EndX=0 EndY=0 EndZ=0
    g3: LineSegment StartX=0 StartY=0 StartZ=0 EndX=0 EndY=275 EndZ=0
  constraints (11):
    c: Coincident(g0,g1)
    c: Coincident(g1,g2)
    c: Coincident(g2,g3)
    c: Coincident(g3,g0)
    c: Horizontal(g0)
    c: Horizontal(g2)
    c: Vertical(g1)
    c: Vertical(g3)
    c: Coincident(g2,g-1)
    c: DistanceX(g2,g2) = 275
    c: DistanceY(g3,g3) = 275
FEATURE [Sketcher::SketchObject] Sketch074
  FullyConstrained = true
  Placement = pos=(0,0,175.1) rot=(0,0,1;0rad)
  sketch-geometry (5):
    g0: GeomPoint X=137.5 Y=137.5 Z=0
    g1: LineSegment StartX=137.55 StartY=137.55 StartZ=0 EndX=137.55 EndY=137.45 EndZ=0
    g2: LineSegment StartX=137.55 StartY=137.45 StartZ=0 EndX=137.45 EndY=137.45 EndZ=0
    g3: LineSegment StartX=137.45 StartY=137.45 StartZ=0 EndX=137.45 EndY=137.55 EndZ=0
    g4: LineSegment StartX=137.45 StartY=137.55 StartZ=0 EndX=137.55 EndY=137.55 EndZ=0
  constraints (14):
    c: Coincident(g1,g2)
    c: Horizontal(g2)
    c: Vertical(g1)
    c: DistanceX(g2,g2) = 0.1
    c: DistanceX(g2,g0) = 0.05
    c: DistanceY(g1,g1) = 0.1
    c: DistanceY(g1,g0) = -0.05
    c: DistanceX(g0) = 137.5
    c: DistanceY(g0) = 137.5
    c: Coincident(g3,g2)
    c: Vertical(g3)
    c: Coincident(g4,g3)
    c: Coincident(g4,g1)
    c: Horizontal(g4)
FEATURE [Part::Loft] Loft019  label="outerLayer015"
  Closed = false
  MaxDegree = 5
  Ruled = false
  Sections = -> [Sketch073,Sketch074]
  Solid = true
FEATURE [Part::MultiCommon] Common016  label="legs003"
  Placement = pos=(58.87,58.87,-75) rot=(0,0,1;0rad)
  Shapes = -> [Loft019,Box020]
FEATURE [Sketcher::SketchObject] Sketch075
  FullyConstrained = true
  sketch-geometry (4):
    g0: LineSegment StartX=0 StartY=275 StartZ=0 EndX=275 EndY=275 EndZ=0
    g1: LineSegment StartX=275 StartY=275 StartZ=0 EndX=275 EndY=0 EndZ=0
    g2: LineSegment StartX=275 StartY=0 StartZ=0 EndX=0 EndY=0 EndZ=0
    g3: LineSegment StartX=0 StartY=0 StartZ=0 EndX=0 EndY=275 EndZ=0
  constraints (11):
    c: Coincident(g0,g1)
    c: Coincident(g1,g2)
    c: Coincident(g2,g3)
    c: Coincident(g3,g0)
    c: Horizontal(g0)
    c: Horizontal(g2)
    c: Vertical(g1)
    c: Vertical(g3)
    c: Coincident(g2,g-1)
    c: DistanceX(g2,g2) = 275
    c: DistanceY(g3,g3) = 275
FEATURE [Sketcher::SketchObject] Sketch076
  FullyConstrained = true
  Placement = pos=(0,0,175.1) rot=(0,0,1;0rad)
  sketch-geometry (5):
    g0: GeomPoint X=137.5 Y=137.5 Z=0
    g1: LineSegment StartX=137.55 StartY=137.55 StartZ=0 EndX=137.55 EndY=137.45 EndZ=0
    g2: LineSegment StartX=137.55 StartY=137.45 StartZ=0 EndX=137.45 EndY=137.45 EndZ=0
    g3: LineSegment StartX=137.45 StartY=137.45 StartZ=0 EndX=137.45 EndY=137.55 EndZ=0
    g4: LineSegment StartX=137.45 StartY=137.55 StartZ=0 EndX=137.55 EndY=137.55 EndZ=0
  constraints (14):
    c: Coincident(g1,g2)
    c: Horizontal(g2)
    c: Vertical(g1)
    c: DistanceX(g2,g2) = 0.1
    c: DistanceX(g2,g0) = 0.05
    c: DistanceY(g1,g1) = 0.1
    c: DistanceY(g1,g0) = -0.05
    c: DistanceX(g0) = 137.5
    c: DistanceY(g0) = 137.5
    c: Coincident(g3,g2)
    c: Vertical(g3)
    c: Coincident(g4,g3)
    c: Coincident(g4,g1)
    c: Horizontal(g4)
FEATURE [Part::Loft] Loft020  label="outerLayer016"
  Closed = false
  MaxDegree = 5
  Ruled = false
  Sections = -> [Sketch075,Sketch076]
  Solid = true
FEATURE [Part::MultiCommon] Common017  label="legs004"
  Placement = pos=(-58.87,58.87,-75) rot=(0,0,1;0rad)
  Shapes = -> [Loft020,Box021]
FEATURE [Part::Feature] Feature001  label="PG7"
  Placement = pos=(75,40,-248) rot=(0,0,1;0rad)
  shape: bbox 21.32 x 20.97 x 29.79 mm, 246 faces, 3 solids (baked)
FEATURE [Part::Feature] Shell038
  shape: bbox 36.98 x 21.68 x 36.68 mm, 152 faces, 0 solids (baked)
FEATURE [Part::Feature] Shell039
  shape: bbox 22.66 x 11.43 x 22.66 mm, 6 faces, 0 solids (baked)
FEATURE [Part::Feature] Shell040
  shape: bbox 0.3612 x 0.889 x 0.6255 mm, 1 faces, 0 solids (baked)
FEATURE [Part::Feature] Shell041
  shape: bbox 35.58 x 29.16 x 35.58 mm, 49 faces, 0 solids (baked)
FEATURE [Part::Feature] Shell042
  shape: bbox 24.46 x 14.2 x 24.46 mm, 102 faces, 0 solids (baked)
FEATURE [Part::Feature] Shell043
  shape: bbox 0.3892 x 1.194 x 0.6742 mm, 1 faces, 0 solids (baked)
FEATURE [Part::Feature] Shell044
  shape: bbox 0.2703 x 0.381 x 0.4682 mm, 1 faces, 0 solids (baked)
FEATURE [Part::Feature] Shell045
  shape: bbox 0.2577 x 0.3048 x 0.4459 mm, 1 faces, 0 solids (baked)
FEATURE [Part::Feature] Shell046
  shape: bbox 36.98 x 18.12 x 36.6 mm, 205 faces, 0 solids (baked)
FEATURE [Part::Compound2] Compound004  label="M3222GBH_SW0003"
  Links = -> [Shell046,Shell038,Shell039,Shell042,Shell041,Shell045,Shell043,Shell040,Shell044]
  Placement = pos=(45,212,0) rot=(-1,0,0;1.5708rad)
FEATURE [Part::Feature] Part__Feature214  label="DCC-RJ6ST-311-Ref"
  Placement = pos=(160,215,-5) rot=(1,0,0;0rad)
  shape: bbox 40.36 x 68.07 x 51.72 mm, 441 faces (baked)
FEATURE [Part::Feature] Part__Feature215  label="DCP-RJ6ST-F001-Ref"
  Placement = pos=(160,215,6) rot=(0,0.940376,0.340136;0rad)
  shape: bbox 40.26 x 40.33 x 38.85 mm, 485 faces, 2 solids (baked)
FEATURE [Part::Feature] Part__Feature216  label="powerInsert001-Ref"
  Placement = pos=(100,215,-11.17) rot=(1,0,0;1.5708rad)
  shape: bbox 29.63 x 29.64 x 35.77 mm, 59 faces (baked)
FEATURE [Sketcher::SketchObject] Sketch077
  FullyConstrained = true
  sketch-geometry (6):
    g0: LineSegment StartX=67.5 StartY=50 StartZ=0 EndX=207.5 EndY=50 EndZ=0
    g1: LineSegment StartX=207.5 StartY=50 StartZ=0 EndX=207.5 EndY=0 EndZ=0
    g2: LineSegment StartX=207.5 StartY=0 StartZ=0 EndX=67.5 EndY=0 EndZ=0
    g3: LineSegment StartX=67.5 StartY=0 StartZ=0 EndX=67.5 EndY=50 EndZ=0
    g4: Circle CenterX=100 CenterY=25 CenterZ=0 NormalX=0 NormalY=0 NormalZ=1 AngleXU=0 Radius=11
    g5: Circle CenterX=160 CenterY=25 CenterZ=0 NormalX=0 NormalY=0 NormalZ=1 AngleXU=0 Radius=15.1
  constraints (18):
    c: Coincident(g0,g1)
    c: Coincident(g1,g2)
    c: Coincident(g2,g3)
    c: Coincident(g3,g0)
    c: Horizontal(g0)
    c: Horizontal(g2)
    c: Vertical(g1)
    c: Vertical(g3)
    c: DistanceX(g2) = 67.5
    c: DistanceY(g2) = 0
    c: DistanceX(g2,g1) = 140
    c: DistanceY(g2,g0) = 50
    c: Diameter(g4) = 22
    c: Diameter(g5) = 30.2
    c: Horizontal(g4,g5)
    c: DistanceX(g2,g4) = 32.5
    c: DistanceY(g2,g4) = 25
    c: DistanceX(g4,g5) = 60
FEATURE [Part::Extrusion] Extrude028  label="backEndInserts"
  Base = -> Sketch077
  Dir = (0,0,1)
  DirMode = 2
  FaceMakerClass = Part::FaceMakerBullseye
  LengthFwd = 5
  LengthRev = 0
  Placement = pos=(0,199,-15) rot=(1,0,0;0.663225rad)
  Solid = true
  Symmetric = false
FEATURE [Sketcher::SketchObject] Sketch079
  FullyConstrained = true
  Placement = pos=(0,0,0) rot=(0.57735,0.57735,0.57735;2.0944rad)
  sketch-geometry (4):
    g0: LineSegment StartX=187.35 StartY=5 StartZ=0 EndX=187.35 EndY=0 EndZ=0
    g1: LineSegment StartX=187.35 StartY=0 StartZ=0 EndX=250.7 EndY=0 EndZ=0
    g2: LineSegment StartX=250.7 StartY=0 StartZ=0 EndX=250.7 EndY=5 EndZ=0
    g3: LineSegment StartX=250.7 StartY=5 StartZ=0 EndX=187.35 EndY=5 EndZ=0
  constraints (12):
    c: Coincident(g1,g0)
    c: PointOnObject(g1,g-1)
    c: Horizontal(g1)
    c: Coincident(g2,g1)
    c: Coincident(g3,g2)
    c: Coincident(g3,g0)
    c: Horizontal(g3)
    c: DistanceX(g0) = 187.35
    c: Vertical(g0)
    c: DistanceX(g0,g1) = 63.35
    c: Vertical(g2)
    c: DistanceY(g0,g0) = 5
FEATURE [Part::Extrusion] Extrude030  label="baseCutter"
  Base = -> Sketch079
  Dir = (1,0,0)
  DirMode = 2
  FaceMakerClass = Part::FaceMakerBullseye
  LengthFwd = 140
  LengthRev = 0
  Placement = pos=(67.5,0,0) rot=(0,0,1;0rad)
  Solid = true
  Symmetric = false
FEATURE [Part::Cut] Cut009  label="level2s001"
  Base = -> Cut001
  Tool = -> Extrude030
FEATURE [Sketcher::SketchObject] Sketch080
  FullyConstrained = true
  Placement = pos=(67.5,0,0) rot=(0.57735,0.57735,0.57735;2.0944rad)
  sketch-geometry (6):
    g0: LineSegment StartX=177.03 StartY=5 StartZ=0 EndX=195.062 EndY=-18.08 EndZ=0
    g1: LineSegment StartX=239.27 StartY=22.8 StartZ=0 EndX=257.08 EndY=0 EndZ=0
    g2: LineSegment StartX=239.27 StartY=22.8 StartZ=0 EndX=216.483 EndY=5 EndZ=0
    g3: LineSegment StartX=195.062 StartY=-18.08 StartZ=0 EndX=218.203 EndY=0 EndZ=0
    g4: LineSegment StartX=218.203 StartY=0 StartZ=0 EndX=257.08 EndY=0 EndZ=0
    g5: LineSegment StartX=177.03 StartY=5 StartZ=0 EndX=216.483 EndY=5 EndZ=0
  constraints (18):
    c: Angle(g0) = -0.907571
    c: DistanceX(g1,g1) = 17.81
    c: DistanceY(g1,g1) = 22.8
    c: Coincident(g2,g1)
    c: Angle(g2,g1) = 1.5708
    c: DistanceY(g1) = 0
    c: Coincident(g3,g0)
    c: PointOnObject(g3,g-1)
    c: Angle(g3,g0) = 1.5708
    c: Coincident(g4,g3)
    c: Coincident(g4,g1)
    c: DistanceY(g2) = 5
    c: DistanceY(g0) = -18.08
    c: DistanceX(g1) = 257.08
    c: DistanceX(g0) = 177.03
    c: Coincident(g5,g0)
    c: Coincident(g5,g2)
    c: Horizontal(g5)
FEATURE [Part::Extrusion] Extrude031
  Base = -> Sketch080
  Dir = (1,0,0)
  DirMode = 2
  FaceMakerClass = Part::FaceMakerBullseye
  LengthFwd = 18
  LengthRev = 0
  Solid = true
  Symmetric = false
FEATURE [Sketcher::SketchObject] Sketch081
  FullyConstrained = true
  Placement = pos=(67.5,0,0) rot=(0.57735,0.57735,0.57735;2.0944rad)
  sketch-geometry (6):
    g0: LineSegment StartX=177.03 StartY=5 StartZ=0 EndX=195.062 EndY=-18.08 EndZ=0
    g1: LineSegment StartX=239.27 StartY=22.8 StartZ=0 EndX=257.08 EndY=0 EndZ=0
    g2: LineSegment StartX=239.27 StartY=22.8 StartZ=0 EndX=216.483 EndY=5 EndZ=0
    g3: LineSegment StartX=195.062 StartY=-18.08 StartZ=0 EndX=218.203 EndY=0 EndZ=0
    g4: LineSegment StartX=218.203 StartY=0 StartZ=0 EndX=257.08 EndY=0 EndZ=0
    g5: LineSegment StartX=177.03 StartY=5 StartZ=0 EndX=216.483 EndY=5 EndZ=0
  constraints (18):
    c: Angle(g0) = -0.907571
    c: DistanceX(g1,g1) = 17.81
    c: DistanceY(g1,g1) = 22.8
    c: Coincident(g2,g1)
    c: Angle(g2,g1) = 1.5708
    c: DistanceY(g1) = 0
    c: Coincident(g3,g0)
    c: PointOnObject(g3,g-1)
    c: Angle(g3,g0) = 1.5708
    c: Coincident(g4,g3)
    c: Coincident(g4,g1)
    c: DistanceY(g2) = 5
    c: DistanceY(g0) = -18.08
    c: DistanceX(g1) = 257.08
    c: DistanceX(g0) = 177.03
    c: Coincident(g5,g0)
    c: Coincident(g5,g2)
    c: Horizontal(g5)
FEATURE [Part::Extrusion] Extrude032
  Base = -> Sketch081
  Dir = (1,0,0)
  DirMode = 2
  FaceMakerClass = Part::FaceMakerBullseye
  LengthFwd = 18
  LengthRev = 0
  Placement = pos=(48.5,0,0) rot=(0,0,1;0rad)
  Solid = true
  Symmetric = false
FEATURE [Sketcher::SketchObject] Sketch082
  FullyConstrained = true
  Placement = pos=(67.5,0,0) rot=(0.57735,0.57735,0.57735;2.0944rad)
  sketch-geometry (6):
    g0: LineSegment StartX=177.03 StartY=5 StartZ=0 EndX=195.062 EndY=-18.08 EndZ=0
    g1: LineSegment StartX=239.27 StartY=22.8 StartZ=0 EndX=257.08 EndY=0 EndZ=0
    g2: LineSegment StartX=239.27 StartY=22.8 StartZ=0 EndX=216.483 EndY=5 EndZ=0
    g3: LineSegment StartX=195.062 StartY=-18.08 StartZ=0 EndX=218.203 EndY=0 EndZ=0
    g4: LineSegment StartX=218.203 StartY=0 StartZ=0 EndX=257.08 EndY=0 EndZ=0
    g5: LineSegment StartX=177.03 StartY=5 StartZ=0 EndX=216.483 EndY=5 EndZ=0
  constraints (18):
    c: Angle(g0) = -0.907571
    c: DistanceX(g1,g1) = 17.81
    c: DistanceY(g1,g1) = 22.8
    c: Coincident(g2,g1)
    c: Angle(g2,g1) = 1.5708
    c: DistanceY(g1) = 0
    c: Coincident(g3,g0)
    c: PointOnObject(g3,g-1)
    c: Angle(g3,g0) = 1.5708
    c: Coincident(g4,g3)
    c: Coincident(g4,g1)
    c: DistanceY(g2) = 5
    c: DistanceY(g0) = -18.08
    c: DistanceX(g1) = 257.08
    c: DistanceX(g0) = 177.03
    c: Coincident(g5,g0)
    c: Coincident(g5,g2)
    c: Horizontal(g5)
FEATURE [Part::Extrusion] Extrude033
  Base = -> Sketch082
  Dir = (1,0,0)
  DirMode = 2
  FaceMakerClass = Part::FaceMakerBullseye
  LengthFwd = 18
  LengthRev = 0
  Placement = pos=(122,0,0) rot=(0,0,1;0rad)
  Solid = true
  Symmetric = false
FEATURE [Part::Feature] Part__Feature213  label="powerInsert"
  Placement = pos=(100,228.5,-12.5) rot=(1,0,0;2.23402rad)
  shape: bbox 29.63 x 33.99 x 37.99 mm, 59 faces (baked)
FEATURE [Part::MultiFuse] Fusion066
  Shapes = -> [Extrude033,Extrude031,Extrude032]
FEATURE [Part::MultiFuse] Fusion067
  Shapes = -> [Fusion066,Cut009]
FEATURE [Part::MultiFuse] Fusion068  label="level02s"
  Shapes = -> [Extrude028,Fusion067]
FEATURE [Part::Box] Box002  label="Cube004"
  AttacherType = Attacher::AttachEngine3D
  Height = 63.75
  Length = 275
  Width = 275
FEATURE [Part::Box] Box003  label="Cube005"
  AttacherType = Attacher::AttachEngine3D
  Height = 3.75
  Length = 275
  Placement = pos=(0,0,59.75) rot=(0,0,1;0rad)
  Width = 275
FEATURE [Part::Box] Box004  label="Cube006"
  AttacherType = Attacher::AttachEngine3D
  Height = 59.75
  Length = 275
  Width = 275
FEATURE [Sketcher::SketchObject] Sketch083
  FullyConstrained = true
  sketch-geometry (4):
    g0: LineSegment StartX=0 StartY=275 StartZ=0 EndX=275 EndY=275 EndZ=0
    g1: LineSegment StartX=275 StartY=275 StartZ=0 EndX=275 EndY=0 EndZ=0
    g2: LineSegment StartX=275 StartY=0 StartZ=0 EndX=0 EndY=0 EndZ=0
    g3: LineSegment StartX=0 StartY=0 StartZ=0 EndX=0 EndY=275 EndZ=0
  constraints (11):
    c: Coincident(g0,g1)
    c: Coincident(g1,g2)
    c: Coincident(g2,g3)
    c: Coincident(g3,g0)
    c: Horizontal(g0)
    c: Horizontal(g2)
    c: Vertical(g1)
    c: Vertical(g3)
    c: Coincident(g2,g-1)
    c: DistanceX(g2,g2) = 275
    c: DistanceY(g3,g3) = 275
FEATURE [Sketcher::SketchObject] Sketch084
  FullyConstrained = true
  Placement = pos=(0,0,175.1) rot=(0,0,1;0rad)
  sketch-geometry (5):
    g0: GeomPoint X=137.5 Y=137.5 Z=0
    g1: LineSegment StartX=137.55 StartY=137.55 StartZ=0 EndX=137.55 EndY=137.45 EndZ=0
    g2: LineSegment StartX=137.55 StartY=137.45 StartZ=0 EndX=137.45 EndY=137.45 EndZ=0
    g3: LineSegment StartX=137.45 StartY=137.45 StartZ=0 EndX=137.45 EndY=137.55 EndZ=0
    g4: LineSegment StartX=137.45 StartY=137.55 StartZ=0 EndX=137.55 EndY=137.55 EndZ=0
  constraints (14):
    c: Coincident(g1,g2)
    c: Horizontal(g2)
    c: Vertical(g1)
    c: DistanceX(g2,g2) = 0.1
    c: DistanceX(g2,g0) = 0.05
    c: DistanceY(g1,g1) = 0.1
    c: DistanceY(g1,g0) = -0.05
    c: DistanceX(g0) = 137.5
    c: DistanceY(g0) = 137.5
    c: Coincident(g3,g2)
    c: Vertical(g3)
    c: Coincident(g4,g3)
    c: Coincident(g4,g1)
    c: Horizontal(g4)
FEATURE [Part::Loft] Loft021  label="outerLayer017"
  Closed = false
  MaxDegree = 5
  Ruled = false
  Sections = -> [Sketch083,Sketch084]
  Solid = true
FEATURE [Sketcher::SketchObject] Sketch085
  FullyConstrained = true
  sketch-geometry (4):
    g0: LineSegment StartX=0 StartY=275 StartZ=0 EndX=275 EndY=275 EndZ=0
    g1: LineSegment StartX=275 StartY=275 StartZ=0 EndX=275 EndY=0 EndZ=0
    g2: LineSegment StartX=275 StartY=0 StartZ=0 EndX=0 EndY=0 EndZ=0
    g3: LineSegment StartX=0 StartY=0 StartZ=0 EndX=0 EndY=275 EndZ=0
  constraints (11):
    c: Coincident(g0,g1)
    c: Coincident(g1,g2)
    c: Coincident(g2,g3)
    c: Coincident(g3,g0)
    c: Horizontal(g0)
    c: Horizontal(g2)
    c: Vertical(g1)
    c: Vertical(g3)
    c: Coincident(g2,g-1)
    c: DistanceX(g2,g2) = 275
    c: DistanceY(g3,g3) = 275
FEATURE [Sketcher::SketchObject] Sketch086
  FullyConstrained = true
  Placement = pos=(0,0,175.1) rot=(0,0,1;0rad)
  sketch-geometry (5):
    g0: GeomPoint X=137.5 Y=137.5 Z=0
    g1: LineSegment StartX=137.55 StartY=137.55 StartZ=0 EndX=137.55 EndY=137.45 EndZ=0
    g2: LineSegment StartX=137.55 StartY=137.45 StartZ=0 EndX=137.45 EndY=137.45 EndZ=0
    g3: LineSegment StartX=137.45 StartY=137.45 StartZ=0 EndX=137.45 EndY=137.55 EndZ=0
    g4: LineSegment StartX=137.45 StartY=137.55 StartZ=0 EndX=137.55 EndY=137.55 EndZ=0
  constraints (14):
    c: Coincident(g1,g2)
    c: Horizontal(g2)
    c: Vertical(g1)
    c: DistanceX(g2,g2) = 0.1
    c: DistanceX(g2,g0) = 0.05
    c: DistanceY(g1,g1) = 0.1
    c: DistanceY(g1,g0) = -0.05
    c: DistanceX(g0) = 137.5
    c: DistanceY(g0) = 137.5
    c: Coincident(g3,g2)
    c: Vertical(g3)
    c: Coincident(g4,g3)
    c: Coincident(g4,g1)
    c: Horizontal(g4)
FEATURE [Part::Loft] Loft022  label="outerLayer018"
  Closed = false
  MaxDegree = 5
  Placement = pos=(0,0,-8) rot=(0,0,1;0rad)
  Ruled = false
  Sections = -> [Sketch085,Sketch086]
  Solid = true
FEATURE [Part::Cut] Cut010  label="Shell047"
  Base = -> Loft021
  Tool = -> Loft022
FEATURE [Sketcher::SketchObject] Sketch087
  FullyConstrained = true
  sketch-geometry (4):
    g0: LineSegment StartX=0 StartY=275 StartZ=0 EndX=275 EndY=275 EndZ=0
    g1: LineSegment StartX=275 StartY=275 StartZ=0 EndX=275 EndY=0 EndZ=0
    g2: LineSegment StartX=275 StartY=0 StartZ=0 EndX=0 EndY=0 EndZ=0
    g3: LineSegment StartX=0 StartY=0 StartZ=0 EndX=0 EndY=275 EndZ=0
  constraints (11):
    c: Coincident(g0,g1)
    c: Coincident(g1,g2)
    c: Coincident(g2,g3)
    c: Coincident(g3,g0)
    c: Horizontal(g0)
    c: Horizontal(g2)
    c: Vertical(g1)
    c: Vertical(g3)
    c: Coincident(g2,g-1)
    c: DistanceX(g2,g2) = 275
    c: DistanceY(g3,g3) = 275
FEATURE [Sketcher::SketchObject] Sketch088
  FullyConstrained = true
  Placement = pos=(0,0,175.1) rot=(0,0,1;0rad)
  sketch-geometry (5):
    g0: GeomPoint X=137.5 Y=137.5 Z=0
    g1: LineSegment StartX=137.55 StartY=137.55 StartZ=0 EndX=137.55 EndY=137.45 EndZ=0
    g2: LineSegment StartX=137.55 StartY=137.45 StartZ=0 EndX=137.45 EndY=137.45 EndZ=0
    g3: LineSegment StartX=137.45 StartY=137.45 StartZ=0 EndX=137.45 EndY=137.55 EndZ=0
    g4: LineSegment StartX=137.45 StartY=137.55 StartZ=0 EndX=137.55 EndY=137.55 EndZ=0
  constraints (14):
    c: Coincident(g1,g2)
    c: Horizontal(g2)
    c: Vertical(g1)
    c: DistanceX(g2,g2) = 0.1
    c: DistanceX(g2,g0) = 0.05
    c: DistanceY(g1,g1) = 0.1
    c: DistanceY(g1,g0) = -0.05
    c: DistanceX(g0) = 137.5
    c: DistanceY(g0) = 137.5
    c: Coincident(g3,g2)
    c: Vertical(g3)
    c: Coincident(g4,g3)
    c: Coincident(g4,g1)
    c: Horizontal(g4)
FEATURE [Part::Loft] Loft015  label="outerLayer019"
  Closed = false
  MaxDegree = 5
  Ruled = false
  Sections = -> [Sketch087,Sketch088]
  Solid = true
FEATURE [Part::MultiCommon] Common018
  Shapes = -> [Loft015,Box002]
FEATURE [Part::MultiCommon] Common019
  Shapes = -> [Cut010,Common018]
FEATURE [Sketcher::SketchObject] Sketch089
  FullyConstrained = true
  sketch-geometry (4):
    g0: LineSegment StartX=0 StartY=275 StartZ=0 EndX=275 EndY=275 EndZ=0
    g1: LineSegment StartX=275 StartY=275 StartZ=0 EndX=275 EndY=0 EndZ=0
    g2: LineSegment StartX=275 StartY=0 StartZ=0 EndX=0 EndY=0 EndZ=0
    g3: LineSegment StartX=0 StartY=0 StartZ=0 EndX=0 EndY=275 EndZ=0
  constraints (11):
    c: Coincident(g0,g1)
    c: Coincident(g1,g2)
    c: Coincident(g2,g3)
    c: Coincident(g3,g0)
    c: Horizontal(g0)
    c: Horizontal(g2)
    c: Vertical(g1)
    c: Vertical(g3)
    c: Coincident(g2,g-1)
    c: DistanceX(g2,g2) = 275
    c: DistanceY(g3,g3) = 275
FEATURE [Sketcher::SketchObject] Sketch090
  FullyConstrained = true
  Placement = pos=(0,0,175.1) rot=(0,0,1;0rad)
  sketch-geometry (5):
    g0: GeomPoint X=137.5 Y=137.5 Z=0
    g1: LineSegment StartX=137.55 StartY=137.55 StartZ=0 EndX=137.55 EndY=137.45 EndZ=0
    g2: LineSegment StartX=137.55 StartY=137.45 StartZ=0 EndX=137.45 EndY=137.45 EndZ=0
    g3: LineSegment StartX=137.45 StartY=137.45 StartZ=0 EndX=137.45 EndY=137.55 EndZ=0
    g4: LineSegment StartX=137.45 StartY=137.55 StartZ=0 EndX=137.55 EndY=137.55 EndZ=0
  constraints (14):
    c: Coincident(g1,g2)
    c: Horizontal(g2)
    c: Vertical(g1)
    c: DistanceX(g2,g2) = 0.1
    c: DistanceX(g2,g0) = 0.05
    c: DistanceY(g1,g1) = 0.1
    c: DistanceY(g1,g0) = -0.05
    c: DistanceX(g0) = 137.5
    c: DistanceY(g0) = 137.5
    c: Coincident(g3,g2)
    c: Vertical(g3)
    c: Coincident(g4,g3)
    c: Coincident(g4,g1)
    c: Horizontal(g4)
FEATURE [Part::Loft] Loft016  label="outerLayer020"
  Closed = false
  MaxDegree = 5
  Placement = pos=(0,0,-4.25) rot=(0,0,1;0rad)
  Ruled = false
  Sections = -> [Sketch089,Sketch090]
  Solid = true
FEATURE [Part::MultiCommon] Common020
  Shapes = -> [Loft016,Box003]
FEATURE [Part::MultiFuse] Fusion069
  Shapes = -> [Common020,Box004]
FEATURE [Part::MultiCommon] Common021  label="bottomShellKeep"
  Shapes = -> [Common019,Fusion069]
FEATURE [Part::Box] Box  label="Cube007"
  AttacherType = Attacher::AttachEngine3D
  Height = 60
  Length = 275
  Width = 275
FEATURE [Part::Box] Box001  label="Cube008"
  AttacherType = Attacher::AttachEngine3D
  Height = 64
  Length = 275
  Width = 275
FEATURE [Sketcher::SketchObject] Sketch091
  FullyConstrained = true
  sketch-geometry (4):
    g0: LineSegment StartX=0 StartY=275 StartZ=0 EndX=275 EndY=275 EndZ=0
    g1: LineSegment StartX=275 StartY=275 StartZ=0 EndX=275 EndY=0 EndZ=0
    g2: LineSegment StartX=275 StartY=0 StartZ=0 EndX=0 EndY=0 EndZ=0
    g3: LineSegment StartX=0 StartY=0 StartZ=0 EndX=0 EndY=275 EndZ=0
  constraints (11):
    c: Coincident(g0,g1)
    c: Coincident(g1,g2)
    c: Coincident(g2,g3)
    c: Coincident(g3,g0)
    c: Horizontal(g0)
    c: Horizontal(g2)
    c: Vertical(g1)
    c: Vertical(g3)
    c: Coincident(g2,g-1)
    c: DistanceX(g2,g2) = 275
    c: DistanceY(g3,g3) = 275
FEATURE [Sketcher::SketchObject] Sketch092
  FullyConstrained = true
  Placement = pos=(0,0,175.1) rot=(0,0,1;0rad)
  sketch-geometry (5):
    g0: GeomPoint X=137.5 Y=137.5 Z=0
    g1: LineSegment StartX=137.55 StartY=137.55 StartZ=0 EndX=137.55 EndY=137.45 EndZ=0
    g2: LineSegment StartX=137.55 StartY=137.45 StartZ=0 EndX=137.45 EndY=137.45 EndZ=0
    g3: LineSegment StartX=137.45 StartY=137.45 StartZ=0 EndX=137.45 EndY=137.55 EndZ=0
    g4: LineSegment StartX=137.45 StartY=137.55 StartZ=0 EndX=137.55 EndY=137.55 EndZ=0
  constraints (14):
    c: Coincident(g1,g2)
    c: Horizontal(g2)
    c: Vertical(g1)
    c: DistanceX(g2,g2) = 0.1
    c: DistanceX(g2,g0) = 0.05
    c: DistanceY(g1,g1) = 0.1
    c: DistanceY(g1,g0) = -0.05
    c: DistanceX(g0) = 137.5
    c: DistanceY(g0) = 137.5
    c: Coincident(g3,g2)
    c: Vertical(g3)
    c: Coincident(g4,g3)
    c: Coincident(g4,g1)
    c: Horizontal(g4)
FEATURE [Part::Loft] Loft023  label="outerLayer021"
  Closed = false
  MaxDegree = 5
  Ruled = false
  Sections = -> [Sketch091,Sketch092]
  Solid = true
FEATURE [Sketcher::SketchObject] Sketch093
  FullyConstrained = true
  Placement = pos=(0,0,0) rot=(1,0,0;1.5708rad)
  sketch-geometry (36):
    g0: LineSegment StartX=50 StartY=66 StartZ=0 EndX=97.5 EndY=93.4241 EndZ=0
    g1: LineSegment StartX=97.5 StartY=93.4241 StartZ=0 EndX=97.5 EndY=97.4241 EndZ=0
    g2: LineSegment StartX=97.5 StartY=97.4241 StartZ=0 EndX=50 EndY=70 EndZ=0
    g3: LineSegment StartX=50 StartY=70 StartZ=0 EndX=50 EndY=66 EndZ=0
    g4: LineSegment StartX=50 StartY=78 StartZ=0 EndX=97.5 EndY=105.424 EndZ=0
    g5: LineSegment StartX=97.5 StartY=105.424 StartZ=0 EndX=97.5 EndY=101.424 EndZ=0
    g6: LineSegment StartX=97.5 StartY=101.424 StartZ=0 EndX=50 EndY=74 EndZ=0
    g7: LineSegment StartX=50 StartY=78 StartZ=0 EndX=50 EndY=74 EndZ=0
    g8: LineSegment StartX=50 StartY=86 StartZ=0 EndX=50 EndY=82 EndZ=0
    g9: LineSegment StartX=50 StartY=82 StartZ=0 EndX=97.5 EndY=109.424 EndZ=0
    g10: LineSegment StartX=97.5 StartY=109.424 StartZ=0 EndX=97.5 EndY=113.424 EndZ=0
    g11: LineSegment StartX=97.5 StartY=113.424 StartZ=0 EndX=50 EndY=86 EndZ=0
    g12: LineSegment StartX=75 StartY=120.424 StartZ=0 EndX=137.5 EndY=156.509 EndZ=0
    g13: LineSegment StartX=75 StartY=120.424 StartZ=0 EndX=75 EndY=116.424 EndZ=0
    g14: LineSegment StartX=75 StartY=116.424 StartZ=0 EndX=137.5 EndY=152.509 EndZ=0
    g15: LineSegment StartX=75 StartY=112.424 StartZ=0 EndX=137.5 EndY=148.509 EndZ=0
    g16: LineSegment StartX=137.5 StartY=144.509 StartZ=0 EndX=75 EndY=108.424 EndZ=0
    g17: LineSegment StartX=75 StartY=108.424 StartZ=0 EndX=75 EndY=112.424 EndZ=0
    g18: LineSegment StartX=137.5 StartY=156.509 StartZ=0 EndX=200 EndY=120.424 EndZ=0
    g19: LineSegment StartX=200 StartY=120.424 StartZ=0 EndX=200 EndY=116.424 EndZ=0
    g20: LineSegment StartX=200 StartY=116.424 StartZ=0 EndX=137.5 EndY=152.509 EndZ=0
    g21: LineSegment StartX=137.5 StartY=148.509 StartZ=0 EndX=200 EndY=112.424 EndZ=0
    g22: LineSegment StartX=200 StartY=112.424 StartZ=0 EndX=200 EndY=108.424 EndZ=0
    g23: LineSegment StartX=200 StartY=108.424 StartZ=0 EndX=137.5 EndY=144.509 EndZ=0
    g24: LineSegment StartX=177.5 StartY=113.424 StartZ=0 EndX=225 EndY=86 EndZ=0
    g25: LineSegment StartX=225 StartY=86 StartZ=0 EndX=225 EndY=82 EndZ=0
    g26: LineSegment StartX=225 StartY=82 StartZ=0 EndX=177.5 EndY=109.424 EndZ=0
    g27: LineSegment StartX=177.5 StartY=109.424 StartZ=0 EndX=177.5 EndY=113.424 EndZ=0
    g28: LineSegment StartX=177.5 StartY=105.424 StartZ=0 EndX=225 EndY=78 EndZ=0
    g29: LineSegment StartX=225 StartY=78 StartZ=0 EndX=225 EndY=74 EndZ=0
    g30: LineSegment StartX=225 StartY=74 StartZ=0 EndX=177.5 EndY=101.424 EndZ=0
    g31: LineSegment StartX=177.5 StartY=101.424 StartZ=0 EndX=177.5 EndY=105.424 EndZ=0
    g32: LineSegment StartX=177.5 StartY=97.4241 StartZ=0 EndX=225 EndY=70 EndZ=0
    g33: LineSegment StartX=225 StartY=70 StartZ=0 EndX=225 EndY=66 EndZ=0
    g34: LineSegment StartX=225 StartY=66 StartZ=0 EndX=177.5 EndY=93.4241 EndZ=0
    g35: LineSegment StartX=177.5 StartY=97.4241 StartZ=0 EndX=177.5 EndY=93.4241 EndZ=0
  constraints (108):
    c: Angle(g0) = 0.523599
    c: DistanceX(g0) = 50
    c: Coincident(g1,g0)
    c: Vertical(g1)
    c: Coincident(g2,g1)
    c: Coincident(g3,g2)
    c: Vertical(g3)
    c: DistanceY(g0,g2) = 4
    c: Parallel(g0,g2)
    c: Coincident(g0,g3)
    c: Coincident(g5,g4)
    c: Coincident(g7,g4)
    c: Coincident(g7,g6)
    c: Coincident(g10,g9)
    c: Coincident(g11,g8)
    c: Vertical(g8)
    c: Vertical(g7)
    c: Vertical(g5)
    c: Vertical(g10)
    c: Coincident(g5,g6)
    c: Coincident(g10,g11)
    c: Coincident(g8,g9)
    c: Parallel(g2,g6)
    c: Parallel(g6,g4)
    c: Parallel(g4,g9)
    c: Parallel(g9,g11)
    c: DistanceX(g6,g2) = 0
    c: DistanceX(g8,g4) = 0
    c: DistanceY(g2,g6) = 4
    c: DistanceY(g6,g4) = 4
    c: DistanceY(g4,g8) = 4
    c: DistanceY(g8,g8) = 4
    c: DistanceX(g5,g1) = 0
    c: DistanceX(g4,g9) = 0
    c: DistanceY(g0) = 66
    c: Coincident(g13,g12)
    c: Vertical(g13)
    c: Coincident(g17,g16)
    c: Coincident(g17,g15)
    c: DistanceY(g16,g10) = 5
    c: Vertical(g17)
    c: Parallel(g16,g11)
    c: DistanceY(g16,g15) = 4
    c: DistanceY(g15,g13) = 4
    c: Coincident(g13,g14)
    c: Parallel(g12,g14)
    c: Parallel(g14,g15)
    c: Parallel(g15,g16)
    c: DistanceY(g13,g12) = 4
    c: DistanceX(g15,g13) = 0
    c: DistanceX(g16,g16) = 62.5
    c: DistanceX(g14,g15) = 0
    c: Coincident(g18,g12)
    c: Coincident(g19,g18)
    c: Vertical(g19)
    c: Coincident(g20,g19)
    c: Coincident(g20,g14)
    c: Coincident(g21,g15)
    c: Coincident(g22,g21)
    c: Coincident(g23,g22)
    c: Coincident(g23,g16)
    c: Parallel(g23,g21)
    c: Parallel(g21,g20)
    c: Parallel(g20,g18)
    c: DistanceX(g14,g12) = 0
    c: DistanceX(g21,g19) = 0
    c: Vertical(g22)
    c: Coincident(g25,g24)
    c: Coincident(g26,g25)
    c: Coincident(g27,g26)
    c: Coincident(g27,g24)
    c: Vertical(g27)
    c: Coincident(g29,g28)
    c: Vertical(g29)
    c: Coincident(g31,g30)
    c: Coincident(g31,g28)
    c: Coincident(g33,g32)
    c: Vertical(g33)
    c: Coincident(g34,g33)
    c: Coincident(g35,g32)
    c: Coincident(g35,g34)
    c: DistanceY(g10,g24) = 0
    c: Vertical(g35)
    c: Vertical(g31)
    c: DistanceX(g28,g24) = 0
    c: DistanceX(g32,g30) = 0
    c: Vertical(g25)
    c: DistanceY(g26,g24) = 4
    c: DistanceY(g28,g26) = 4
    c: DistanceY(g30,g28) = 4
    c: DistanceY(g32,g30) = 4
    c: DistanceY(g34,g32) = 4
    c: Parallel(g34,g32)
    c: Parallel(g32,g30)
    c: Parallel(g30,g28)
    c: Parallel(g28,g26)
    c: Parallel(g26,g24)
    c: Parallel(g24,g23)
    c: Coincident(g29,g30)
    c: DistanceY(g33,g0) = 0
    c: DistanceX(g32,g29) = 0
    c: DistanceX(g28,g25) = 0
    c: DistanceX(g12) = 137.5
    c: DistanceY(g16,g15) = 4
    c: DistanceX(g12,g18) = 125
    c: DistanceY(g22,g16) = 0
    c: DistanceX(g10) = 97.5
    c: DistanceX(g10,g24) = 80
FEATURE [Part::Extrusion] Extrude034
  Base = -> Sketch093
  Dir = (0,-1,2e-16)
  DirMode = 2
  FaceMakerClass = Part::FaceMakerBullseye
  LengthFwd = 275
  LengthRev = 0
  Reversed = true
  Solid = true
  Symmetric = false
FEATURE [Sketcher::SketchObject] Sketch094
  FullyConstrained = true
  Placement = pos=(0,0,0) rot=(1,0,0;1.5708rad)
  sketch-geometry (36):
    g0: LineSegment StartX=50 StartY=66 StartZ=0 EndX=97.5 EndY=93.4241 EndZ=0
    g1: LineSegment StartX=97.5 StartY=93.4241 StartZ=0 EndX=97.5 EndY=97.4241 EndZ=0
    g2: LineSegment StartX=97.5 StartY=97.4241 StartZ=0 EndX=50 EndY=70 EndZ=0
    g3: LineSegment StartX=50 StartY=70 StartZ=0 EndX=50 EndY=66 EndZ=0
    g4: LineSegment StartX=50 StartY=78 StartZ=0 EndX=97.5 EndY=105.424 EndZ=0
    g5: LineSegment StartX=97.5 StartY=105.424 StartZ=0 EndX=97.5 EndY=101.424 EndZ=0
    g6: LineSegment StartX=97.5 StartY=101.424 StartZ=0 EndX=50 EndY=74 EndZ=0
    g7: LineSegment StartX=50 StartY=78 StartZ=0 EndX=50 EndY=74 EndZ=0
    g8: LineSegment StartX=50 StartY=86 StartZ=0 EndX=50 EndY=82 EndZ=0
    g9: LineSegment StartX=50 StartY=82 StartZ=0 EndX=97.5 EndY=109.424 EndZ=0
    g10: LineSegment StartX=97.5 StartY=109.424 StartZ=0 EndX=97.5 EndY=113.424 EndZ=0
    g11: LineSegment StartX=97.5 StartY=113.424 StartZ=0 EndX=50 EndY=86 EndZ=0
    g12: LineSegment StartX=75 StartY=120.424 StartZ=0 EndX=75 EndY=116.424 EndZ=0
    g13: LineSegment StartX=75 StartY=112.424 StartZ=0 EndX=137.5 EndY=148.509 EndZ=0
    g14: LineSegment StartX=137.5 StartY=144.509 StartZ=0 EndX=75 EndY=108.424 EndZ=0
    g15: LineSegment StartX=75 StartY=108.424 StartZ=0 EndX=75 EndY=112.424 EndZ=0
    g16: LineSegment StartX=137.5 StartY=148.509 StartZ=0 EndX=200 EndY=112.424 EndZ=0
    g17: LineSegment StartX=200 StartY=112.424 StartZ=0 EndX=200 EndY=108.424 EndZ=0
    g18: LineSegment StartX=200 StartY=108.424 StartZ=0 EndX=137.5 EndY=144.509 EndZ=0
    g19: LineSegment StartX=177.5 StartY=113.424 StartZ=0 EndX=225 EndY=86 EndZ=0
    g20: LineSegment StartX=225 StartY=86 StartZ=0 EndX=225 EndY=82 EndZ=0
    g21: LineSegment StartX=225 StartY=82 StartZ=0 EndX=177.5 EndY=109.424 EndZ=0
    g22: LineSegment StartX=177.5 StartY=109.424 StartZ=0 EndX=177.5 EndY=113.424 EndZ=0
    g23: LineSegment StartX=177.5 StartY=105.424 StartZ=0 EndX=225 EndY=78 EndZ=0
    g24: LineSegment StartX=225 StartY=78 StartZ=0 EndX=225 EndY=74 EndZ=0
    g25: LineSegment StartX=225 StartY=74 StartZ=0 EndX=177.5 EndY=101.424 EndZ=0
    g26: LineSegment StartX=177.5 StartY=101.424 StartZ=0 EndX=177.5 EndY=105.424 EndZ=0
    g27: LineSegment StartX=177.5 StartY=97.4241 StartZ=0 EndX=225 EndY=70 EndZ=0
    g28: LineSegment StartX=225 StartY=70 StartZ=0 EndX=225 EndY=66 EndZ=0
    g29: LineSegment StartX=225 StartY=66 StartZ=0 EndX=177.5 EndY=93.4241 EndZ=0
    g30: LineSegment StartX=177.5 StartY=97.4241 StartZ=0 EndX=177.5 EndY=93.4241 EndZ=0
    g31: LineSegment StartX=75 StartY=116.424 StartZ=0 EndX=137.5 EndY=152.509 EndZ=0
    g32: LineSegment StartX=137.5 StartY=152.509 StartZ=0 EndX=200 EndY=116.424 EndZ=0
    g33: LineSegment StartX=200 StartY=116.424 StartZ=0 EndX=200 EndY=120.424 EndZ=0
    g34: LineSegment StartX=200 StartY=120.424 StartZ=0 EndX=137.5 EndY=156.509 EndZ=0
    g35: LineSegment StartX=137.5 StartY=156.509 StartZ=0 EndX=75 EndY=120.424 EndZ=0
  constraints (108):
    c: Angle(g0) = 0.523599
    c: DistanceX(g0) = 50
    c: Coincident(g1,g0)
    c: Vertical(g1)
    c: Coincident(g2,g1)
    c: Coincident(g3,g2)
    c: Vertical(g3)
    c: DistanceY(g0,g2) = 4
    c: Parallel(g0,g2)
    c: Coincident(g0,g3)
    c: Coincident(g5,g4)
    c: Coincident(g7,g4)
    c: Coincident(g7,g6)
    c: Coincident(g10,g9)
    c: Coincident(g11,g8)
    c: Vertical(g8)
    c: Vertical(g7)
    c: Vertical(g5)
    c: Vertical(g10)
    c: Coincident(g5,g6)
    c: Coincident(g10,g11)
    c: Coincident(g8,g9)
    c: Parallel(g2,g6)
    c: Parallel(g6,g4)
    c: Parallel(g4,g9)
    c: Parallel(g9,g11)
    c: DistanceX(g6,g2) = 0
    c: DistanceX(g8,g4) = 0
    c: DistanceY(g2,g6) = 4
    c: DistanceY(g6,g4) = 4
    c: DistanceY(g4,g8) = 4
    c: DistanceY(g8,g8) = 4
    c: DistanceX(g5,g1) = 0
    c: DistanceX(g4,g9) = 0
    c: DistanceY(g0) = 66
    c: Vertical(g12)
    c: Coincident(g15,g14)
    c: Coincident(g15,g13)
    c: DistanceY(g14,g10) = 5
    c: Vertical(g15)
    c: Parallel(g14,g11)
    c: DistanceY(g14,g13) = 4
    c: DistanceY(g13,g12) = 4
    c: Parallel(g13,g14)
    c: DistanceY(g12,g12) = 4
    c: DistanceX(g13,g12) = 0
    c: DistanceX(g14,g14) = 62.5
    c: Coincident(g16,g13)
    c: Coincident(g17,g16)
    c: Coincident(g18,g17)
    c: Coincident(g18,g14)
    c: Parallel(g18,g16)
    c: Vertical(g17)
    c: Coincident(g20,g19)
    c: Coincident(g21,g20)
    c: Coincident(g22,g21)
    c: Coincident(g22,g19)
    c: Vertical(g22)
    c: Coincident(g24,g23)
    c: Vertical(g24)
    c: Coincident(g26,g25)
    c: Coincident(g26,g23)
    c: Coincident(g28,g27)
    c: Vertical(g28)
    c: Coincident(g29,g28)
    c: Coincident(g30,g27)
    c: Coincident(g30,g29)
    c: DistanceY(g10,g19) = 0
    c: Vertical(g30)
    c: Vertical(g26)
    c: DistanceX(g23,g19) = 0
    c: DistanceX(g27,g25) = 0
    c: Vertical(g20)
    c: DistanceY(g21,g19) = 4
    c: DistanceY(g23,g21) = 4
    c: DistanceY(g25,g23) = 4
    c: DistanceY(g27,g25) = 4
    c: DistanceY(g29,g27) = 4
    c: Parallel(g29,g27)
    c: Parallel(g27,g25)
    c: Parallel(g25,g23)
    c: Parallel(g23,g21)
    c: Parallel(g21,g19)
    c: Parallel(g19,g18)
    c: Coincident(g24,g25)
    c: DistanceY(g28,g0) = 0
    c: DistanceX(g27,g24) = 0
    c: DistanceX(g23,g20) = 0
    c: DistanceX(g13) = 137.5
    c: DistanceX(g14,g10) = 22.5
    c: DistanceX(g19,g17) = 22.5
    c: DistanceX(g14,g17) = 125
    c: DistanceX(g14,g13) = 0
    c: DistanceY(g17,g14) = 0
    c: Coincident(g31,g12)
    c: Coincident(g32,g31)
    c: Vertical(g33)
    c: Coincident(g34,g33)
    c: Coincident(g35,g12)
    c: DistanceX(g13,g31) = 0
    c: Coincident(g34,g35)
    c: DistanceX(g34,g31) = 0
    c: Parallel(g13,g31)
    c: Parallel(g31,g35)
    c: Parallel(g16,g32)
    c: Parallel(g32,g34)
    c: Coincident(g32,g33)
    c: DistanceX(g16,g32) = 0
FEATURE [Part::Extrusion] Extrude035
  Base = -> Sketch094
  Dir = (0,-1,2e-16)
  DirMode = 2
  FaceMakerClass = Part::FaceMakerBullseye
  LengthFwd = 275
  LengthRev = 0
  Placement = pos=(275,0,0) rot=(0,0,1;1.5708rad)
  Reversed = true
  Solid = true
  Symmetric = false
FEATURE [Part::MultiFuse] Fusion070  label="keeps-legacy001"
  Shapes = -> [Extrude034,Extrude035]
FEATURE [Sketcher::SketchObject] Sketch095
  FullyConstrained = true
  sketch-geometry (4):
    g0: LineSegment StartX=0 StartY=275 StartZ=0 EndX=275 EndY=275 EndZ=0
    g1: LineSegment StartX=275 StartY=275 StartZ=0 EndX=275 EndY=0 EndZ=0
    g2: LineSegment StartX=275 StartY=0 StartZ=0 EndX=0 EndY=0 EndZ=0
    g3: LineSegment StartX=0 StartY=0 StartZ=0 EndX=0 EndY=275 EndZ=0
  constraints (11):
    c: Coincident(g0,g1)
    c: Coincident(g1,g2)
    c: Coincident(g2,g3)
    c: Coincident(g3,g0)
    c: Horizontal(g0)
    c: Horizontal(g2)
    c: Vertical(g1)
    c: Vertical(g3)
    c: Coincident(g2,g-1)
    c: DistanceX(g2,g2) = 275
    c: DistanceY(g3,g3) = 275
FEATURE [Sketcher::SketchObject] Sketch096
  FullyConstrained = true
  Placement = pos=(0,0,175.1) rot=(0,0,1;0rad)
  sketch-geometry (5):
    g0: GeomPoint X=137.5 Y=137.5 Z=0
    g1: LineSegment StartX=137.55 StartY=137.55 StartZ=0 EndX=137.55 EndY=137.45 EndZ=0
    g2: LineSegment StartX=137.55 StartY=137.45 StartZ=0 EndX=137.45 EndY=137.45 EndZ=0
    g3: LineSegment StartX=137.45 StartY=137.45 StartZ=0 EndX=137.45 EndY=137.55 EndZ=0
    g4: LineSegment StartX=137.45 StartY=137.55 StartZ=0 EndX=137.55 EndY=137.55 EndZ=0
  constraints (14):
    c: Coincident(g1,g2)
    c: Horizontal(g2)
    c: Vertical(g1)
    c: DistanceX(g2,g2) = 0.1
    c: DistanceX(g2,g0) = 0.05
    c: DistanceY(g1,g1) = 0.1
    c: DistanceY(g1,g0) = -0.05
    c: DistanceX(g0) = 137.5
    c: DistanceY(g0) = 137.5
    c: Coincident(g3,g2)
    c: Vertical(g3)
    c: Coincident(g4,g3)
    c: Coincident(g4,g1)
    c: Horizontal(g4)
FEATURE [Part::Loft] Loft024  label="outerLayer022"
  Closed = false
  MaxDegree = 5
  Ruled = false
  Sections = -> [Sketch095,Sketch096]
  Solid = true
FEATURE [Sketcher::SketchObject] Sketch097
  FullyConstrained = true
  sketch-geometry (4):
    g0: LineSegment StartX=0 StartY=275 StartZ=0 EndX=275 EndY=275 EndZ=0
    g1: LineSegment StartX=275 StartY=275 StartZ=0 EndX=275 EndY=0 EndZ=0
    g2: LineSegment StartX=275 StartY=0 StartZ=0 EndX=0 EndY=0 EndZ=0
    g3: LineSegment StartX=0 StartY=0 StartZ=0 EndX=0 EndY=275 EndZ=0
  constraints (11):
    c: Coincident(g0,g1)
    c: Coincident(g1,g2)
    c: Coincident(g2,g3)
    c: Coincident(g3,g0)
    c: Horizontal(g0)
    c: Horizontal(g2)
    c: Vertical(g1)
    c: Vertical(g3)
    c: Coincident(g2,g-1)
    c: DistanceX(g2,g2) = 275
    c: DistanceY(g3,g3) = 275
FEATURE [Sketcher::SketchObject] Sketch098
  FullyConstrained = true
  Placement = pos=(0,0,175.1) rot=(0,0,1;0rad)
  sketch-geometry (5):
    g0: GeomPoint X=137.5 Y=137.5 Z=0
    g1: LineSegment StartX=137.55 StartY=137.55 StartZ=0 EndX=137.55 EndY=137.45 EndZ=0
    g2: LineSegment StartX=137.55 StartY=137.45 StartZ=0 EndX=137.45 EndY=137.45 EndZ=0
    g3: LineSegment StartX=137.45 StartY=137.45 StartZ=0 EndX=137.45 EndY=137.55 EndZ=0
    g4: LineSegment StartX=137.45 StartY=137.55 StartZ=0 EndX=137.55 EndY=137.55 EndZ=0
  constraints (14):
    c: Coincident(g1,g2)
    c: Horizontal(g2)
    c: Vertical(g1)
    c: DistanceX(g2,g2) = 0.1
    c: DistanceX(g2,g0) = 0.05
    c: DistanceY(g1,g1) = 0.1
    c: DistanceY(g1,g0) = -0.05
    c: DistanceX(g0) = 137.5
    c: DistanceY(g0) = 137.5
    c: Coincident(g3,g2)
    c: Vertical(g3)
    c: Coincident(g4,g3)
    c: Coincident(g4,g1)
    c: Horizontal(g4)
FEATURE [Part::Loft] Loft025  label="outerLayer023"
  Closed = false
  MaxDegree = 5
  Placement = pos=(0,0,-8) rot=(0,0,1;0rad)
  Ruled = false
  Sections = -> [Sketch097,Sketch098]
  Solid = true
FEATURE [Part::Cut] Cut011  label="Shell048"
  Base = -> Loft024
  Tool = -> Loft025
FEATURE [Part::MultiCommon] Common022  label="keepLegacy001"
  Shapes = -> [Fusion070,Cut011]
FEATURE [Sketcher::SketchObject] Sketch099
  FullyConstrained = true
  Placement = pos=(0,0,0) rot=(1,0,0;1.5708rad)
  sketch-geometry (28):
    g0: LineSegment StartX=50 StartY=70 StartZ=0 EndX=97.5 EndY=97.4241 EndZ=0
    g1: LineSegment StartX=97.5 StartY=97.4241 StartZ=0 EndX=97.5 EndY=101.424 EndZ=0
    g2: LineSegment StartX=97.5 StartY=101.424 StartZ=0 EndX=50 EndY=74 EndZ=0
    g3: LineSegment StartX=50 StartY=74 StartZ=0 EndX=50 EndY=70 EndZ=0
    g4: LineSegment StartX=50 StartY=82 StartZ=0 EndX=97.5 EndY=109.424 EndZ=0
    g5: LineSegment StartX=97.5 StartY=109.424 StartZ=0 EndX=97.5 EndY=105.424 EndZ=0
    g6: LineSegment StartX=97.5 StartY=105.424 StartZ=0 EndX=50 EndY=78 EndZ=0
    g7: LineSegment StartX=50 StartY=82 StartZ=0 EndX=50 EndY=78 EndZ=0
    g8: LineSegment StartX=75 StartY=116.424 StartZ=0 EndX=137.5 EndY=152.509 EndZ=0
    g9: LineSegment StartX=137.5 StartY=148.509 StartZ=0 EndX=75 EndY=112.424 EndZ=0
    g10: LineSegment StartX=75 StartY=112.424 StartZ=0 EndX=75 EndY=116.424 EndZ=0
    g11: LineSegment StartX=137.5 StartY=152.509 StartZ=0 EndX=200 EndY=116.424 EndZ=0
    g12: LineSegment StartX=200 StartY=116.424 StartZ=0 EndX=200 EndY=112.424 EndZ=0
    g13: LineSegment StartX=200 StartY=112.424 StartZ=0 EndX=137.5 EndY=148.509 EndZ=0
    g14: LineSegment StartX=177.5 StartY=109.424 StartZ=0 EndX=225 EndY=82 EndZ=0
    g15: LineSegment StartX=225 StartY=82 StartZ=0 EndX=225 EndY=78 EndZ=0
    g16: LineSegment StartX=225 StartY=78 StartZ=0 EndX=177.5 EndY=105.424 EndZ=0
    g17: LineSegment StartX=177.5 StartY=105.424 StartZ=0 EndX=177.5 EndY=109.424 EndZ=0
    g18: LineSegment StartX=177.5 StartY=101.424 StartZ=0 EndX=225 EndY=74 EndZ=0
    g19: LineSegment StartX=225 StartY=74 StartZ=0 EndX=225 EndY=70 EndZ=0
    g20: LineSegment StartX=225 StartY=70 StartZ=0 EndX=177.5 EndY=97.4241 EndZ=0
    g21: LineSegment StartX=177.5 StartY=101.424 StartZ=0 EndX=177.5 EndY=97.4241 EndZ=0
    g22: LineSegment StartX=75 StartY=120.424 StartZ=0 EndX=137.5 EndY=156.509 EndZ=0
    g23: LineSegment StartX=137.5 StartY=156.509 StartZ=0 EndX=200 EndY=120.424 EndZ=0
    g24: LineSegment StartX=200 StartY=120.424 StartZ=0 EndX=200 EndY=124.424 EndZ=0
    g25: LineSegment StartX=200 StartY=124.424 StartZ=0 EndX=137.5 EndY=160.509 EndZ=0
    g26: LineSegment StartX=137.5 StartY=160.509 StartZ=0 EndX=75 EndY=124.424 EndZ=0
    g27: LineSegment StartX=75 StartY=124.424 StartZ=0 EndX=75 EndY=120.424 EndZ=0
  constraints (84):
    c: Angle(g0) = 0.523599
    c: DistanceX(g0) = 50
    c: Coincident(g1,g0)
    c: Vertical(g1)
    c: Coincident(g2,g1)
    c: Coincident(g3,g2)
    c: Vertical(g3)
    c: DistanceY(g0,g2) = 4
    c: Parallel(g0,g2)
    c: Coincident(g0,g3)
    c: Coincident(g5,g4)
    c: Coincident(g7,g4)
    c: Coincident(g7,g6)
    c: Vertical(g7)
    c: Vertical(g5)
    c: Coincident(g5,g6)
    c: Parallel(g2,g6)
    c: Parallel(g6,g4)
    c: DistanceX(g6,g2) = 0
    c: DistanceY(g2,g6) = 4
    c: DistanceY(g6,g4) = 4
    c: DistanceX(g5,g1) = 0
    c: DistanceY(g0) = 70
    c: Coincident(g10,g9)
    c: Coincident(g10,g8)
    c: Vertical(g10)
    c: DistanceY(g9,g8) = 4
    c: Parallel(g8,g9)
    c: DistanceX(g9,g9) = 62.5
    c: Coincident(g11,g8)
    c: Coincident(g12,g11)
    c: Coincident(g13,g12)
    c: Coincident(g13,g9)
    c: Parallel(g13,g11)
    c: Vertical(g12)
    c: Coincident(g15,g14)
    c: Vertical(g15)
    c: Coincident(g17,g16)
    c: Coincident(g17,g14)
    c: Coincident(g19,g18)
    c: Vertical(g19)
    c: Coincident(g20,g19)
    c: Coincident(g21,g18)
    c: Coincident(g21,g20)
    c: Vertical(g21)
    c: Vertical(g17)
    c: DistanceX(g18,g16) = 0
    c: DistanceY(g16,g14) = 4
    c: DistanceY(g18,g16) = 4
    c: DistanceY(g20,g18) = 4
    c: Parallel(g20,g18)
    c: Parallel(g18,g16)
    c: Parallel(g16,g14)
    c: Coincident(g15,g16)
    c: DistanceY(g19,g0) = 0
    c: DistanceX(g18,g15) = 0
    c: DistanceY(g4,g9) = 3
    c: DistanceY(g4,g14) = 0
    c: DistanceY(g9,g12) = 0
    c: DistanceX(g9,g8) = 0
    c: Angle(g9) = -2.61799
    c: DistanceX(g9,g4) = 22.5
    c: DistanceX(g14,g12) = 22.5
    c: DistanceX(g9,g14) = 87.5
    c: DistanceX(g8) = 137.5
    c: DistanceX(g9,g12) = 125
    c: Coincident(g23,g22)
    c: Coincident(g24,g23)
    c: Vertical(g24)
    c: Coincident(g26,g25)
    c: Coincident(g27,g22)
    c: Vertical(g27)
    c: DistanceX(g22,g8) = 0
    c: DistanceX(g8,g22) = 0
    c: DistanceX(g25,g22) = 0
    c: Coincident(g24,g25)
    c: Coincident(g26,g27)
    c: DistanceY(g8,g22) = 4
    c: DistanceY(g22,g25) = 4
    c: DistanceY(g11,g23) = 4
    c: DistanceY(g23,g24) = 4
    c: DistanceX(g23,g11) = 0
    c: DistanceY(g8,g22) = 4
    c: DistanceY(g22,g26) = 4
FEATURE [Part::Extrusion] Extrude036  label="cuts022"
  Base = -> Sketch099
  Dir = (0,-1,2e-16)
  DirMode = 2
  FaceMakerClass = Part::FaceMakerBullseye
  LengthFwd = 275
  LengthRev = 0
  Reversed = true
  Solid = true
  Symmetric = false
FEATURE [Sketcher::SketchObject] Sketch100
  FullyConstrained = true
  Placement = pos=(0,0,0) rot=(1,0,0;1.5708rad)
  sketch-geometry (28):
    g0: LineSegment StartX=50 StartY=70 StartZ=0 EndX=97.5 EndY=97.4241 EndZ=0
    g1: LineSegment StartX=97.5 StartY=97.4241 StartZ=0 EndX=97.5 EndY=101.424 EndZ=0
    g2: LineSegment StartX=97.5 StartY=101.424 StartZ=0 EndX=50 EndY=74 EndZ=0
    g3: LineSegment StartX=50 StartY=74 StartZ=0 EndX=50 EndY=70 EndZ=0
    g4: LineSegment StartX=50 StartY=82 StartZ=0 EndX=97.5 EndY=109.424 EndZ=0
    g5: LineSegment StartX=97.5 StartY=109.424 StartZ=0 EndX=97.5 EndY=105.424 EndZ=0
    g6: LineSegment StartX=97.5 StartY=105.424 StartZ=0 EndX=50 EndY=78 EndZ=0
    g7: LineSegment StartX=50 StartY=82 StartZ=0 EndX=50 EndY=78 EndZ=0
    g8: LineSegment StartX=75 StartY=116.424 StartZ=0 EndX=137.5 EndY=152.509 EndZ=0
    g9: LineSegment StartX=137.5 StartY=148.509 StartZ=0 EndX=75 EndY=112.424 EndZ=0
    g10: LineSegment StartX=75 StartY=112.424 StartZ=0 EndX=75 EndY=116.424 EndZ=0
    g11: LineSegment StartX=137.5 StartY=152.509 StartZ=0 EndX=200 EndY=116.424 EndZ=0
    g12: LineSegment StartX=200 StartY=116.424 StartZ=0 EndX=200 EndY=112.424 EndZ=0
    g13: LineSegment StartX=200 StartY=112.424 StartZ=0 EndX=137.5 EndY=148.509 EndZ=0
    g14: LineSegment StartX=177.5 StartY=109.424 StartZ=0 EndX=225 EndY=82 EndZ=0
    g15: LineSegment StartX=225 StartY=82 StartZ=0 EndX=225 EndY=78 EndZ=0
    g16: LineSegment StartX=225 StartY=78 StartZ=0 EndX=177.5 EndY=105.424 EndZ=0
    g17: LineSegment StartX=177.5 StartY=105.424 StartZ=0 EndX=177.5 EndY=109.424 EndZ=0
    g18: LineSegment StartX=177.5 StartY=101.424 StartZ=0 EndX=225 EndY=74 EndZ=0
    g19: LineSegment StartX=225 StartY=74 StartZ=0 EndX=225 EndY=70 EndZ=0
    g20: LineSegment StartX=225 StartY=70 StartZ=0 EndX=177.5 EndY=97.4241 EndZ=0
    g21: LineSegment StartX=177.5 StartY=101.424 StartZ=0 EndX=177.5 EndY=97.4241 EndZ=0
    g22: LineSegment StartX=75 StartY=120.424 StartZ=0 EndX=75 EndY=124.424 EndZ=0
    g23: LineSegment StartX=75 StartY=124.424 StartZ=0 EndX=137.5 EndY=160.509 EndZ=0
    g24: LineSegment StartX=137.5 StartY=160.509 StartZ=0 EndX=200 EndY=124.424 EndZ=0
    g25: LineSegment StartX=200 StartY=124.424 StartZ=0 EndX=200 EndY=120.424 EndZ=0
    g26: LineSegment StartX=200 StartY=120.424 StartZ=0 EndX=137.5 EndY=156.509 EndZ=0
    g27: LineSegment StartX=137.5 StartY=156.509 StartZ=0 EndX=75 EndY=120.424 EndZ=0
  constraints (84):
    c: Angle(g0) = 0.523599
    c: DistanceX(g0) = 50
    c: Coincident(g1,g0)
    c: Vertical(g1)
    c: Coincident(g2,g1)
    c: Coincident(g3,g2)
    c: Vertical(g3)
    c: DistanceY(g0,g2) = 4
    c: Parallel(g0,g2)
    c: Coincident(g0,g3)
    c: Coincident(g5,g4)
    c: Coincident(g7,g4)
    c: Coincident(g7,g6)
    c: Vertical(g7)
    c: Vertical(g5)
    c: Coincident(g5,g6)
    c: Parallel(g2,g6)
    c: Parallel(g6,g4)
    c: DistanceX(g6,g2) = 0
    c: DistanceY(g2,g6) = 4
    c: DistanceY(g6,g4) = 4
    c: DistanceX(g5,g1) = 0
    c: DistanceY(g0) = 70
    c: Coincident(g10,g9)
    c: Coincident(g10,g8)
    c: Vertical(g10)
    c: DistanceY(g9,g8) = 4
    c: Parallel(g8,g9)
    c: DistanceX(g9,g9) = 62.5
    c: Coincident(g11,g8)
    c: Coincident(g12,g11)
    c: Coincident(g13,g12)
    c: Coincident(g13,g9)
    c: Parallel(g13,g11)
    c: Vertical(g12)
    c: Coincident(g15,g14)
    c: Vertical(g15)
    c: Coincident(g17,g16)
    c: Coincident(g17,g14)
    c: Coincident(g19,g18)
    c: Vertical(g19)
    c: Coincident(g20,g19)
    c: Coincident(g21,g18)
    c: Coincident(g21,g20)
    c: Vertical(g21)
    c: Vertical(g17)
    c: DistanceX(g18,g16) = 0
    c: DistanceY(g16,g14) = 4
    c: DistanceY(g18,g16) = 4
    c: DistanceY(g20,g18) = 4
    c: Parallel(g20,g18)
    c: Parallel(g18,g16)
    c: Parallel(g16,g14)
    c: Coincident(g15,g16)
    c: DistanceY(g19,g0) = 0
    c: DistanceX(g18,g15) = 0
    c: DistanceX(g14,g14) = 47.5
    c: DistanceX(g4,g4) = 47.5
    c: DistanceX(g4,g14) = 80
    c: Parallel(g9,g4)
    c: DistanceX(g9,g8) = 0
    c: DistanceY(g4,g9) = 3
    c: DistanceY(g14,g12) = 3
    c: DistanceY(g14,g4) = 0
    c: DistanceX(g8) = 137.5
    c: DistanceX(g9,g12) = 125
    c: Vertical(g22)
    c: Coincident(g23,g22)
    c: Coincident(g24,g23)
    c: Coincident(g25,g24)
    c: Vertical(g25)
    c: Coincident(g26,g25)
    c: Coincident(g27,g22)
    c: DistanceX(g22,g8) = 0
    c: DistanceY(g8,g22) = 4
    c: DistanceY(g22,g22) = 4
    c: Coincident(g26,g27)
    c: DistanceX(g26,g8) = 0
    c: DistanceY(g26,g23) = 4
    c: DistanceY(g8,g26) = 4
    c: DistanceX(g23,g26) = 0
    c: DistanceX(g25,g11) = 0
    c: DistanceY(g11,g25) = 4
    c: DistanceY(g25,g24) = 4
FEATURE [Part::Extrusion] Extrude037  label="cuts023"
  Base = -> Sketch100
  Dir = (0,-1,2e-16)
  DirMode = 2
  FaceMakerClass = Part::FaceMakerBullseye
  LengthFwd = 275
  LengthRev = 0
  Placement = pos=(275,0,0) rot=(0,0,1;1.5708rad)
  Reversed = true
  Solid = true
  Symmetric = false
FEATURE [Sketcher::SketchObject] Sketch101
  FullyConstrained = true
  Placement = pos=(0,0,0) rot=(1,0,0;1.5708rad)
  sketch-geometry (3):
    g0: LineSegment StartX=15 StartY=0 StartZ=0 EndX=260 EndY=0 EndZ=0
    g1: LineSegment StartX=260 StartY=0 StartZ=0 EndX=137.5 EndY=160 EndZ=0
    g2: LineSegment StartX=137.5 StartY=160 StartZ=0 EndX=15 EndY=0 EndZ=0
  constraints (9):
    c: Horizontal(g0)
    c: Coincident(g1,g0)
    c: Coincident(g2,g1)
    c: DistanceX(g0) = 260
    c: DistanceX(g1) = 137.5
    c: DistanceY(g1) = 160
    c: Coincident(g0,g2)
    c: DistanceY(g0,g-1) = 0
    c: DistanceX(g-1,g0) = 15
FEATURE [Part::Extrusion] Extrude038
  Base = -> Sketch101
  Dir = (0,-1,-6e-16)
  DirMode = 2
  FaceMakerClass = Part::FaceMakerBullseye
  LengthFwd = 275
  LengthRev = 0
  Placement = pos=(0,0,0) rot=(0,0,1;1.5708rad)
  Solid = true
  Symmetric = false
FEATURE [Part::MultiCommon] Common023  label="cuts018"
  Shapes = -> [Extrude038,Extrude036]
FEATURE [Sketcher::SketchObject] Sketch102
  FullyConstrained = true
  Placement = pos=(0,0,0) rot=(1,0,0;1.5708rad)
  sketch-geometry (3):
    g0: LineSegment StartX=15 StartY=0 StartZ=0 EndX=260 EndY=0 EndZ=0
    g1: LineSegment StartX=260 StartY=0 StartZ=0 EndX=137.5 EndY=160 EndZ=0
    g2: LineSegment StartX=137.5 StartY=160 StartZ=0 EndX=15 EndY=0 EndZ=0
  constraints (9):
    c: Horizontal(g0)
    c: Coincident(g1,g0)
    c: Coincident(g2,g1)
    c: DistanceX(g0) = 260
    c: DistanceX(g1) = 137.5
    c: DistanceY(g1) = 160
    c: Coincident(g0,g2)
    c: DistanceY(g0,g-1) = 0
    c: DistanceX(g-1,g0) = 15
FEATURE [Part::Extrusion] Extrude039
  Base = -> Sketch102
  Dir = (0,-1,2e-16)
  DirMode = 2
  FaceMakerClass = Part::FaceMakerBullseye
  LengthFwd = 275
  LengthRev = 0
  Reversed = true
  Solid = true
  Symmetric = false
FEATURE [Part::MultiCommon] Common024  label="cuts019"
  Shapes = -> [Extrude039,Extrude037]
FEATURE [Part::MultiFuse] Fusion071  label="cuts026"
  Shapes = -> [Common024,Common023]
FEATURE [Sketcher::SketchObject] Sketch103
  FullyConstrained = true
  sketch-geometry (4):
    g0: LineSegment StartX=0 StartY=275 StartZ=0 EndX=275 EndY=275 EndZ=0
    g1: LineSegment StartX=275 StartY=275 StartZ=0 EndX=275 EndY=0 EndZ=0
    g2: LineSegment StartX=275 StartY=0 StartZ=0 EndX=0 EndY=0 EndZ=0
    g3: LineSegment StartX=0 StartY=0 StartZ=0 EndX=0 EndY=275 EndZ=0
  constraints (11):
    c: Coincident(g0,g1)
    c: Coincident(g1,g2)
    c: Coincident(g2,g3)
    c: Coincident(g3,g0)
    c: Horizontal(g0)
    c: Horizontal(g2)
    c: Vertical(g1)
    c: Vertical(g3)
    c: Coincident(g2,g-1)
    c: DistanceX(g2,g2) = 275
    c: DistanceY(g3,g3) = 275
FEATURE [Sketcher::SketchObject] Sketch104
  FullyConstrained = true
  Placement = pos=(0,0,175.1) rot=(0,0,1;0rad)
  sketch-geometry (5):
    g0: GeomPoint X=137.5 Y=137.5 Z=0
    g1: LineSegment StartX=137.55 StartY=137.55 StartZ=0 EndX=137.55 EndY=137.45 EndZ=0
    g2: LineSegment StartX=137.55 StartY=137.45 StartZ=0 EndX=137.45 EndY=137.45 EndZ=0
    g3: LineSegment StartX=137.45 StartY=137.45 StartZ=0 EndX=137.45 EndY=137.55 EndZ=0
    g4: LineSegment StartX=137.45 StartY=137.55 StartZ=0 EndX=137.55 EndY=137.55 EndZ=0
  constraints (14):
    c: Coincident(g1,g2)
    c: Horizontal(g2)
    c: Vertical(g1)
    c: DistanceX(g2,g2) = 0.1
    c: DistanceX(g2,g0) = 0.05
    c: DistanceY(g1,g1) = 0.1
    c: DistanceY(g1,g0) = -0.05
    c: DistanceX(g0) = 137.5
    c: DistanceY(g0) = 137.5
    c: Coincident(g3,g2)
    c: Vertical(g3)
    c: Coincident(g4,g3)
    c: Coincident(g4,g1)
    c: Horizontal(g4)
FEATURE [Part::Loft] Loft026  label="outerLayer024"
  Closed = false
  MaxDegree = 5
  Ruled = false
  Sections = -> [Sketch103,Sketch104]
  Solid = true
FEATURE [Sketcher::SketchObject] Sketch105
  FullyConstrained = true
  sketch-geometry (4):
    g0: LineSegment StartX=0 StartY=275 StartZ=0 EndX=275 EndY=275 EndZ=0
    g1: LineSegment StartX=275 StartY=275 StartZ=0 EndX=275 EndY=0 EndZ=0
    g2: LineSegment StartX=275 StartY=0 StartZ=0 EndX=0 EndY=0 EndZ=0
    g3: LineSegment StartX=0 StartY=0 StartZ=0 EndX=0 EndY=275 EndZ=0
  constraints (11):
    c: Coincident(g0,g1)
    c: Coincident(g1,g2)
    c: Coincident(g2,g3)
    c: Coincident(g3,g0)
    c: Horizontal(g0)
    c: Horizontal(g2)
    c: Vertical(g1)
    c: Vertical(g3)
    c: Coincident(g2,g-1)
    c: DistanceX(g2,g2) = 275
    c: DistanceY(g3,g3) = 275
FEATURE [Sketcher::SketchObject] Sketch106
  FullyConstrained = true
  Placement = pos=(0,0,175.1) rot=(0,0,1;0rad)
  sketch-geometry (5):
    g0: GeomPoint X=137.5 Y=137.5 Z=0
    g1: LineSegment StartX=137.55 StartY=137.55 StartZ=0 EndX=137.55 EndY=137.45 EndZ=0
    g2: LineSegment StartX=137.55 StartY=137.45 StartZ=0 EndX=137.45 EndY=137.45 EndZ=0
    g3: LineSegment StartX=137.45 StartY=137.45 StartZ=0 EndX=137.45 EndY=137.55 EndZ=0
    g4: LineSegment StartX=137.45 StartY=137.55 StartZ=0 EndX=137.55 EndY=137.55 EndZ=0
  constraints (14):
    c: Coincident(g1,g2)
    c: Horizontal(g2)
    c: Vertical(g1)
    c: DistanceX(g2,g2) = 0.1
    c: DistanceX(g2,g0) = 0.05
    c: DistanceY(g1,g1) = 0.1
    c: DistanceY(g1,g0) = -0.05
    c: DistanceX(g0) = 137.5
    c: DistanceY(g0) = 137.5
    c: Coincident(g3,g2)
    c: Vertical(g3)
    c: Coincident(g4,g3)
    c: Coincident(g4,g1)
    c: Horizontal(g4)
FEATURE [Part::Loft] Loft027  label="outerLayer025"
  Closed = false
  MaxDegree = 5
  Ruled = false
  Sections = -> [Sketch105,Sketch106]
  Solid = true
FEATURE [Sketcher::SketchObject] Sketch107
  FullyConstrained = true
  sketch-geometry (4):
    g0: LineSegment StartX=0 StartY=275 StartZ=0 EndX=275 EndY=275 EndZ=0
    g1: LineSegment StartX=275 StartY=275 StartZ=0 EndX=275 EndY=0 EndZ=0
    g2: LineSegment StartX=275 StartY=0 StartZ=0 EndX=0 EndY=0 EndZ=0
    g3: LineSegment StartX=0 StartY=0 StartZ=0 EndX=0 EndY=275 EndZ=0
  constraints (11):
    c: Coincident(g0,g1)
    c: Coincident(g1,g2)
    c: Coincident(g2,g3)
    c: Coincident(g3,g0)
    c: Horizontal(g0)
    c: Horizontal(g2)
    c: Vertical(g1)
    c: Vertical(g3)
    c: Coincident(g2,g-1)
    c: DistanceX(g2,g2) = 275
    c: DistanceY(g3,g3) = 275
FEATURE [Sketcher::SketchObject] Sketch108
  FullyConstrained = true
  Placement = pos=(0,0,175.1) rot=(0,0,1;0rad)
  sketch-geometry (5):
    g0: GeomPoint X=137.5 Y=137.5 Z=0
    g1: LineSegment StartX=137.55 StartY=137.55 StartZ=0 EndX=137.55 EndY=137.45 EndZ=0
    g2: LineSegment StartX=137.55 StartY=137.45 StartZ=0 EndX=137.45 EndY=137.45 EndZ=0
    g3: LineSegment StartX=137.45 StartY=137.45 StartZ=0 EndX=137.45 EndY=137.55 EndZ=0
    g4: LineSegment StartX=137.45 StartY=137.55 StartZ=0 EndX=137.55 EndY=137.55 EndZ=0
  constraints (14):
    c: Coincident(g1,g2)
    c: Horizontal(g2)
    c: Vertical(g1)
    c: DistanceX(g2,g2) = 0.1
    c: DistanceX(g2,g0) = 0.05
    c: DistanceY(g1,g1) = 0.1
    c: DistanceY(g1,g0) = -0.05
    c: DistanceX(g0) = 137.5
    c: DistanceY(g0) = 137.5
    c: Coincident(g3,g2)
    c: Vertical(g3)
    c: Coincident(g4,g3)
    c: Coincident(g4,g1)
    c: Horizontal(g4)
FEATURE [Part::Loft] Loft028  label="outerLayer026"
  Closed = false
  MaxDegree = 5
  Placement = pos=(0,0,-8) rot=(0,0,1;0rad)
  Ruled = false
  Sections = -> [Sketch107,Sketch108]
  Solid = true
FEATURE [Part::Cut] Cut012  label="Shell049"
  Base = -> Loft027
  Tool = -> Loft028
FEATURE [Sketcher::SketchObject] Sketch109
  FullyConstrained = true
  Placement = pos=(0,0,0) rot=(1,0,0;1.5708rad)
  sketch-geometry (28):
    g0: LineSegment StartX=50 StartY=70 StartZ=0 EndX=97.5 EndY=97.4241 EndZ=0
    g1: LineSegment StartX=97.5 StartY=97.4241 StartZ=0 EndX=97.5 EndY=101.424 EndZ=0
    g2: LineSegment StartX=97.5 StartY=101.424 StartZ=0 EndX=50 EndY=74 EndZ=0
    g3: LineSegment StartX=50 StartY=74 StartZ=0 EndX=50 EndY=70 EndZ=0
    g4: LineSegment StartX=50 StartY=82 StartZ=0 EndX=97.5 EndY=109.424 EndZ=0
    g5: LineSegment StartX=97.5 StartY=109.424 StartZ=0 EndX=97.5 EndY=105.424 EndZ=0
    g6: LineSegment StartX=97.5 StartY=105.424 StartZ=0 EndX=50 EndY=78 EndZ=0
    g7: LineSegment StartX=50 StartY=82 StartZ=0 EndX=50 EndY=78 EndZ=0
    g8: LineSegment StartX=75 StartY=116.424 StartZ=0 EndX=137.5 EndY=152.509 EndZ=0
    g9: LineSegment StartX=137.5 StartY=148.509 StartZ=0 EndX=75 EndY=112.424 EndZ=0
    g10: LineSegment StartX=75 StartY=112.424 StartZ=0 EndX=75 EndY=116.424 EndZ=0
    g11: LineSegment StartX=137.5 StartY=152.509 StartZ=0 EndX=200 EndY=116.424 EndZ=0
    g12: LineSegment StartX=200 StartY=116.424 StartZ=0 EndX=200 EndY=112.424 EndZ=0
    g13: LineSegment StartX=200 StartY=112.424 StartZ=0 EndX=137.5 EndY=148.509 EndZ=0
    g14: LineSegment StartX=177.5 StartY=109.424 StartZ=0 EndX=225 EndY=82 EndZ=0
    g15: LineSegment StartX=225 StartY=82 StartZ=0 EndX=225 EndY=78 EndZ=0
    g16: LineSegment StartX=225 StartY=78 StartZ=0 EndX=177.5 EndY=105.424 EndZ=0
    g17: LineSegment StartX=177.5 StartY=105.424 StartZ=0 EndX=177.5 EndY=109.424 EndZ=0
    g18: LineSegment StartX=177.5 StartY=101.424 StartZ=0 EndX=225 EndY=74 EndZ=0
    g19: LineSegment StartX=225 StartY=74 StartZ=0 EndX=225 EndY=70 EndZ=0
    g20: LineSegment StartX=225 StartY=70 StartZ=0 EndX=177.5 EndY=97.4241 EndZ=0
    g21: LineSegment StartX=177.5 StartY=101.424 StartZ=0 EndX=177.5 EndY=97.4241 EndZ=0
    g22: LineSegment StartX=75 StartY=120.424 StartZ=0 EndX=137.5 EndY=156.509 EndZ=0
    g23: LineSegment StartX=137.5 StartY=156.509 StartZ=0 EndX=200 EndY=120.424 EndZ=0
    g24: LineSegment StartX=200 StartY=120.424 StartZ=0 EndX=200 EndY=124.424 EndZ=0
    g25: LineSegment StartX=200 StartY=124.424 StartZ=0 EndX=137.5 EndY=160.509 EndZ=0
    g26: LineSegment StartX=137.5 StartY=160.509 StartZ=0 EndX=75 EndY=124.424 EndZ=0
    g27: LineSegment StartX=75 StartY=124.424 StartZ=0 EndX=75 EndY=120.424 EndZ=0
  constraints (84):
    c: Angle(g0) = 0.523599
    c: DistanceX(g0) = 50
    c: Coincident(g1,g0)
    c: Vertical(g1)
    c: Coincident(g2,g1)
    c: Coincident(g3,g2)
    c: Vertical(g3)
    c: DistanceY(g0,g2) = 4
    c: Parallel(g0,g2)
    c: Coincident(g0,g3)
    c: Coincident(g5,g4)
    c: Coincident(g7,g4)
    c: Coincident(g7,g6)
    c: Vertical(g7)
    c: Vertical(g5)
    c: Coincident(g5,g6)
    c: Parallel(g2,g6)
    c: Parallel(g6,g4)
    c: DistanceX(g6,g2) = 0
    c: DistanceY(g2,g6) = 4
    c: DistanceY(g6,g4) = 4
    c: DistanceX(g5,g1) = 0
    c: DistanceY(g0) = 70
    c: Coincident(g10,g9)
    c: Coincident(g10,g8)
    c: Vertical(g10)
    c: DistanceY(g9,g8) = 4
    c: Parallel(g8,g9)
    c: DistanceX(g9,g9) = 62.5
    c: Coincident(g11,g8)
    c: Coincident(g12,g11)
    c: Coincident(g13,g12)
    c: Coincident(g13,g9)
    c: Parallel(g13,g11)
    c: Vertical(g12)
    c: Coincident(g15,g14)
    c: Vertical(g15)
    c: Coincident(g17,g16)
    c: Coincident(g17,g14)
    c: Coincident(g19,g18)
    c: Vertical(g19)
    c: Coincident(g20,g19)
    c: Coincident(g21,g18)
    c: Coincident(g21,g20)
    c: Vertical(g21)
    c: Vertical(g17)
    c: DistanceX(g18,g16) = 0
    c: DistanceY(g16,g14) = 4
    c: DistanceY(g18,g16) = 4
    c: DistanceY(g20,g18) = 4
    c: Parallel(g20,g18)
    c: Parallel(g18,g16)
    c: Parallel(g16,g14)
    c: Coincident(g15,g16)
    c: DistanceY(g19,g0) = 0
    c: DistanceX(g18,g15) = 0
    c: DistanceY(g4,g9) = 3
    c: DistanceY(g4,g14) = 0
    c: DistanceY(g9,g12) = 0
    c: DistanceX(g9,g8) = 0
    c: Angle(g9) = -2.61799
    c: DistanceX(g9,g4) = 22.5
    c: DistanceX(g14,g12) = 22.5
    c: DistanceX(g9,g14) = 87.5
    c: DistanceX(g8) = 137.5
    c: DistanceX(g9,g12) = 125
    c: Coincident(g23,g22)
    c: Coincident(g24,g23)
    c: Vertical(g24)
    c: Coincident(g26,g25)
    c: Coincident(g27,g22)
    c: Vertical(g27)
    c: DistanceX(g22,g8) = 0
    c: DistanceX(g8,g22) = 0
    c: DistanceX(g25,g22) = 0
    c: Coincident(g24,g25)
    c: Coincident(g26,g27)
    c: DistanceY(g8,g22) = 4
    c: DistanceY(g22,g25) = 4
    c: DistanceY(g11,g23) = 4
    c: DistanceY(g23,g24) = 4
    c: DistanceX(g23,g11) = 0
    c: DistanceY(g8,g22) = 4
    c: DistanceY(g22,g26) = 4
FEATURE [Part::Extrusion] Extrude040  label="cuts024"
  Base = -> Sketch109
  Dir = (0,-1,2e-16)
  DirMode = 2
  FaceMakerClass = Part::FaceMakerBullseye
  LengthFwd = 275
  LengthRev = 0
  Reversed = true
  Solid = true
  Symmetric = false
FEATURE [Sketcher::SketchObject] Sketch110
  FullyConstrained = true
  Placement = pos=(0,0,0) rot=(1,0,0;1.5708rad)
  sketch-geometry (28):
    g0: LineSegment StartX=50 StartY=70 StartZ=0 EndX=97.5 EndY=97.4241 EndZ=0
    g1: LineSegment StartX=97.5 StartY=97.4241 StartZ=0 EndX=97.5 EndY=101.424 EndZ=0
    g2: LineSegment StartX=97.5 StartY=101.424 StartZ=0 EndX=50 EndY=74 EndZ=0
    g3: LineSegment StartX=50 StartY=74 StartZ=0 EndX=50 EndY=70 EndZ=0
    g4: LineSegment StartX=50 StartY=82 StartZ=0 EndX=97.5 EndY=109.424 EndZ=0
    g5: LineSegment StartX=97.5 StartY=109.424 StartZ=0 EndX=97.5 EndY=105.424 EndZ=0
    g6: LineSegment StartX=97.5 StartY=105.424 StartZ=0 EndX=50 EndY=78 EndZ=0
    g7: LineSegment StartX=50 StartY=82 StartZ=0 EndX=50 EndY=78 EndZ=0
    g8: LineSegment StartX=75 StartY=116.424 StartZ=0 EndX=137.5 EndY=152.509 EndZ=0
    g9: LineSegment StartX=137.5 StartY=148.509 StartZ=0 EndX=75 EndY=112.424 EndZ=0
    g10: LineSegment StartX=75 StartY=112.424 StartZ=0 EndX=75 EndY=116.424 EndZ=0
    g11: LineSegment StartX=137.5 StartY=152.509 StartZ=0 EndX=200 EndY=116.424 EndZ=0
    g12: LineSegment StartX=200 StartY=116.424 StartZ=0 EndX=200 EndY=112.424 EndZ=0
    g13: LineSegment StartX=200 StartY=112.424 StartZ=0 EndX=137.5 EndY=148.509 EndZ=0
    g14: LineSegment StartX=177.5 StartY=109.424 StartZ=0 EndX=225 EndY=82 EndZ=0
    g15: LineSegment StartX=225 StartY=82 StartZ=0 EndX=225 EndY=78 EndZ=0
    g16: LineSegment StartX=225 StartY=78 StartZ=0 EndX=177.5 EndY=105.424 EndZ=0
    g17: LineSegment StartX=177.5 StartY=105.424 StartZ=0 EndX=177.5 EndY=109.424 EndZ=0
    g18: LineSegment StartX=177.5 StartY=101.424 StartZ=0 EndX=225 EndY=74 EndZ=0
    g19: LineSegment StartX=225 StartY=74 StartZ=0 EndX=225 EndY=70 EndZ=0
    g20: LineSegment StartX=225 StartY=70 StartZ=0 EndX=177.5 EndY=97.4241 EndZ=0
    g21: LineSegment StartX=177.5 StartY=101.424 StartZ=0 EndX=177.5 EndY=97.4241 EndZ=0
    g22: LineSegment StartX=75 StartY=120.424 StartZ=0 EndX=75 EndY=124.424 EndZ=0
    g23: LineSegment StartX=75 StartY=124.424 StartZ=0 EndX=137.5 EndY=160.509 EndZ=0
    g24: LineSegment StartX=137.5 StartY=160.509 StartZ=0 EndX=200 EndY=124.424 EndZ=0
    g25: LineSegment StartX=200 StartY=124.424 StartZ=0 EndX=200 EndY=120.424 EndZ=0
    g26: LineSegment StartX=200 StartY=120.424 StartZ=0 EndX=137.5 EndY=156.509 EndZ=0
    g27: LineSegment StartX=137.5 StartY=156.509 StartZ=0 EndX=75 EndY=120.424 EndZ=0
  constraints (84):
    c: Angle(g0) = 0.523599
    c: DistanceX(g0) = 50
    c: Coincident(g1,g0)
    c: Vertical(g1)
    c: Coincident(g2,g1)
    c: Coincident(g3,g2)
    c: Vertical(g3)
    c: DistanceY(g0,g2) = 4
    c: Parallel(g0,g2)
    c: Coincident(g0,g3)
    c: Coincident(g5,g4)
    c: Coincident(g7,g4)
    c: Coincident(g7,g6)
    c: Vertical(g7)
    c: Vertical(g5)
    c: Coincident(g5,g6)
    c: Parallel(g2,g6)
    c: Parallel(g6,g4)
    c: DistanceX(g6,g2) = 0
    c: DistanceY(g2,g6) = 4
    c: DistanceY(g6,g4) = 4
    c: DistanceX(g5,g1) = 0
    c: DistanceY(g0) = 70
    c: Coincident(g10,g9)
    c: Coincident(g10,g8)
    c: Vertical(g10)
    c: DistanceY(g9,g8) = 4
    c: Parallel(g8,g9)
    c: DistanceX(g9,g9) = 62.5
    c: Coincident(g11,g8)
    c: Coincident(g12,g11)
    c: Coincident(g13,g12)
    c: Coincident(g13,g9)
    c: Parallel(g13,g11)
    c: Vertical(g12)
    c: Coincident(g15,g14)
    c: Vertical(g15)
    c: Coincident(g17,g16)
    c: Coincident(g17,g14)
    c: Coincident(g19,g18)
    c: Vertical(g19)
    c: Coincident(g20,g19)
    c: Coincident(g21,g18)
    c: Coincident(g21,g20)
    c: Vertical(g21)
    c: Vertical(g17)
    c: DistanceX(g18,g16) = 0
    c: DistanceY(g16,g14) = 4
    c: DistanceY(g18,g16) = 4
    c: DistanceY(g20,g18) = 4
    c: Parallel(g20,g18)
    c: Parallel(g18,g16)
    c: Parallel(g16,g14)
    c: Coincident(g15,g16)
    c: DistanceY(g19,g0) = 0
    c: DistanceX(g18,g15) = 0
    c: DistanceX(g14,g14) = 47.5
    c: DistanceX(g4,g4) = 47.5
    c: DistanceX(g4,g14) = 80
    c: Parallel(g9,g4)
    c: DistanceX(g9,g8) = 0
    c: DistanceY(g4,g9) = 3
    c: DistanceY(g14,g12) = 3
    c: DistanceY(g14,g4) = 0
    c: DistanceX(g8) = 137.5
    c: DistanceX(g9,g12) = 125
    c: Vertical(g22)
    c: Coincident(g23,g22)
    c: Coincident(g24,g23)
    c: Coincident(g25,g24)
    c: Vertical(g25)
    c: Coincident(g26,g25)
    c: Coincident(g27,g22)
    c: DistanceX(g22,g8) = 0
    c: DistanceY(g8,g22) = 4
    c: DistanceY(g22,g22) = 4
    c: Coincident(g26,g27)
    c: DistanceX(g26,g8) = 0
    c: DistanceY(g26,g23) = 4
    c: DistanceY(g8,g26) = 4
    c: DistanceX(g23,g26) = 0
    c: DistanceX(g25,g11) = 0
    c: DistanceY(g11,g25) = 4
    c: DistanceY(g25,g24) = 4
FEATURE [Part::Extrusion] Extrude041  label="cuts025"
  Base = -> Sketch110
  Dir = (0,-1,2e-16)
  DirMode = 2
  FaceMakerClass = Part::FaceMakerBullseye
  LengthFwd = 275
  LengthRev = 0
  Placement = pos=(275,0,0) rot=(0,0,1;1.5708rad)
  Reversed = true
  Solid = true
  Symmetric = false
FEATURE [Sketcher::SketchObject] Sketch111
  FullyConstrained = true
  Placement = pos=(0,0,0) rot=(1,0,0;1.5708rad)
  sketch-geometry (3):
    g0: LineSegment StartX=15 StartY=0 StartZ=0 EndX=260 EndY=0 EndZ=0
    g1: LineSegment StartX=260 StartY=0 StartZ=0 EndX=137.5 EndY=160 EndZ=0
    g2: LineSegment StartX=137.5 StartY=160 StartZ=0 EndX=15 EndY=0 EndZ=0
  constraints (9):
    c: Horizontal(g0)
    c: Coincident(g1,g0)
    c: Coincident(g2,g1)
    c: DistanceX(g0) = 260
    c: DistanceX(g1) = 137.5
    c: DistanceY(g1) = 160
    c: Coincident(g0,g2)
    c: DistanceY(g0,g-1) = 0
    c: DistanceX(g-1,g0) = 15
FEATURE [Part::Extrusion] Extrude042
  Base = -> Sketch111
  Dir = (0,-1,-6e-16)
  DirMode = 2
  FaceMakerClass = Part::FaceMakerBullseye
  LengthFwd = 275
  LengthRev = 0
  Placement = pos=(0,0,0) rot=(0,0,1;1.5708rad)
  Solid = true
  Symmetric = false
FEATURE [Part::MultiCommon] Common025  label="cuts020"
  Shapes = -> [Extrude042,Extrude040]
FEATURE [Sketcher::SketchObject] Sketch112
  FullyConstrained = true
  Placement = pos=(0,0,0) rot=(1,0,0;1.5708rad)
  sketch-geometry (3):
    g0: LineSegment StartX=15 StartY=0 StartZ=0 EndX=260 EndY=0 EndZ=0
    g1: LineSegment StartX=260 StartY=0 StartZ=0 EndX=137.5 EndY=160 EndZ=0
    g2: LineSegment StartX=137.5 StartY=160 StartZ=0 EndX=15 EndY=0 EndZ=0
  constraints (9):
    c: Horizontal(g0)
    c: Coincident(g1,g0)
    c: Coincident(g2,g1)
    c: DistanceX(g0) = 260
    c: DistanceX(g1) = 137.5
    c: DistanceY(g1) = 160
    c: Coincident(g0,g2)
    c: DistanceY(g0,g-1) = 0
    c: DistanceX(g-1,g0) = 15
FEATURE [Part::Extrusion] Extrude043
  Base = -> Sketch112
  Dir = (0,-1,2e-16)
  DirMode = 2
  FaceMakerClass = Part::FaceMakerBullseye
  LengthFwd = 275
  LengthRev = 0
  Reversed = true
  Solid = true
  Symmetric = false
FEATURE [Part::MultiCommon] Common026  label="cuts021"
  Shapes = -> [Extrude043,Extrude041]
FEATURE [Part::MultiFuse] Fusion072  label="keep003"
  Placement = pos=(0,0,4) rot=(0,0,1;0rad)
  Shapes = -> [Common026,Common025]
FEATURE [Part::MultiCommon] Common027  label="keeps003"
  Shapes = -> [Loft026,Fusion072]
FEATURE [Part::MultiFuse] Fusion073  label="shell003"
  Shapes = -> [Cut012,Common027]
FEATURE [Part::MultiFuse] Fusion074  label="shellLegacy001"
  Shapes = -> [Common022,Fusion073]
FEATURE [Part::Cut] Cut013  label="shellNow001"
  Base = -> Fusion074
  Tool = -> Fusion071
FEATURE [Sketcher::SketchObject] Sketch113
  FullyConstrained = true
  sketch-geometry (4):
    g0: LineSegment StartX=0 StartY=275 StartZ=0 EndX=275 EndY=275 EndZ=0
    g1: LineSegment StartX=275 StartY=275 StartZ=0 EndX=275 EndY=0 EndZ=0
    g2: LineSegment StartX=275 StartY=0 StartZ=0 EndX=0 EndY=0 EndZ=0
    g3: LineSegment StartX=0 StartY=0 StartZ=0 EndX=0 EndY=275 EndZ=0
  constraints (11):
    c: Coincident(g0,g1)
    c: Coincident(g1,g2)
    c: Coincident(g2,g3)
    c: Coincident(g3,g0)
    c: Horizontal(g0)
    c: Horizontal(g2)
    c: Vertical(g1)
    c: Vertical(g3)
    c: Coincident(g2,g-1)
    c: DistanceX(g2,g2) = 275
    c: DistanceY(g3,g3) = 275
FEATURE [Sketcher::SketchObject] Sketch114
  FullyConstrained = true
  Placement = pos=(0,0,175.1) rot=(0,0,1;0rad)
  sketch-geometry (5):
    g0: GeomPoint X=137.5 Y=137.5 Z=0
    g1: LineSegment StartX=137.55 StartY=137.55 StartZ=0 EndX=137.55 EndY=137.45 EndZ=0
    g2: LineSegment StartX=137.55 StartY=137.45 StartZ=0 EndX=137.45 EndY=137.45 EndZ=0
    g3: LineSegment StartX=137.45 StartY=137.45 StartZ=0 EndX=137.45 EndY=137.55 EndZ=0
    g4: LineSegment StartX=137.45 StartY=137.55 StartZ=0 EndX=137.55 EndY=137.55 EndZ=0
  constraints (14):
    c: Coincident(g1,g2)
    c: Horizontal(g2)
    c: Vertical(g1)
    c: DistanceX(g2,g2) = 0.1
    c: DistanceX(g2,g0) = 0.05
    c: DistanceY(g1,g1) = 0.1
    c: DistanceY(g1,g0) = -0.05
    c: DistanceX(g0) = 137.5
    c: DistanceY(g0) = 137.5
    c: Coincident(g3,g2)
    c: Vertical(g3)
    c: Coincident(g4,g3)
    c: Coincident(g4,g1)
    c: Horizontal(g4)
FEATURE [Part::Loft] Loft029  label="outerLayer027"
  Closed = false
  MaxDegree = 5
  Ruled = false
  Sections = -> [Sketch113,Sketch114]
  Solid = true
FEATURE [Part::Cut] Cut014  label="topLidKeep"
  Base = -> Loft029
  Tool = -> Box
FEATURE [Sketcher::SketchObject] Sketch115
  FullyConstrained = true
  sketch-geometry (4):
    g0: LineSegment StartX=0 StartY=275 StartZ=0 EndX=275 EndY=275 EndZ=0
    g1: LineSegment StartX=275 StartY=275 StartZ=0 EndX=275 EndY=0 EndZ=0
    g2: LineSegment StartX=275 StartY=0 StartZ=0 EndX=0 EndY=0 EndZ=0
    g3: LineSegment StartX=0 StartY=0 StartZ=0 EndX=0 EndY=275 EndZ=0
  constraints (11):
    c: Coincident(g0,g1)
    c: Coincident(g1,g2)
    c: Coincident(g2,g3)
    c: Coincident(g3,g0)
    c: Horizontal(g0)
    c: Horizontal(g2)
    c: Vertical(g1)
    c: Vertical(g3)
    c: Coincident(g2,g-1)
    c: DistanceX(g2,g2) = 275
    c: DistanceY(g3,g3) = 275
FEATURE [Sketcher::SketchObject] Sketch116
  FullyConstrained = true
  Placement = pos=(0,0,175.1) rot=(0,0,1;0rad)
  sketch-geometry (5):
    g0: GeomPoint X=137.5 Y=137.5 Z=0
    g1: LineSegment StartX=137.55 StartY=137.55 StartZ=0 EndX=137.55 EndY=137.45 EndZ=0
    g2: LineSegment StartX=137.55 StartY=137.45 StartZ=0 EndX=137.45 EndY=137.45 EndZ=0
    g3: LineSegment StartX=137.45 StartY=137.45 StartZ=0 EndX=137.45 EndY=137.55 EndZ=0
    g4: LineSegment StartX=137.45 StartY=137.55 StartZ=0 EndX=137.55 EndY=137.55 EndZ=0
  constraints (14):
    c: Coincident(g1,g2)
    c: Horizontal(g2)
    c: Vertical(g1)
    c: DistanceX(g2,g2) = 0.1
    c: DistanceX(g2,g0) = 0.05
    c: DistanceY(g1,g1) = 0.1
    c: DistanceY(g1,g0) = -0.05
    c: DistanceX(g0) = 137.5
    c: DistanceY(g0) = 137.5
    c: Coincident(g3,g2)
    c: Vertical(g3)
    c: Coincident(g4,g3)
    c: Coincident(g4,g1)
    c: Horizontal(g4)
FEATURE [Part::Loft] Loft014  label="outerLayer028"
  Closed = false
  MaxDegree = 5
  Placement = pos=(0,0,-4) rot=(0,0,1;0rad)
  Ruled = false
  Sections = -> [Sketch115,Sketch116]
  Solid = true
FEATURE [Part::MultiCommon] Common028
  Shapes = -> [Loft014,Box001]
FEATURE [Part::Cut] Cut015  label="topShellKeep"
  Base = -> Cut014
  Tool = -> Common028
FEATURE [Part::MultiCommon] Common029  label="topShellKeep001"
  Shapes = -> [Cut013,Cut015]
FEATURE [Sketcher::SketchObject] Sketch117
  FullyConstrained = true
  Placement = pos=(0,0,88.5) rot=(0,0,1;0rad)
  sketch-geometry (8):
    g0: Circle CenterX=85 CenterY=137.5 CenterZ=0 NormalX=0 NormalY=0 NormalZ=1 AngleXU=0 Radius=7.5
    g1: Circle CenterX=137.5 CenterY=85 CenterZ=0 NormalX=0 NormalY=0 NormalZ=1 AngleXU=0 Radius=7.5
    g2: Circle CenterX=190 CenterY=137.5 CenterZ=0 NormalX=0 NormalY=0 NormalZ=1 AngleXU=0 Radius=7.5
    g3: Circle CenterX=137.5 CenterY=190 CenterZ=0 NormalX=0 NormalY=0 NormalZ=1 AngleXU=0 Radius=7.5
    g4: Circle CenterX=85 CenterY=137.5 CenterZ=0 NormalX=0 NormalY=0 NormalZ=1 AngleXU=0 Radius=2
    g5: Circle CenterX=190 CenterY=137.5 CenterZ=0 NormalX=0 NormalY=0 NormalZ=1 AngleXU=0 Radius=2
    g6: Circle CenterX=137.5 CenterY=85 CenterZ=0 NormalX=0 NormalY=0 NormalZ=1 AngleXU=0 Radius=2
    g7: Circle CenterX=137.5 CenterY=190 CenterZ=0 NormalX=0 NormalY=0 NormalZ=1 AngleXU=0 Radius=2
  constraints (20):
    c: DistanceX(g-1,g1) = 137.5
    c: DistanceY(g-1,g1) = 85
    c: DistanceX(g0,g1) = 52.5
    c: DistanceX(g1,g2) = 52.5
    c: DistanceY(g0,g3) = 52.5
    c: DistanceX(g3,g1) = 0
    c: DistanceY(g2,g0) = 0
    c: DistanceY(g1,g0) = 52.5
    c: Equal(g3,g2)
    c: Equal(g3,g1)
    c: Equal(g3,g0)
    c: Diameter(g3) = 15
    c: Coincident(g4,g0)
    c: Coincident(g5,g2)
    c: Coincident(g6,g1)
    c: Coincident(g7,g3)
    c: Equal(g5,g6)
    c: Equal(g5,g4)
    c: Equal(g5,g7)
    c: Diameter(g5) = 4
FEATURE [Part::Extrusion] Extrude044
  Base = -> Sketch117
  Dir = (0,0,1)
  DirMode = 2
  FaceMakerClass = Part::FaceMakerBullseye
  LengthFwd = 25
  LengthRev = 0
  Solid = true
  Symmetric = false
FEATURE [Part::MultiCommon] Common030  label="magnetMountHolds"
  Shapes = -> [Loft023,Extrude044]
FEATURE [Part::MultiFuse] Fusion075  label="topLid"
  Shapes = -> [Common030,Common029]
FEATURE [Part::Box] Box005  label="Cube009"
  AttacherType = Attacher::AttachEngine3D
  Height = 13
  Length = 67
  Placement = pos=(-20.5,-34,56) rot=(0,0,1;0rad)
  Width = 18
FEATURE [Part::Box] Box006  label="Cube010"
  AttacherType = Attacher::AttachEngine3D
  Height = 50
  Length = 18
  Placement = pos=(128.5,175.75,113.5) rot=(0,0,1;0rad)
  Width = 10
FEATURE [Part::Cylinder] Cylinder  label="Cylinder026"
  Angle = 360
  AttacherType = Attacher::AttachEngine3D
  FirstAngle = 0
  Height = 13
  Placement = pos=(-20.5,-25,56) rot=(0,0,1;0rad)
  Radius = 9
  SecondAngle = 0
FEATURE [Part::Cylinder] Cylinder026  label="antennaIn002"
  Angle = 360
  AttacherType = Attacher::AttachEngine3D
  FirstAngle = 0
  Height = 10
  Placement = pos=(-23,0,65) rot=(0,0,1;0rad)
  Radius = 3.25
  SecondAngle = 0
FEATURE [Part::Cylinder] Cylinder027  label="antennaIn003"
  Angle = 360
  AttacherType = Attacher::AttachEngine3D
  FirstAngle = 0
  Height = 10
  Placement = pos=(-23,0,69) rot=(0,0,1;0rad)
  Radius = 5.75
  SecondAngle = 0
FEATURE [Part::Cylinder] Cylinder028  label="antennaIn004"
  Angle = 360
  AttacherType = Attacher::AttachEngine3D
  FirstAngle = 0
  Height = 10
  Placement = pos=(-23,0,65) rot=(0,0,1;0rad)
  Radius = 3.25
  SecondAngle = 0
FEATURE [Part::Cylinder] Cylinder029  label="antennaIn005"
  Angle = 360
  AttacherType = Attacher::AttachEngine3D
  FirstAngle = 0
  Height = 10
  Placement = pos=(-23,0,69) rot=(0,0,1;0rad)
  Radius = 5.75
  SecondAngle = 0
FEATURE [Part::MultiFuse] Fusion004
  Placement = pos=(2.5,-25,-6) rot=(0,0,1;0rad)
  Shapes = -> [Cylinder026,Cylinder027]
FEATURE [Part::MultiFuse] Fusion005
  Placement = pos=(2.5,-25,-19.5) rot=(0,0,1;0rad)
  Shapes = -> [Cylinder028,Cylinder029]
FEATURE [Part::MultiFuse] Fusion006  label="antennaCuts"
  Shapes = -> [Fusion004,Fusion005]
FEATURE [Part::MultiFuse] Fusion076
  Placement = pos=(0,0,-1) rot=(0,0,1;0rad)
  Shapes = -> [Cylinder,Box005]
FEATURE [Part::Cut] Cut016  label="antennaHolder"
  Base = -> Fusion076
  Placement = pos=(162.5,175,95.5) rot=(0,0,-1;1.5708rad)
  Tool = -> Fusion006
FEATURE [Part::MultiFuse] Fusion077  label="antennaHolder001"
  Shapes = -> [Box006,Cut016]
FEATURE [Part::Feature] Part__Feature104  label="5862K227_Neodymium_Bottom_Leg005"
  Placement = pos=(30,30,-4) rot=(-1,0,0;1.5708rad)
  shape: bbox 13.75 x 13.75 x 6.35 mm, 14 faces (baked)
FEATURE [Part::Feature] Part__Feature105  label="91698A721_M3_MagnetScrew14mm_leg_1_Down001"
  Placement = pos=(30,30,-2) rot=(0,0,1;0rad)
  shape: bbox 5.601 x 5.601 x 14.23 mm, 86 faces (baked)
FEATURE [Part::Feature] Part__Feature106  label="91698A721_M3_MagnetScrew14mm_Leg1_Up001"
  Placement = pos=(30,30,2) rot=(0,1,0;3.14159rad)
  shape: bbox 5.601 x 5.601 x 14.23 mm, 86 faces (baked)
FEATURE [Part::Feature] Part__Feature107  label="94459A130_M3_HeatSetInserts_Down_Leg005"
  Placement = pos=(30,30,-10) rot=(1,0,0;1.5708rad)
  shape: bbox 4.74 x 4.749 x 4.466 mm, 209 faces (baked)
FEATURE [Part::Feature] Part__Feature108  label="5862K227_Magnet_Leg_1_Up001"
  Placement = pos=(30,30,4) rot=(-1,0,0;1.5708rad)
  shape: bbox 13.75 x 13.75 x 6.35 mm, 14 faces (baked)
FEATURE [Part::MultiFuse] Fusion023  label="coupledMagnetsV1-M3Large"
  Placement = pos=(90,7,20) rot=(0,0,1;0rad)
  Shapes = -> [Part__Feature104,Part__Feature105,Part__Feature106,Part__Feature107,Part__Feature108]
FEATURE [Part::Feature] Part__Feature217  label="5862K227_Neodymium_Bottom_Leg006"
  Placement = pos=(30,30,-4) rot=(-1,0,0;1.5708rad)
  shape: bbox 13.75 x 13.75 x 6.35 mm, 14 faces (baked)
FEATURE [Part::Feature] Part__Feature218  label="91698A721_M3_MagnetScrew14mm_leg_1_Down002"
  Placement = pos=(30,30,-2) rot=(0,0,1;0rad)
  shape: bbox 5.601 x 5.601 x 14.23 mm, 86 faces (baked)
FEATURE [Part::Feature] Part__Feature219  label="91698A721_M3_MagnetScrew14mm_Leg1_Up002"
  Placement = pos=(30,30,2) rot=(0,1,0;3.14159rad)
  shape: bbox 5.601 x 5.601 x 14.23 mm, 86 faces (baked)
FEATURE [Part::Feature] Part__Feature220  label="94459A130_M3_HeatSetInserts_Down_Leg006"
  Placement = pos=(30,30,-10) rot=(1,0,0;1.5708rad)
  shape: bbox 4.74 x 4.749 x 4.466 mm, 209 faces (baked)
FEATURE [Part::Feature] Part__Feature221  label="5862K227_Magnet_Leg_1_Up002"
  Placement = pos=(30,30,4) rot=(-1,0,0;1.5708rad)
  shape: bbox 13.75 x 13.75 x 6.35 mm, 14 faces (baked)
FEATURE [Part::MultiFuse] Fusion078  label="coupledMagnetsV1-M3Large001"
  Placement = pos=(7,100,20) rot=(0,0,1;0rad)
  Shapes = -> [Part__Feature217,Part__Feature218,Part__Feature219,Part__Feature220,Part__Feature221]
FEATURE [Part::Feature] Part__Feature222  label="5862K227_Neodymium_Bottom_Leg008"
  Placement = pos=(30,30,-4) rot=(-1,0,0;1.5708rad)
  shape: bbox 13.75 x 13.75 x 6.35 mm, 14 faces (baked)
FEATURE [Part::Feature] Part__Feature223  label="91698A721_M3_MagnetScrew14mm_leg_1_Down004"
  Placement = pos=(30,30,-2) rot=(0,0,1;0rad)
  shape: bbox 5.601 x 5.601 x 14.23 mm, 86 faces (baked)
FEATURE [Part::Feature] Part__Feature224  label="91698A721_M3_MagnetScrew14mm_Leg1_Up004"
  Placement = pos=(30,30,2) rot=(0,1,0;3.14159rad)
  shape: bbox 5.601 x 5.601 x 14.23 mm, 86 faces (baked)
FEATURE [Part::Feature] Part__Feature225  label="94459A130_M3_HeatSetInserts_Down_Leg008"
  Placement = pos=(30,30,-10) rot=(1,0,0;1.5708rad)
  shape: bbox 4.74 x 4.749 x 4.466 mm, 209 faces (baked)
FEATURE [Part::Feature] Part__Feature226  label="5862K227_Magnet_Leg_1_Up004"
  Placement = pos=(30,30,4) rot=(-1,0,0;1.5708rad)
  shape: bbox 13.75 x 13.75 x 6.35 mm, 14 faces (baked)
FEATURE [Part::MultiFuse] Fusion079  label="coupledMagnetsV1-M3Large003"
  Placement = pos=(208,140,20) rot=(0,0,1;0rad)
  Shapes = -> [Part__Feature222,Part__Feature223,Part__Feature224,Part__Feature225,Part__Feature226]
FEATURE [Part::Feature] Part__Feature227  label="5862K227_Neodymium_Bottom_Leg009"
  Placement = pos=(30,30,-4) rot=(-1,0,0;1.5708rad)
  shape: bbox 13.75 x 13.75 x 6.35 mm, 14 faces (baked)
FEATURE [Part::Feature] Part__Feature228  label="91698A721_M3_MagnetScrew14mm_leg_1_Down005"
  Placement = pos=(30,30,-2) rot=(0,0,1;0rad)
  shape: bbox 5.601 x 5.601 x 14.23 mm, 86 faces (baked)
FEATURE [Part::Feature] Part__Feature229  label="91698A721_M3_MagnetScrew14mm_Leg1_Up005"
  Placement = pos=(30,30,2) rot=(0,1,0;3.14159rad)
  shape: bbox 5.601 x 5.601 x 14.23 mm, 86 faces (baked)
FEATURE [Part::Feature] Part__Feature230  label="94459A130_M3_HeatSetInserts_Down_Leg009"
  Placement = pos=(30,30,-10) rot=(1,0,0;1.5708rad)
  shape: bbox 4.74 x 4.749 x 4.466 mm, 209 faces (baked)
FEATURE [Part::Feature] Part__Feature231  label="5862K227_Magnet_Leg_1_Up005"
  Placement = pos=(30,30,4) rot=(-1,0,0;1.5708rad)
  shape: bbox 13.75 x 13.75 x 6.35 mm, 14 faces (baked)
FEATURE [Part::MultiFuse] Fusion080  label="coupledMagnetsV1-M3Large004"
  Placement = pos=(25.5,210,20) rot=(0,0,1;0rad)
  Shapes = -> [Part__Feature227,Part__Feature228,Part__Feature229,Part__Feature230,Part__Feature231]
FEATURE [Sketcher::SketchObject] Sketch118
  FullyConstrained = true
  Placement = pos=(67.5,0,0) rot=(0.57735,0.57735,0.57735;2.0944rad)
  sketch-geometry (8):
    g0: LineSegment StartX=177.03 StartY=4.99735 StartZ=0 EndX=195.06 EndY=-18.08 EndZ=0
    g1: LineSegment StartX=239.27 StartY=22.8 StartZ=0 EndX=257.08 EndY=7.1e-15 EndZ=0
    g2: LineSegment StartX=177.03 StartY=4.99735 StartZ=0 EndX=183.375 EndY=4.99735 EndZ=0
    g3: LineSegment StartX=183.375 StartY=4.99735 StartZ=0 EndX=199 EndY=-15.0017 EndZ=0
    g4: LineSegment StartX=195.06 StartY=-18.08 StartZ=0 EndX=199 EndY=-15.0017 EndZ=0
    g5: LineSegment StartX=239.27 StartY=22.8 StartZ=0 EndX=235.33 EndY=19.722 EndZ=0
    g6: LineSegment StartX=235.33 StartY=19.722 StartZ=0 EndX=250.735 EndY=7.1e-15 EndZ=0
    g7: LineSegment StartX=250.735 StartY=7.1e-15 StartZ=0 EndX=257.08 EndY=7.1e-15 EndZ=0
  constraints (24):
    c: Angle(g0) = -0.907571
    c: DistanceX(g1,g1) = 17.81
    c: DistanceY(g0) = -18.08
    c: DistanceX(g1) = 257.08
    c: DistanceX(g0) = 177.03
    c: Coincident(g2,g0)
    c: Horizontal(g2)
    c: Coincident(g3,g2)
    c: DistanceX(g0) = 195.06
    c: Coincident(g4,g0)
    c: Coincident(g4,g3)
    c: Angle(g4,g0) = 1.5708
    c: Distance(g4) = 5
    c: Parallel(g0,g3)
    c: Coincident(g6,g5)
    c: Distance(g5) = 5
    c: Coincident(g1,g5)
    c: Parallel(g6,g1)
    c: Angle(g6,g5) = 1.5708
    c: Coincident(g7,g6)
    c: Coincident(g7,g1)
    c: Horizontal(g7)
    c: DistanceY(g1) = 22.8
    c: DistanceY(g6) = 0
FEATURE [Part::Extrusion] Extrude045
  Base = -> Sketch118
  Dir = (1,0,0)
  DirMode = 2
  FaceMakerClass = Part::FaceMakerBullseye
  LengthFwd = 140
  LengthRev = 0
  Solid = true
  Symmetric = false
FEATURE [Part::MultiFuse] Fusion082  label="level02s001"
  Shapes = -> [Fusion068,Extrude045]
FEATURE [Part::MultiFuse] Fusion083  label="topLid001"
  Shapes = -> [Fusion075,Fusion077]
FEATURE [Part::Feature] Part__Feature232  label="5862K227_Neodymium_Bottom_Leg010"
  Placement = pos=(30,30,-4) rot=(-1,0,0;1.5708rad)
  shape: bbox 13.75 x 13.75 x 6.35 mm, 14 faces (baked)
FEATURE [Part::Feature] Part__Feature233  label="91698A721_M3_MagnetScrew14mm_leg_1_Down006"
  Placement = pos=(30,30,-2) rot=(0,0,1;0rad)
  shape: bbox 5.601 x 5.601 x 14.23 mm, 86 faces (baked)
FEATURE [Part::Feature] Part__Feature234  label="91698A721_M3_MagnetScrew14mm_Leg1_Up006"
  Placement = pos=(30,30,2) rot=(0,1,0;3.14159rad)
  shape: bbox 5.601 x 5.601 x 14.23 mm, 86 faces (baked)
FEATURE [Part::Feature] Part__Feature235  label="94459A130_M3_HeatSetInserts_Down_Leg010"
  Placement = pos=(30,30,-10) rot=(1,0,0;1.5708rad)
  shape: bbox 4.74 x 4.749 x 4.466 mm, 209 faces (baked)
FEATURE [Part::Feature] Part__Feature236  label="5862K227_Magnet_Leg_1_Up006"
  Placement = pos=(30,30,4) rot=(-1,0,0;1.5708rad)
  shape: bbox 13.75 x 13.75 x 6.35 mm, 14 faces (baked)
FEATURE [Part::MultiFuse] Fusion084  label="coupledMagnetsV1-M3Large005"
  Placement = pos=(107.5,55,81.25) rot=(0,0,1;0rad)
  Shapes = -> [Part__Feature232,Part__Feature233,Part__Feature234,Part__Feature235,Part__Feature236]
FEATURE [Part::Feature] Part__Feature237  label="5862K227_Neodymium_Bottom_Leg011"
  Placement = pos=(30,30,-4) rot=(-1,0,0;1.5708rad)
  shape: bbox 13.75 x 13.75 x 6.35 mm, 14 faces (baked)
FEATURE [Part::Feature] Part__Feature238  label="91698A721_M3_MagnetScrew14mm_leg_1_Down007"
  Placement = pos=(30,30,-2) rot=(0,0,1;0rad)
  shape: bbox 5.601 x 5.601 x 14.23 mm, 86 faces (baked)
FEATURE [Part::Feature] Part__Feature239  label="91698A721_M3_MagnetScrew14mm_Leg1_Up007"
  Placement = pos=(30,30,2) rot=(0,1,0;3.14159rad)
  shape: bbox 5.601 x 5.601 x 14.23 mm, 86 faces (baked)
FEATURE [Part::Feature] Part__Feature240  label="94459A130_M3_HeatSetInserts_Down_Leg011"
  Placement = pos=(30,30,-10) rot=(1,0,0;1.5708rad)
  shape: bbox 4.74 x 4.749 x 4.466 mm, 209 faces (baked)
FEATURE [Part::Feature] Part__Feature241  label="5862K227_Magnet_Leg_1_Up007"
  Placement = pos=(30,30,4) rot=(-1,0,0;1.5708rad)
  shape: bbox 13.75 x 13.75 x 6.35 mm, 14 faces (baked)
FEATURE [Part::MultiFuse] Fusion085  label="coupledMagnetsV1-M3Large006"
  Placement = pos=(55,107.5,81.25) rot=(0,0,1;0rad)
  Shapes = -> [Part__Feature237,Part__Feature238,Part__Feature239,Part__Feature240,Part__Feature241]
FEATURE [Part::Feature] Part__Feature242  label="5862K227_Neodymium_Bottom_Leg012"
  Placement = pos=(30,30,-4) rot=(-1,0,0;1.5708rad)
  shape: bbox 13.75 x 13.75 x 6.35 mm, 14 faces (baked)
FEATURE [Part::Feature] Part__Feature243  label="91698A721_M3_MagnetScrew14mm_leg_1_Down008"
  Placement = pos=(30,30,-2) rot=(0,0,1;0rad)
  shape: bbox 5.601 x 5.601 x 14.23 mm, 86 faces (baked)
FEATURE [Part::Feature] Part__Feature244  label="91698A721_M3_MagnetScrew14mm_Leg1_Up008"
  Placement = pos=(30,30,2) rot=(0,1,0;3.14159rad)
  shape: bbox 5.601 x 5.601 x 14.23 mm, 86 faces (baked)
FEATURE [Part::Feature] Part__Feature245  label="94459A130_M3_HeatSetInserts_Down_Leg012"
  Placement = pos=(30,30,-10) rot=(1,0,0;1.5708rad)
  shape: bbox 4.74 x 4.749 x 4.466 mm, 209 faces (baked)
FEATURE [Part::Feature] Part__Feature246  label="5862K227_Magnet_Leg_1_Up008"
  Placement = pos=(30,30,4) rot=(-1,0,0;1.5708rad)
  shape: bbox 13.75 x 13.75 x 6.35 mm, 14 faces (baked)
FEATURE [Part::MultiFuse] Fusion086  label="coupledMagnetsV1-M3Large007"
  Placement = pos=(160,107.5,81.25) rot=(0,0,1;0rad)
  Shapes = -> [Part__Feature242,Part__Feature243,Part__Feature244,Part__Feature245,Part__Feature246]
FEATURE [Part::Feature] Part__Feature247  label="5862K227_Neodymium_Bottom_Leg013"
  Placement = pos=(30,30,-4) rot=(-1,0,0;1.5708rad)
  shape: bbox 13.75 x 13.75 x 6.35 mm, 14 faces (baked)
FEATURE [Part::Feature] Part__Feature248  label="91698A721_M3_MagnetScrew14mm_leg_1_Down009"
  Placement = pos=(30,30,-2) rot=(0,0,1;0rad)
  shape: bbox 5.601 x 5.601 x 14.23 mm, 86 faces (baked)
FEATURE [Part::Feature] Part__Feature249  label="91698A721_M3_MagnetScrew14mm_Leg1_Up009"
  Placement = pos=(30,30,2) rot=(0,1,0;3.14159rad)
  shape: bbox 5.601 x 5.601 x 14.23 mm, 86 faces (baked)
FEATURE [Part::Feature] Part__Feature250  label="94459A130_M3_HeatSetInserts_Down_Leg013"
  Placement = pos=(30,30,-10) rot=(1,0,0;1.5708rad)
  shape: bbox 4.74 x 4.749 x 4.466 mm, 209 faces (baked)
FEATURE [Part::Feature] Part__Feature251  label="5862K227_Magnet_Leg_1_Up009"
  Placement = pos=(30,30,4) rot=(-1,0,0;1.5708rad)
  shape: bbox 13.75 x 13.75 x 6.35 mm, 14 faces (baked)
FEATURE [Part::MultiFuse] Fusion087  label="coupledMagnetsV1-M3Large008"
  Placement = pos=(107.5,160,81.25) rot=(0,0,1;0rad)
  Shapes = -> [Part__Feature247,Part__Feature248,Part__Feature249,Part__Feature250,Part__Feature251]
FEATURE [Part::MultiFuse] Fusion088  label="magnetMountsLevel002"
  Shapes = -> [Fusion084,Fusion085,Fusion086,Fusion087]
FEATURE [Part::Feature] Part__Feature252  label="5862K227_Neodymium_Bottom_Leg014"
  Placement = pos=(30,30,-4) rot=(-1,0,0;1.5708rad)
  shape: bbox 13.75 x 13.75 x 6.35 mm, 14 faces (baked)
FEATURE [Part::Feature] Part__Feature253  label="91698A721_M3_MagnetScrew14mm_leg_1_Down010"
  Placement = pos=(30,30,-2) rot=(0,0,1;0rad)
  shape: bbox 5.601 x 5.601 x 14.23 mm, 86 faces (baked)
FEATURE [Part::Feature] Part__Feature254  label="91698A721_M3_MagnetScrew14mm_Leg1_Up010"
  Placement = pos=(30,30,2) rot=(0,1,0;3.14159rad)
  shape: bbox 5.601 x 5.601 x 14.23 mm, 86 faces (baked)
FEATURE [Part::Feature] Part__Feature255  label="94459A130_M3_HeatSetInserts_Down_Leg014"
  Placement = pos=(30,30,-10) rot=(1,0,0;1.5708rad)
  shape: bbox 4.74 x 4.749 x 4.466 mm, 209 faces (baked)
FEATURE [Part::Feature] Part__Feature256  label="5862K227_Magnet_Leg_1_Up010"
  Placement = pos=(30,30,4) rot=(-1,0,0;1.5708rad)
  shape: bbox 13.75 x 13.75 x 6.35 mm, 14 faces (baked)
FEATURE [Part::MultiFuse] Fusion089  label="coupledMagnetsV1-M3Large009"
  Placement = pos=(189.5,210,20) rot=(0,0,1;0rad)
  Shapes = -> [Part__Feature252,Part__Feature253,Part__Feature254,Part__Feature255,Part__Feature256]
FEATURE [Sketcher::SketchObject] Sketch119  label="Supports-Level2"
  FullyConstrained = true
  sketch-geometry (5):
    g0: Circle CenterX=120 CenterY=37 CenterZ=0 NormalX=0 NormalY=0 NormalZ=1 AngleXU=0 Radius=8
    g1: Circle CenterX=238 CenterY=170 CenterZ=0 NormalX=0 NormalY=0 NormalZ=1 AngleXU=0 Radius=8
    g2: Circle CenterX=37 CenterY=130 CenterZ=0 NormalX=0 NormalY=0 NormalZ=1 AngleXU=0 Radius=8
    g3: Circle CenterX=55.5 CenterY=240 CenterZ=0 NormalX=0 NormalY=0 NormalZ=1 AngleXU=0 Radius=8
    g4: Circle CenterX=219.5 CenterY=240 CenterZ=0 NormalX=0 NormalY=0 NormalZ=1 AngleXU=0 Radius=8
  constraints (15):
    c: DistanceX(g0) = 120
    c: DistanceY(g0) = 37
    c: Horizontal(g3,g4)
    c: DistanceY(g2) = 130
    c: Equal(g1,g0)
    c: Equal(g1,g2)
    c: Equal(g1,g3)
    c: Equal(g1,g4)
    c: Diameter(g1) = 16
    c: DistanceY(g3) = 240
    c: DistanceX(g0,g1) = 118
    c: DistanceX(g0,g4) = 99.5
    c: DistanceX(g2) = 37
    c: DistanceX(g3) = 55.5
    c: DistanceY(g2,g1) = 40
FEATURE [Sketcher::SketchObject] Sketch120  label="justHoles-M4Cutsand M3Heats Sets"
  FullyConstrained = true
  sketch-geometry (15):
    g0: Circle CenterX=120 CenterY=37 CenterZ=0 NormalX=0 NormalY=0 NormalZ=1 AngleXU=0 Radius=2
    g1: Circle CenterX=238 CenterY=170 CenterZ=0 NormalX=0 NormalY=0 NormalZ=1 AngleXU=0 Radius=2
    g2: Circle CenterX=37 CenterY=130 CenterZ=0 NormalX=0 NormalY=0 NormalZ=1 AngleXU=0 Radius=2
    g3: Circle CenterX=55.5 CenterY=240 CenterZ=0 NormalX=0 NormalY=0 NormalZ=1 AngleXU=0 Radius=2
    g4: Circle CenterX=219.5 CenterY=240 CenterZ=0 NormalX=0 NormalY=0 NormalZ=1 AngleXU=0 Radius=2
    g5: Circle CenterX=20 CenterY=255 CenterZ=0 NormalX=0 NormalY=0 NormalZ=1 AngleXU=0 Radius=2.125
    g6: Circle CenterX=30 CenterY=245 CenterZ=0 NormalX=0 NormalY=0 NormalZ=1 AngleXU=0 Radius=2.125
    g7: Circle CenterX=245 CenterY=245 CenterZ=0 NormalX=0 NormalY=0 NormalZ=1 AngleXU=0 Radius=2.125
    g8: Circle CenterX=255 CenterY=255 CenterZ=0 NormalX=0 NormalY=0 NormalZ=1 AngleXU=0 Radius=2.125
    g9: Circle CenterX=20 CenterY=20 CenterZ=0 NormalX=0 NormalY=0 NormalZ=1 AngleXU=0 Radius=2.125
    g10: Circle CenterX=30 CenterY=30 CenterZ=0 NormalX=0 NormalY=0 NormalZ=1 AngleXU=0 Radius=2.125
    g11: Circle CenterX=245 CenterY=30 CenterZ=0 NormalX=0 NormalY=0 NormalZ=1 AngleXU=0 Radius=2.125
    g12: Circle CenterX=255 CenterY=20 CenterZ=0 NormalX=0 NormalY=0 NormalZ=1 AngleXU=0 Radius=2.125
    g13: Circle CenterX=45 CenterY=212 CenterZ=0 NormalX=0 NormalY=0 NormalZ=1 AngleXU=0 Radius=15.1
    g14: Circle CenterX=230 CenterY=212 CenterZ=0 NormalX=0 NormalY=0 NormalZ=1 AngleXU=0 Radius=15.1
  constraints (42):
    c: DistanceY(g0) = 37
    c: Horizontal(g3,g4)
    c: DistanceY(g2) = 130
    c: Equal(g1,g0)
    c: Equal(g1,g2)
    c: Equal(g1,g3)
    c: Equal(g1,g4)
    c: Diameter(g1) = 4
    c: DistanceY(g3) = 240
    c: Equal(g11,g12)
    c: Equal(g11,g10)
    c: Equal(g11,g9)
    c: Equal(g11, g5-g8) x4
    c: Diameter(g11) = 4.25
    c: Horizontal(g9,g12)
    c: Vertical(g9,g5)
    c: Vertical(g12,g8)
    c: Horizontal(g5,g8)
    c: Horizontal(g11,g10)
    c: Vertical(g10,g6)
    c: Vertical(g11,g7)
    c: Horizontal(g6,g7)
    c: DistanceX(g9) = 20
    c: DistanceY(g9) = 20
    c: DistanceY(g10) = 30
    c: DistanceX(g10) = 30
    c: DistanceX(g10,g11) = 215
    c: DistanceX(g9,g12) = 235
    c: DistanceY(g10,g6) = 215
    c: DistanceY(g9,g5) = 235
    c: DistanceX(g0) = 120
    c: DistanceX(g2) = 37
    c: DistanceX(g3) = 55.5
    c: DistanceX(g4) = 219.5
    c: DistanceX(g1) = 238
    c: DistanceY(g1) = 170
    c: DistanceX(g13) = 45
    c: DistanceY(g13) = 212
    c: Horizontal(g13,g14)
    c: DistanceX(g13,g14) = 185
    c: Equal(g13,g14)
    c: Diameter(g13) = 30.2
FEATURE [Sketcher::SketchObject] Sketch121  label="Supports-BottomLid"
  FullyConstrained = true
  Placement = pos=(0,0,27.5) rot=(0,0,1;0rad)
  sketch-geometry (5):
    g0: Circle CenterX=120 CenterY=37 CenterZ=0 NormalX=0 NormalY=0 NormalZ=1 AngleXU=0 Radius=8
    g1: Circle CenterX=238 CenterY=170 CenterZ=0 NormalX=0 NormalY=0 NormalZ=1 AngleXU=0 Radius=8
    g2: Circle CenterX=37 CenterY=130 CenterZ=0 NormalX=0 NormalY=0 NormalZ=1 AngleXU=0 Radius=8
    g3: Circle CenterX=55.5 CenterY=240 CenterZ=0 NormalX=0 NormalY=0 NormalZ=1 AngleXU=0 Radius=8
    g4: Circle CenterX=219.5 CenterY=240 CenterZ=0 NormalX=0 NormalY=0 NormalZ=1 AngleXU=0 Radius=8
  constraints (15):
    c: DistanceX(g0) = 120
    c: DistanceY(g0) = 37
    c: Horizontal(g3,g4)
    c: DistanceY(g2) = 130
    c: Equal(g1,g0)
    c: Equal(g1,g2)
    c: Equal(g1,g3)
    c: Equal(g1,g4)
    c: Diameter(g1) = 16
    c: DistanceY(g3) = 240
    c: DistanceX(g1) = 238
    c: DistanceX(g2) = 37
    c: DistanceX(g3) = 55.5
    c: DistanceX(g4) = 219.5
    c: DistanceY(g1) = 170
FEATURE [Part::Feature] Part__Feature257  label="91502A126_Blue-Dyed Zinc-Plated Alloy Steel Socket Head Screw"
  Placement = pos=(20,20,-9) rot=(0,1,0;3.14159rad)
  shape: bbox 7.001 x 7.001 x 18.15 mm, 110 faces (baked)
FEATURE [Part::Feature] Part__Feature258  label="91502A126_Blue-Dyed Zinc-Plated Alloy Steel Socket Head Screw001"
  Placement = pos=(30,30,-9) rot=(0,1,0;3.14159rad)
  shape: bbox 7.001 x 7.001 x 18.15 mm, 110 faces (baked)
FEATURE [Part::Extrusion] Extrude046  label="magSupportsLevel2"
  Base = -> Sketch119
  Dir = (0,0,1)
  DirMode = 2
  FaceMakerClass = Part::FaceMakerBullseye
  LengthFwd = 12.5
  LengthRev = 0
  Solid = true
  Symmetric = false
FEATURE [Part::MultiFuse] Fusion090  label="level02s002"
  Shapes = -> [Extrude046,Fusion082]
FEATURE [Sketcher::SketchObject] Sketch122  label="SupportCuts-BottomLid001"
  FullyConstrained = true
  Placement = pos=(0,0,25) rot=(0,0,1;0rad)
  sketch-geometry (5):
    g0: Circle CenterX=120 CenterY=37 CenterZ=0 NormalX=0 NormalY=0 NormalZ=1 AngleXU=0 Radius=2
    g1: Circle CenterX=238 CenterY=170 CenterZ=0 NormalX=0 NormalY=0 NormalZ=1 AngleXU=0 Radius=2
    g2: Circle CenterX=37 CenterY=130 CenterZ=0 NormalX=0 NormalY=0 NormalZ=1 AngleXU=0 Radius=2
    g3: Circle CenterX=55.5 CenterY=240 CenterZ=0 NormalX=0 NormalY=0 NormalZ=1 AngleXU=0 Radius=2
    g4: Circle CenterX=219.5 CenterY=240 CenterZ=0 NormalX=0 NormalY=0 NormalZ=1 AngleXU=0 Radius=2
  constraints (15):
    c: DistanceY(g0) = 37
    c: Horizontal(g3,g4)
    c: DistanceY(g2) = 130
    c: Equal(g1,g0)
    c: Equal(g1,g2)
    c: Equal(g1,g3)
    c: Equal(g1,g4)
    c: Diameter(g1) = 4
    c: DistanceY(g3) = 240
    c: DistanceX(g0) = 120
    c: DistanceX(g1) = 238
    c: DistanceY(g1) = 170
    c: DistanceX(g4) = 219.5
    c: DistanceX(g3) = 55.5
    c: DistanceX(g2) = 37
FEATURE [Part::Extrusion] Extrude047  label="BottomLidSupports"
  Base = -> Sketch121
  Dir = (0,0,1)
  DirMode = 2
  FaceMakerClass = Part::FaceMakerBullseye
  LengthFwd = 50
  LengthRev = 0
  Solid = true
  Symmetric = false
FEATURE [Sketcher::SketchObject] Sketch123
  FullyConstrained = true
  sketch-geometry (4):
    g0: LineSegment StartX=0 StartY=275 StartZ=0 EndX=275 EndY=275 EndZ=0
    g1: LineSegment StartX=275 StartY=275 StartZ=0 EndX=275 EndY=0 EndZ=0
    g2: LineSegment StartX=275 StartY=0 StartZ=0 EndX=0 EndY=0 EndZ=0
    g3: LineSegment StartX=0 StartY=0 StartZ=0 EndX=0 EndY=275 EndZ=0
  constraints (11):
    c: Coincident(g0,g1)
    c: Coincident(g1,g2)
    c: Coincident(g2,g3)
    c: Coincident(g3,g0)
    c: Horizontal(g0)
    c: Horizontal(g2)
    c: Vertical(g1)
    c: Vertical(g3)
    c: Coincident(g2,g-1)
    c: DistanceX(g2,g2) = 275
    c: DistanceY(g3,g3) = 275
FEATURE [Sketcher::SketchObject] Sketch124
  FullyConstrained = true
  Placement = pos=(0,0,175.1) rot=(0,0,1;0rad)
  sketch-geometry (5):
    g0: GeomPoint X=137.5 Y=137.5 Z=0
    g1: LineSegment StartX=137.55 StartY=137.55 StartZ=0 EndX=137.55 EndY=137.45 EndZ=0
    g2: LineSegment StartX=137.55 StartY=137.45 StartZ=0 EndX=137.45 EndY=137.45 EndZ=0
    g3: LineSegment StartX=137.45 StartY=137.45 StartZ=0 EndX=137.45 EndY=137.55 EndZ=0
    g4: LineSegment StartX=137.45 StartY=137.55 StartZ=0 EndX=137.55 EndY=137.55 EndZ=0
  constraints (14):
    c: Coincident(g1,g2)
    c: Horizontal(g2)
    c: Vertical(g1)
    c: DistanceX(g2,g2) = 0.1
    c: DistanceX(g2,g0) = 0.05
    c: DistanceY(g1,g1) = 0.1
    c: DistanceY(g1,g0) = -0.05
    c: DistanceX(g0) = 137.5
    c: DistanceY(g0) = 137.5
    c: Coincident(g3,g2)
    c: Vertical(g3)
    c: Coincident(g4,g3)
    c: Coincident(g4,g1)
    c: Horizontal(g4)
FEATURE [Part::Loft] Loft030  label="outerLayer029"
  Closed = false
  MaxDegree = 5
  Ruled = false
  Sections = -> [Sketch123,Sketch124]
  Solid = true
FEATURE [Part::MultiCommon] Common031  label="BottomLidSupports001"
  Shapes = -> [Extrude047,Loft030]
FEATURE [Part::MultiFuse] Fusion091  label="bottomLidCover"
  Shapes = -> [Common021,Common031]
FEATURE [Part::Extrusion] Extrude048  label="levelCuts"
  Base = -> Sketch120
  Dir = (0,0,1)
  DirMode = 2
  FaceMakerClass = Part::FaceMakerBullseye
  LengthFwd = 20
  LengthRev = 0
  Solid = true
  Symmetric = false
FEATURE [Sketcher::SketchObject] Sketch125  label="justHoles-M4Cutsand M3Heats Sets001"
  FullyConstrained = true
  sketch-geometry (13):
    g0: Circle CenterX=137.5 CenterY=37 CenterZ=0 NormalX=0 NormalY=0 NormalZ=1 AngleXU=0 Radius=2
    g1: Circle CenterX=238 CenterY=130 CenterZ=0 NormalX=0 NormalY=0 NormalZ=1 AngleXU=0 Radius=2
    g2: Circle CenterX=37 CenterY=130 CenterZ=0 NormalX=0 NormalY=0 NormalZ=1 AngleXU=0 Radius=2
    g3: Circle CenterX=55.5 CenterY=240 CenterZ=0 NormalX=0 NormalY=0 NormalZ=1 AngleXU=0 Radius=2
    g4: Circle CenterX=219.5 CenterY=240 CenterZ=0 NormalX=0 NormalY=0 NormalZ=1 AngleXU=0 Radius=2
    g5: Circle CenterX=20 CenterY=255 CenterZ=0 NormalX=0 NormalY=0 NormalZ=1 AngleXU=0 Radius=2.125
    g6: Circle CenterX=30 CenterY=245 CenterZ=0 NormalX=0 NormalY=0 NormalZ=1 AngleXU=0 Radius=2.125
    g7: Circle CenterX=245 CenterY=245 CenterZ=0 NormalX=0 NormalY=0 NormalZ=1 AngleXU=0 Radius=2.125
    g8: Circle CenterX=255 CenterY=255 CenterZ=0 NormalX=0 NormalY=0 NormalZ=1 AngleXU=0 Radius=2.125
    g9: Circle CenterX=20 CenterY=20 CenterZ=0 NormalX=0 NormalY=0 NormalZ=1 AngleXU=0 Radius=2.125
    g10: Circle CenterX=30 CenterY=30 CenterZ=0 NormalX=0 NormalY=0 NormalZ=1 AngleXU=0 Radius=2.125
    g11: Circle CenterX=245 CenterY=30 CenterZ=0 NormalX=0 NormalY=0 NormalZ=1 AngleXU=0 Radius=2.125
    g12: Circle CenterX=255 CenterY=20 CenterZ=0 NormalX=0 NormalY=0 NormalZ=1 AngleXU=0 Radius=2.125
  constraints (36):
    c: DistanceX(g0) = 137.5
    c: DistanceY(g0) = 37
    c: Horizontal(g2,g1)
    c: Horizontal(g3,g4)
    c: DistanceY(g2) = 130
    c: DistanceX(g2,g0) = 100.5
    c: DistanceX(g0,g1) = 100.5
    c: DistanceX(g3,g0) = 82
    c: DistanceX(g0,g4) = 82
    c: Equal(g1,g0)
    c: Equal(g1,g2)
    c: Equal(g1,g3)
    c: Equal(g1,g4)
    c: Diameter(g1) = 4
    c: DistanceY(g3) = 240
    c: Equal(g11,g12)
    c: Equal(g11,g10)
    c: Equal(g11,g9)
    c: Equal(g11, g5-g8) x4
    c: Diameter(g11) = 4.25
    c: Horizontal(g9,g12)
    c: Vertical(g9,g5)
    c: Vertical(g12,g8)
    c: Horizontal(g5,g8)
    c: Horizontal(g11,g10)
    c: Vertical(g10,g6)
    c: Vertical(g11,g7)
    c: Horizontal(g6,g7)
    c: DistanceX(g9) = 20
    c: DistanceY(g9) = 20
    c: DistanceY(g10) = 30
    c: DistanceX(g10) = 30
    c: DistanceX(g10,g11) = 215
    c: DistanceX(g9,g12) = 235
    c: DistanceY(g10,g6) = 215
    c: DistanceY(g9,g5) = 235
FEATURE [Part::Extrusion] Extrude049  label="lidCuts001"
  Base = -> Sketch125
  Dir = (0,0,1)
  DirMode = 2
  FaceMakerClass = Part::FaceMakerBullseye
  LengthFwd = 50
  LengthRev = 0
  Solid = true
  Symmetric = false
FEATURE [Part::Cut] Cut017  label="level2s002"
  Base = -> Fusion090
  Tool = -> Extrude048
FEATURE [Part::MultiFuse] Fusion092  label="MagnetsLevel2"
  Shapes = -> [Fusion089,Fusion080,Fusion079,Fusion078,Fusion023]
FEATURE [Part::Extrusion] Extrude050
  Base = -> Sketch122
  Dir = (0,0,1)
  DirMode = 2
  FaceMakerClass = Part::FaceMakerBullseye
  LengthFwd = 10
  LengthRev = 0
  Solid = true
  Symmetric = false
FEATURE [Part::Cut] Cut018  label="bottomLidCover001"
  Base = -> Fusion091
  Tool = -> Extrude050
FEATURE [Sketcher::SketchObject] Sketch126  label="justHoles-M4Cutsand M3Heats Sets002"
  FullyConstrained = true
  sketch-geometry (8):
    g0: Circle CenterX=20 CenterY=255 CenterZ=0 NormalX=0 NormalY=0 NormalZ=1 AngleXU=0 Radius=2.8
    g1: Circle CenterX=30 CenterY=245 CenterZ=0 NormalX=0 NormalY=0 NormalZ=1 AngleXU=0 Radius=2.8
    g2: Circle CenterX=245 CenterY=245 CenterZ=0 NormalX=0 NormalY=0 NormalZ=1 AngleXU=0 Radius=2.8
    g3: Circle CenterX=255 CenterY=255 CenterZ=0 NormalX=0 NormalY=0 NormalZ=1 AngleXU=0 Radius=2.8
    g4: Circle CenterX=20 CenterY=20 CenterZ=0 NormalX=0 NormalY=0 NormalZ=1 AngleXU=0 Radius=2.8
    g5: Circle CenterX=30 CenterY=30 CenterZ=0 NormalX=0 NormalY=0 NormalZ=1 AngleXU=0 Radius=2.8
    g6: Circle CenterX=245 CenterY=30 CenterZ=0 NormalX=0 NormalY=0 NormalZ=1 AngleXU=0 Radius=2.8
    g7: Circle CenterX=255 CenterY=20 CenterZ=0 NormalX=0 NormalY=0 NormalZ=1 AngleXU=0 Radius=2.8
  constraints (21):
    c: Equal(g6,g7)
    c: Equal(g6,g5)
    c: Equal(g6,g4)
    c: Equal(g6, g0-g3) x4
    c: Diameter(g6) = 5.6
    c: Horizontal(g4,g7)
    c: Vertical(g4,g0)
    c: Vertical(g7,g3)
    c: Horizontal(g0,g3)
    c: Horizontal(g6,g5)
    c: Vertical(g5,g1)
    c: Vertical(g6,g2)
    c: Horizontal(g1,g2)
    c: DistanceX(g4) = 20
    c: DistanceY(g4) = 20
    c: DistanceY(g5) = 30
    c: DistanceX(g5) = 30
    c: DistanceX(g5,g6) = 215
    c: DistanceX(g4,g7) = 235
    c: DistanceY(g5,g1) = 215
    c: DistanceY(g4,g0) = 235
FEATURE [Part::Extrusion] Extrude051  label="legCuts001"
  Base = -> Sketch126
  Dir = (0,0,1)
  DirMode = 2
  FaceMakerClass = Part::FaceMakerBullseye
  LengthFwd = 75
  LengthRev = 0
  Reversed = true
  Solid = true
  Symmetric = false
FEATURE [Part::Feature] Part__Feature259  label="5862K227_Neodymium_Bottom_Leg015"
  Placement = pos=(30,30,-4) rot=(-1,0,0;1.5708rad)
  shape: bbox 13.75 x 13.75 x 6.35 mm, 14 faces (baked)
FEATURE [Part::Feature] Part__Feature260  label="91698A721_M3_MagnetScrew14mm_leg_1_Down011"
  Placement = pos=(30,30,-2) rot=(0,0,1;0rad)
  shape: bbox 5.601 x 5.601 x 14.23 mm, 86 faces (baked)
FEATURE [Part::Feature] Part__Feature261  label="91698A721_M3_MagnetScrew14mm_Leg1_Up011"
  Placement = pos=(30,30,2) rot=(0,1,0;3.14159rad)
  shape: bbox 5.601 x 5.601 x 14.23 mm, 86 faces (baked)
FEATURE [Part::Feature] Part__Feature262  label="94459A130_M3_HeatSetInserts_Down_Leg015"
  Placement = pos=(30,30,-10) rot=(1,0,0;1.5708rad)
  shape: bbox 4.74 x 4.749 x 4.466 mm, 209 faces (baked)
FEATURE [Part::Feature] Part__Feature263  label="5862K227_Magnet_Leg_1_Up011"
  Placement = pos=(30,30,4) rot=(-1,0,0;1.5708rad)
  shape: bbox 13.75 x 13.75 x 6.35 mm, 14 faces (baked)
FEATURE [Part::MultiFuse] Fusion094  label="coupledMagnetsV1-M3Large010"
  Placement = pos=(-60,-60,-75) rot=(0,0,1;0rad)
  Shapes = -> [Part__Feature259,Part__Feature260,Part__Feature261,Part__Feature262,Part__Feature263]
FEATURE [Part::Feature] Part__Feature264  label="5862K227_Neodymium_Bottom_Leg016"
  Placement = pos=(30,30,-4) rot=(-1,0,0;1.5708rad)
  shape: bbox 13.75 x 13.75 x 6.35 mm, 14 faces (baked)
FEATURE [Part::Feature] Part__Feature265  label="91698A721_M3_MagnetScrew14mm_leg_1_Down012"
  Placement = pos=(30,30,-2) rot=(0,0,1;0rad)
  shape: bbox 5.601 x 5.601 x 14.23 mm, 86 faces (baked)
FEATURE [Part::Feature] Part__Feature266  label="91698A721_M3_MagnetScrew14mm_Leg1_Up012"
  Placement = pos=(30,30,2) rot=(0,1,0;3.14159rad)
  shape: bbox 5.601 x 5.601 x 14.23 mm, 86 faces (baked)
FEATURE [Part::Feature] Part__Feature267  label="94459A130_M3_HeatSetInserts_Down_Leg016"
  Placement = pos=(30,30,-10) rot=(1,0,0;1.5708rad)
  shape: bbox 4.74 x 4.749 x 4.466 mm, 209 faces (baked)
FEATURE [Part::Feature] Part__Feature268  label="5862K227_Magnet_Leg_1_Up012"
  Placement = pos=(30,30,4) rot=(-1,0,0;1.5708rad)
  shape: bbox 13.75 x 13.75 x 6.35 mm, 14 faces (baked)
FEATURE [Part::MultiFuse] Fusion095  label="coupledMagnetsV1-M3Large011"
  Placement = pos=(-35,-35,-75) rot=(0,0,1;0rad)
  Shapes = -> [Part__Feature264,Part__Feature265,Part__Feature266,Part__Feature267,Part__Feature268]
FEATURE [Sketcher::SketchObject] Sketch127  label="magnetCuts"
  FullyConstrained = true
  Placement = pos=(0,0,-75) rot=(0,0,1;0rad)
  sketch-geometry (8):
    g0: Circle CenterX=-5 CenterY=-5 CenterZ=0 NormalX=0 NormalY=0 NormalZ=1 AngleXU=0 Radius=6.5
    g1: Circle CenterX=-30 CenterY=-30 CenterZ=0 NormalX=0 NormalY=0 NormalZ=1 AngleXU=0 Radius=6.5
    g2: Circle CenterX=280 CenterY=-5 CenterZ=0 NormalX=0 NormalY=0 NormalZ=1 AngleXU=0 Radius=6.5
    g3: Circle CenterX=305 CenterY=-30 CenterZ=0 NormalX=0 NormalY=0 NormalZ=1 AngleXU=0 Radius=6.5
    g4: Circle CenterX=280 CenterY=280 CenterZ=0 NormalX=0 NormalY=0 NormalZ=1 AngleXU=0 Radius=6.5
    g5: Circle CenterX=305 CenterY=305 CenterZ=0 NormalX=0 NormalY=0 NormalZ=1 AngleXU=0 Radius=6.5
    g6: Circle CenterX=-30 CenterY=305 CenterZ=0 NormalX=0 NormalY=0 NormalZ=1 AngleXU=0 Radius=6.5
    g7: Circle CenterX=-5 CenterY=280 CenterZ=0 NormalX=0 NormalY=0 NormalZ=1 AngleXU=0 Radius=6.5
  constraints (24):
    c: Horizontal(g1,g3)
    c: Vertical(g1,g6)
    c: Horizontal(g6,g5)
    c: Vertical(g3,g5)
    c: Horizontal(g0,g2)
    c: Vertical(g7,g0)
    c: Horizontal(g7,g4)
    c: Vertical(g4,g2)
    c: DistanceX(g1) = -30
    c: DistanceY(g1) = -30
    c: DistanceY(g0) = -5
    c: DistanceX(g0) = -5
    c: DistanceY(g1,g6) = 335
    c: DistanceY(g0,g7) = 285
    c: DistanceX(g0,g2) = 285
    c: DistanceX(g1,g3) = 335
    c: Equal(g6,g7)
    c: Equal(g6,g4)
    c: Equal(g6,g5)
    c: Equal(g6,g2)
    c: Equal(g6,g3)
    c: Equal(g6,g1)
    c: Equal(g6,g0)
    c: Diameter(g6) = 13
FEATURE [Sketcher::SketchObject] Sketch128  label="magnetHeatsetHoldCuts001"
  FullyConstrained = true
  Placement = pos=(0,0,-75) rot=(0,0,1;0rad)
  sketch-geometry (8):
    g0: Circle CenterX=-5 CenterY=-5 CenterZ=0 NormalX=0 NormalY=0 NormalZ=1 AngleXU=0 Radius=2
    g1: Circle CenterX=-30 CenterY=-30 CenterZ=0 NormalX=0 NormalY=0 NormalZ=1 AngleXU=0 Radius=2
    g2: Circle CenterX=280 CenterY=-5 CenterZ=0 NormalX=0 NormalY=0 NormalZ=1 AngleXU=0 Radius=2
    g3: Circle CenterX=305 CenterY=-30 CenterZ=0 NormalX=0 NormalY=0 NormalZ=1 AngleXU=0 Radius=2
    g4: Circle CenterX=280 CenterY=280 CenterZ=0 NormalX=0 NormalY=0 NormalZ=1 AngleXU=0 Radius=2
    g5: Circle CenterX=305 CenterY=305 CenterZ=0 NormalX=0 NormalY=0 NormalZ=1 AngleXU=0 Radius=2
    g6: Circle CenterX=-30 CenterY=305 CenterZ=0 NormalX=0 NormalY=0 NormalZ=1 AngleXU=0 Radius=2
    g7: Circle CenterX=-5 CenterY=280 CenterZ=0 NormalX=0 NormalY=0 NormalZ=1 AngleXU=0 Radius=2
  constraints (24):
    c: Horizontal(g1,g3)
    c: Vertical(g1,g6)
    c: Horizontal(g6,g5)
    c: Vertical(g3,g5)
    c: Horizontal(g0,g2)
    c: Vertical(g7,g0)
    c: Horizontal(g7,g4)
    c: Vertical(g4,g2)
    c: DistanceX(g1) = -30
    c: DistanceY(g1) = -30
    c: DistanceY(g0) = -5
    c: DistanceX(g0) = -5
    c: DistanceY(g1,g6) = 335
    c: DistanceY(g0,g7) = 285
    c: DistanceX(g0,g2) = 285
    c: DistanceX(g1,g3) = 335
    c: Equal(g6,g7)
    c: Equal(g6,g4)
    c: Equal(g6,g5)
    c: Equal(g6,g2)
    c: Equal(g6,g3)
    c: Equal(g6,g1)
    c: Equal(g6,g0)
    c: Diameter(g6) = 4
FEATURE [Part::Extrusion] Extrude052
  Base = -> Sketch127
  Dir = (0,0,1)
  DirMode = 2
  FaceMakerClass = Part::FaceMakerBullseye
  LengthFwd = 7.5
  LengthRev = 0
  Solid = true
  Symmetric = false
FEATURE [Part::Extrusion] Extrude053
  Base = -> Sketch128
  Dir = (0,0,1)
  DirMode = 2
  FaceMakerClass = Part::FaceMakerBullseye
  LengthFwd = 20
  LengthRev = 0
  Solid = true
  Symmetric = false
FEATURE [Part::MultiFuse] Fusion096  label="legCuts"
  Shapes = -> [Extrude052,Extrude053]
FEATURE [Part::MultiFuse] Fusion097  label="legCuts002"
  Shapes = -> [Extrude051,Fusion096]
FEATURE [Sketcher::SketchObject] Sketch129  label="justHoles-M4Cutsand M3Heats Sets003"
  FullyConstrained = true
  sketch-geometry (8):
    g0: Circle CenterX=20 CenterY=255 CenterZ=0 NormalX=0 NormalY=0 NormalZ=1 AngleXU=0 Radius=2.8
    g1: Circle CenterX=30 CenterY=245 CenterZ=0 NormalX=0 NormalY=0 NormalZ=1 AngleXU=0 Radius=2.8
    g2: Circle CenterX=245 CenterY=245 CenterZ=0 NormalX=0 NormalY=0 NormalZ=1 AngleXU=0 Radius=2.8
    g3: Circle CenterX=255 CenterY=255 CenterZ=0 NormalX=0 NormalY=0 NormalZ=1 AngleXU=0 Radius=2.8
    g4: Circle CenterX=20 CenterY=20 CenterZ=0 NormalX=0 NormalY=0 NormalZ=1 AngleXU=0 Radius=2.8
    g5: Circle CenterX=30 CenterY=30 CenterZ=0 NormalX=0 NormalY=0 NormalZ=1 AngleXU=0 Radius=2.8
    g6: Circle CenterX=245 CenterY=30 CenterZ=0 NormalX=0 NormalY=0 NormalZ=1 AngleXU=0 Radius=2.8
    g7: Circle CenterX=255 CenterY=20 CenterZ=0 NormalX=0 NormalY=0 NormalZ=1 AngleXU=0 Radius=2.8
  constraints (21):
    c: Equal(g6,g7)
    c: Equal(g6,g5)
    c: Equal(g6,g4)
    c: Equal(g6, g0-g3) x4
    c: Diameter(g6) = 5.6
    c: Horizontal(g4,g7)
    c: Vertical(g4,g0)
    c: Vertical(g7,g3)
    c: Horizontal(g0,g3)
    c: Horizontal(g6,g5)
    c: Vertical(g5,g1)
    c: Vertical(g6,g2)
    c: Horizontal(g1,g2)
    c: DistanceX(g4) = 20
    c: DistanceY(g4) = 20
    c: DistanceY(g5) = 30
    c: DistanceX(g5) = 30
    c: DistanceX(g5,g6) = 215
    c: DistanceX(g4,g7) = 235
    c: DistanceY(g5,g1) = 215
    c: DistanceY(g4,g0) = 235
FEATURE [Part::Extrusion] Extrude054  label="legCuts003"
  Base = -> Sketch129
  Dir = (0,0,1)
  DirMode = 2
  FaceMakerClass = Part::FaceMakerBullseye
  LengthFwd = 75
  LengthRev = 0
  Reversed = true
  Solid = true
  Symmetric = false
FEATURE [Sketcher::SketchObject] Sketch130  label="magnetCuts001"
  FullyConstrained = true
  Placement = pos=(0,0,-75) rot=(0,0,1;0rad)
  sketch-geometry (8):
    g0: Circle CenterX=-5 CenterY=-5 CenterZ=0 NormalX=0 NormalY=0 NormalZ=1 AngleXU=0 Radius=6.5
    g1: Circle CenterX=-30 CenterY=-30 CenterZ=0 NormalX=0 NormalY=0 NormalZ=1 AngleXU=0 Radius=6.5
    g2: Circle CenterX=280 CenterY=-5 CenterZ=0 NormalX=0 NormalY=0 NormalZ=1 AngleXU=0 Radius=6.5
    g3: Circle CenterX=305 CenterY=-30 CenterZ=0 NormalX=0 NormalY=0 NormalZ=1 AngleXU=0 Radius=6.5
    g4: Circle CenterX=280 CenterY=280 CenterZ=0 NormalX=0 NormalY=0 NormalZ=1 AngleXU=0 Radius=6.5
    g5: Circle CenterX=305 CenterY=305 CenterZ=0 NormalX=0 NormalY=0 NormalZ=1 AngleXU=0 Radius=6.5
    g6: Circle CenterX=-30 CenterY=305 CenterZ=0 NormalX=0 NormalY=0 NormalZ=1 AngleXU=0 Radius=6.5
    g7: Circle CenterX=-5 CenterY=280 CenterZ=0 NormalX=0 NormalY=0 NormalZ=1 AngleXU=0 Radius=6.5
  constraints (24):
    c: Horizontal(g1,g3)
    c: Vertical(g1,g6)
    c: Horizontal(g6,g5)
    c: Vertical(g3,g5)
    c: Horizontal(g0,g2)
    c: Vertical(g7,g0)
    c: Horizontal(g7,g4)
    c: Vertical(g4,g2)
    c: DistanceX(g1) = -30
    c: DistanceY(g1) = -30
    c: DistanceY(g0) = -5
    c: DistanceX(g0) = -5
    c: DistanceY(g1,g6) = 335
    c: DistanceY(g0,g7) = 285
    c: DistanceX(g0,g2) = 285
    c: DistanceX(g1,g3) = 335
    c: Equal(g6,g7)
    c: Equal(g6,g4)
    c: Equal(g6,g5)
    c: Equal(g6,g2)
    c: Equal(g6,g3)
    c: Equal(g6,g1)
    c: Equal(g6,g0)
    c: Diameter(g6) = 13
FEATURE [Part::Extrusion] Extrude055
  Base = -> Sketch130
  Dir = (0,0,1)
  DirMode = 2
  FaceMakerClass = Part::FaceMakerBullseye
  LengthFwd = 7.5
  LengthRev = 0
  Solid = true
  Symmetric = false
FEATURE [Sketcher::SketchObject] Sketch131  label="magnetHeatsetHoldCuts002"
  FullyConstrained = true
  Placement = pos=(0,0,-75) rot=(0,0,1;0rad)
  sketch-geometry (8):
    g0: Circle CenterX=-5 CenterY=-5 CenterZ=0 NormalX=0 NormalY=0 NormalZ=1 AngleXU=0 Radius=2
    g1: Circle CenterX=-30 CenterY=-30 CenterZ=0 NormalX=0 NormalY=0 NormalZ=1 AngleXU=0 Radius=2
    g2: Circle CenterX=280 CenterY=-5 CenterZ=0 NormalX=0 NormalY=0 NormalZ=1 AngleXU=0 Radius=2
    g3: Circle CenterX=305 CenterY=-30 CenterZ=0 NormalX=0 NormalY=0 NormalZ=1 AngleXU=0 Radius=2
    g4: Circle CenterX=280 CenterY=280 CenterZ=0 NormalX=0 NormalY=0 NormalZ=1 AngleXU=0 Radius=2
    g5: Circle CenterX=305 CenterY=305 CenterZ=0 NormalX=0 NormalY=0 NormalZ=1 AngleXU=0 Radius=2
    g6: Circle CenterX=-30 CenterY=305 CenterZ=0 NormalX=0 NormalY=0 NormalZ=1 AngleXU=0 Radius=2
    g7: Circle CenterX=-5 CenterY=280 CenterZ=0 NormalX=0 NormalY=0 NormalZ=1 AngleXU=0 Radius=2
  constraints (24):
    c: Horizontal(g1,g3)
    c: Vertical(g1,g6)
    c: Horizontal(g6,g5)
    c: Vertical(g3,g5)
    c: Horizontal(g0,g2)
    c: Vertical(g7,g0)
    c: Horizontal(g7,g4)
    c: Vertical(g4,g2)
    c: DistanceX(g1) = -30
    c: DistanceY(g1) = -30
    c: DistanceY(g0) = -5
    c: DistanceX(g0) = -5
    c: DistanceY(g1,g6) = 335
    c: DistanceY(g0,g7) = 285
    c: DistanceX(g0,g2) = 285
    c: DistanceX(g1,g3) = 335
    c: Equal(g6,g7)
    c: Equal(g6,g4)
    c: Equal(g6,g5)
    c: Equal(g6,g2)
    c: Equal(g6,g3)
    c: Equal(g6,g1)
    c: Equal(g6,g0)
    c: Diameter(g6) = 4
FEATURE [Part::Extrusion] Extrude056
  Base = -> Sketch131
  Dir = (0,0,1)
  DirMode = 2
  FaceMakerClass = Part::FaceMakerBullseye
  LengthFwd = 20
  LengthRev = 0
  Solid = true
  Symmetric = false
FEATURE [Part::MultiFuse] Fusion098  label="legCuts004"
  Shapes = -> [Extrude055,Extrude056]
FEATURE [Part::MultiFuse] Fusion099  label="legCuts005"
  Shapes = -> [Extrude054,Fusion098]
FEATURE [Sketcher::SketchObject] Sketch132  label="justHoles-M4Cutsand M3Heats Sets004"
  FullyConstrained = true
  sketch-geometry (8):
    g0: Circle CenterX=20 CenterY=255 CenterZ=0 NormalX=0 NormalY=0 NormalZ=1 AngleXU=0 Radius=2.8
    g1: Circle CenterX=30 CenterY=245 CenterZ=0 NormalX=0 NormalY=0 NormalZ=1 AngleXU=0 Radius=2.8
    g2: Circle CenterX=245 CenterY=245 CenterZ=0 NormalX=0 NormalY=0 NormalZ=1 AngleXU=0 Radius=2.8
    g3: Circle CenterX=255 CenterY=255 CenterZ=0 NormalX=0 NormalY=0 NormalZ=1 AngleXU=0 Radius=2.8
    g4: Circle CenterX=20 CenterY=20 CenterZ=0 NormalX=0 NormalY=0 NormalZ=1 AngleXU=0 Radius=2.8
    g5: Circle CenterX=30 CenterY=30 CenterZ=0 NormalX=0 NormalY=0 NormalZ=1 AngleXU=0 Radius=2.8
    g6: Circle CenterX=245 CenterY=30 CenterZ=0 NormalX=0 NormalY=0 NormalZ=1 AngleXU=0 Radius=2.8
    g7: Circle CenterX=255 CenterY=20 CenterZ=0 NormalX=0 NormalY=0 NormalZ=1 AngleXU=0 Radius=2.8
  constraints (21):
    c: Equal(g6,g7)
    c: Equal(g6,g5)
    c: Equal(g6,g4)
    c: Equal(g6, g0-g3) x4
    c: Diameter(g6) = 5.6
    c: Horizontal(g4,g7)
    c: Vertical(g4,g0)
    c: Vertical(g7,g3)
    c: Horizontal(g0,g3)
    c: Horizontal(g6,g5)
    c: Vertical(g5,g1)
    c: Vertical(g6,g2)
    c: Horizontal(g1,g2)
    c: DistanceX(g4) = 20
    c: DistanceY(g4) = 20
    c: DistanceY(g5) = 30
    c: DistanceX(g5) = 30
    c: DistanceX(g5,g6) = 215
    c: DistanceX(g4,g7) = 235
    c: DistanceY(g5,g1) = 215
    c: DistanceY(g4,g0) = 235
FEATURE [Part::Extrusion] Extrude057  label="legCuts006"
  Base = -> Sketch132
  Dir = (0,0,1)
  DirMode = 2
  FaceMakerClass = Part::FaceMakerBullseye
  LengthFwd = 75
  LengthRev = 0
  Reversed = true
  Solid = true
  Symmetric = false
FEATURE [Sketcher::SketchObject] Sketch133  label="magnetCuts002"
  FullyConstrained = true
  Placement = pos=(0,0,-75) rot=(0,0,1;0rad)
  sketch-geometry (8):
    g0: Circle CenterX=-5 CenterY=-5 CenterZ=0 NormalX=0 NormalY=0 NormalZ=1 AngleXU=0 Radius=6.5
    g1: Circle CenterX=-30 CenterY=-30 CenterZ=0 NormalX=0 NormalY=0 NormalZ=1 AngleXU=0 Radius=6.5
    g2: Circle CenterX=280 CenterY=-5 CenterZ=0 NormalX=0 NormalY=0 NormalZ=1 AngleXU=0 Radius=6.5
    g3: Circle CenterX=305 CenterY=-30 CenterZ=0 NormalX=0 NormalY=0 NormalZ=1 AngleXU=0 Radius=6.5
    g4: Circle CenterX=280 CenterY=280 CenterZ=0 NormalX=0 NormalY=0 NormalZ=1 AngleXU=0 Radius=6.5
    g5: Circle CenterX=305 CenterY=305 CenterZ=0 NormalX=0 NormalY=0 NormalZ=1 AngleXU=0 Radius=6.5
    g6: Circle CenterX=-30 CenterY=305 CenterZ=0 NormalX=0 NormalY=0 NormalZ=1 AngleXU=0 Radius=6.5
    g7: Circle CenterX=-5 CenterY=280 CenterZ=0 NormalX=0 NormalY=0 NormalZ=1 AngleXU=0 Radius=6.5
  constraints (24):
    c: Horizontal(g1,g3)
    c: Vertical(g1,g6)
    c: Horizontal(g6,g5)
    c: Vertical(g3,g5)
    c: Horizontal(g0,g2)
    c: Vertical(g7,g0)
    c: Horizontal(g7,g4)
    c: Vertical(g4,g2)
    c: DistanceX(g1) = -30
    c: DistanceY(g1) = -30
    c: DistanceY(g0) = -5
    c: DistanceX(g0) = -5
    c: DistanceY(g1,g6) = 335
    c: DistanceY(g0,g7) = 285
    c: DistanceX(g0,g2) = 285
    c: DistanceX(g1,g3) = 335
    c: Equal(g6,g7)
    c: Equal(g6,g4)
    c: Equal(g6,g5)
    c: Equal(g6,g2)
    c: Equal(g6,g3)
    c: Equal(g6,g1)
    c: Equal(g6,g0)
    c: Diameter(g6) = 13
FEATURE [Part::Extrusion] Extrude058
  Base = -> Sketch133
  Dir = (0,0,1)
  DirMode = 2
  FaceMakerClass = Part::FaceMakerBullseye
  LengthFwd = 7.5
  LengthRev = 0
  Solid = true
  Symmetric = false
FEATURE [Sketcher::SketchObject] Sketch134  label="magnetHeatsetHoldCuts003"
  FullyConstrained = true
  Placement = pos=(0,0,-75) rot=(0,0,1;0rad)
  sketch-geometry (8):
    g0: Circle CenterX=-5 CenterY=-5 CenterZ=0 NormalX=0 NormalY=0 NormalZ=1 AngleXU=0 Radius=2
    g1: Circle CenterX=-30 CenterY=-30 CenterZ=0 NormalX=0 NormalY=0 NormalZ=1 AngleXU=0 Radius=2
    g2: Circle CenterX=280 CenterY=-5 CenterZ=0 NormalX=0 NormalY=0 NormalZ=1 AngleXU=0 Radius=2
    g3: Circle CenterX=305 CenterY=-30 CenterZ=0 NormalX=0 NormalY=0 NormalZ=1 AngleXU=0 Radius=2
    g4: Circle CenterX=280 CenterY=280 CenterZ=0 NormalX=0 NormalY=0 NormalZ=1 AngleXU=0 Radius=2
    g5: Circle CenterX=305 CenterY=305 CenterZ=0 NormalX=0 NormalY=0 NormalZ=1 AngleXU=0 Radius=2
    g6: Circle CenterX=-30 CenterY=305 CenterZ=0 NormalX=0 NormalY=0 NormalZ=1 AngleXU=0 Radius=2
    g7: Circle CenterX=-5 CenterY=280 CenterZ=0 NormalX=0 NormalY=0 NormalZ=1 AngleXU=0 Radius=2
  constraints (24):
    c: Horizontal(g1,g3)
    c: Vertical(g1,g6)
    c: Horizontal(g6,g5)
    c: Vertical(g3,g5)
    c: Horizontal(g0,g2)
    c: Vertical(g7,g0)
    c: Horizontal(g7,g4)
    c: Vertical(g4,g2)
    c: DistanceX(g1) = -30
    c: DistanceY(g1) = -30
    c: DistanceY(g0) = -5
    c: DistanceX(g0) = -5
    c: DistanceY(g1,g6) = 335
    c: DistanceY(g0,g7) = 285
    c: DistanceX(g0,g2) = 285
    c: DistanceX(g1,g3) = 335
    c: Equal(g6,g7)
    c: Equal(g6,g4)
    c: Equal(g6,g5)
    c: Equal(g6,g2)
    c: Equal(g6,g3)
    c: Equal(g6,g1)
    c: Equal(g6,g0)
    c: Diameter(g6) = 4
FEATURE [Part::Extrusion] Extrude059
  Base = -> Sketch134
  Dir = (0,0,1)
  DirMode = 2
  FaceMakerClass = Part::FaceMakerBullseye
  LengthFwd = 20
  LengthRev = 0
  Solid = true
  Symmetric = false
FEATURE [Part::MultiFuse] Fusion100  label="legCuts007"
  Shapes = -> [Extrude058,Extrude059]
FEATURE [Part::MultiFuse] Fusion101  label="legCuts008"
  Shapes = -> [Extrude057,Fusion100]
FEATURE [Sketcher::SketchObject] Sketch135  label="justHoles-M4Cutsand M3Heats Sets005"
  FullyConstrained = true
  sketch-geometry (8):
    g0: Circle CenterX=20 CenterY=255 CenterZ=0 NormalX=0 NormalY=0 NormalZ=1 AngleXU=0 Radius=2.8
    g1: Circle CenterX=30 CenterY=245 CenterZ=0 NormalX=0 NormalY=0 NormalZ=1 AngleXU=0 Radius=2.8
    g2: Circle CenterX=245 CenterY=245 CenterZ=0 NormalX=0 NormalY=0 NormalZ=1 AngleXU=0 Radius=2.8
    g3: Circle CenterX=255 CenterY=255 CenterZ=0 NormalX=0 NormalY=0 NormalZ=1 AngleXU=0 Radius=2.8
    g4: Circle CenterX=20 CenterY=20 CenterZ=0 NormalX=0 NormalY=0 NormalZ=1 AngleXU=0 Radius=2.8
    g5: Circle CenterX=30 CenterY=30 CenterZ=0 NormalX=0 NormalY=0 NormalZ=1 AngleXU=0 Radius=2.8
    g6: Circle CenterX=245 CenterY=30 CenterZ=0 NormalX=0 NormalY=0 NormalZ=1 AngleXU=0 Radius=2.8
    g7: Circle CenterX=255 CenterY=20 CenterZ=0 NormalX=0 NormalY=0 NormalZ=1 AngleXU=0 Radius=2.8
  constraints (21):
    c: Equal(g6,g7)
    c: Equal(g6,g5)
    c: Equal(g6,g4)
    c: Equal(g6, g0-g3) x4
    c: Diameter(g6) = 5.6
    c: Horizontal(g4,g7)
    c: Vertical(g4,g0)
    c: Vertical(g7,g3)
    c: Horizontal(g0,g3)
    c: Horizontal(g6,g5)
    c: Vertical(g5,g1)
    c: Vertical(g6,g2)
    c: Horizontal(g1,g2)
    c: DistanceX(g4) = 20
    c: DistanceY(g4) = 20
    c: DistanceY(g5) = 30
    c: DistanceX(g5) = 30
    c: DistanceX(g5,g6) = 215
    c: DistanceX(g4,g7) = 235
    c: DistanceY(g5,g1) = 215
    c: DistanceY(g4,g0) = 235
FEATURE [Part::Extrusion] Extrude060  label="legCuts009"
  Base = -> Sketch135
  Dir = (0,0,1)
  DirMode = 2
  FaceMakerClass = Part::FaceMakerBullseye
  LengthFwd = 75
  LengthRev = 0
  Reversed = true
  Solid = true
  Symmetric = false
FEATURE [Sketcher::SketchObject] Sketch136  label="magnetCuts003"
  FullyConstrained = true
  Placement = pos=(0,0,-75) rot=(0,0,1;0rad)
  sketch-geometry (8):
    g0: Circle CenterX=-5 CenterY=-5 CenterZ=0 NormalX=0 NormalY=0 NormalZ=1 AngleXU=0 Radius=6.5
    g1: Circle CenterX=-30 CenterY=-30 CenterZ=0 NormalX=0 NormalY=0 NormalZ=1 AngleXU=0 Radius=6.5
    g2: Circle CenterX=280 CenterY=-5 CenterZ=0 NormalX=0 NormalY=0 NormalZ=1 AngleXU=0 Radius=6.5
    g3: Circle CenterX=305 CenterY=-30 CenterZ=0 NormalX=0 NormalY=0 NormalZ=1 AngleXU=0 Radius=6.5
    g4: Circle CenterX=280 CenterY=280 CenterZ=0 NormalX=0 NormalY=0 NormalZ=1 AngleXU=0 Radius=6.5
    g5: Circle CenterX=305 CenterY=305 CenterZ=0 NormalX=0 NormalY=0 NormalZ=1 AngleXU=0 Radius=6.5
    g6: Circle CenterX=-30 CenterY=305 CenterZ=0 NormalX=0 NormalY=0 NormalZ=1 AngleXU=0 Radius=6.5
    g7: Circle CenterX=-5 CenterY=280 CenterZ=0 NormalX=0 NormalY=0 NormalZ=1 AngleXU=0 Radius=6.5
  constraints (24):
    c: Horizontal(g1,g3)
    c: Vertical(g1,g6)
    c: Horizontal(g6,g5)
    c: Vertical(g3,g5)
    c: Horizontal(g0,g2)
    c: Vertical(g7,g0)
    c: Horizontal(g7,g4)
    c: Vertical(g4,g2)
    c: DistanceX(g1) = -30
    c: DistanceY(g1) = -30
    c: DistanceY(g0) = -5
    c: DistanceX(g0) = -5
    c: DistanceY(g1,g6) = 335
    c: DistanceY(g0,g7) = 285
    c: DistanceX(g0,g2) = 285
    c: DistanceX(g1,g3) = 335
    c: Equal(g6,g7)
    c: Equal(g6,g4)
    c: Equal(g6,g5)
    c: Equal(g6,g2)
    c: Equal(g6,g3)
    c: Equal(g6,g1)
    c: Equal(g6,g0)
    c: Diameter(g6) = 13
FEATURE [Part::Extrusion] Extrude061
  Base = -> Sketch136
  Dir = (0,0,1)
  DirMode = 2
  FaceMakerClass = Part::FaceMakerBullseye
  LengthFwd = 7.5
  LengthRev = 0
  Solid = true
  Symmetric = false
FEATURE [Sketcher::SketchObject] Sketch137  label="magnetHeatsetHoldCuts004"
  FullyConstrained = true
  Placement = pos=(0,0,-75) rot=(0,0,1;0rad)
  sketch-geometry (8):
    g0: Circle CenterX=-5 CenterY=-5 CenterZ=0 NormalX=0 NormalY=0 NormalZ=1 AngleXU=0 Radius=2
    g1: Circle CenterX=-30 CenterY=-30 CenterZ=0 NormalX=0 NormalY=0 NormalZ=1 AngleXU=0 Radius=2
    g2: Circle CenterX=280 CenterY=-5 CenterZ=0 NormalX=0 NormalY=0 NormalZ=1 AngleXU=0 Radius=2
    g3: Circle CenterX=305 CenterY=-30 CenterZ=0 NormalX=0 NormalY=0 NormalZ=1 AngleXU=0 Radius=2
    g4: Circle CenterX=280 CenterY=280 CenterZ=0 NormalX=0 NormalY=0 NormalZ=1 AngleXU=0 Radius=2
    g5: Circle CenterX=305 CenterY=305 CenterZ=0 NormalX=0 NormalY=0 NormalZ=1 AngleXU=0 Radius=2
    g6: Circle CenterX=-30 CenterY=305 CenterZ=0 NormalX=0 NormalY=0 NormalZ=1 AngleXU=0 Radius=2
    g7: Circle CenterX=-5 CenterY=280 CenterZ=0 NormalX=0 NormalY=0 NormalZ=1 AngleXU=0 Radius=2
  constraints (24):
    c: Horizontal(g1,g3)
    c: Vertical(g1,g6)
    c: Horizontal(g6,g5)
    c: Vertical(g3,g5)
    c: Horizontal(g0,g2)
    c: Vertical(g7,g0)
    c: Horizontal(g7,g4)
    c: Vertical(g4,g2)
    c: DistanceX(g1) = -30
    c: DistanceY(g1) = -30
    c: DistanceY(g0) = -5
    c: DistanceX(g0) = -5
    c: DistanceY(g1,g6) = 335
    c: DistanceY(g0,g7) = 285
    c: DistanceX(g0,g2) = 285
    c: DistanceX(g1,g3) = 335
    c: Equal(g6,g7)
    c: Equal(g6,g4)
    c: Equal(g6,g5)
    c: Equal(g6,g2)
    c: Equal(g6,g3)
    c: Equal(g6,g1)
    c: Equal(g6,g0)
    c: Diameter(g6) = 4
FEATURE [Part::Extrusion] Extrude062
  Base = -> Sketch137
  Dir = (0,0,1)
  DirMode = 2
  FaceMakerClass = Part::FaceMakerBullseye
  LengthFwd = 20
  LengthRev = 0
  Solid = true
  Symmetric = false
FEATURE [Part::MultiFuse] Fusion102  label="legCuts010"
  Shapes = -> [Extrude061,Extrude062]
FEATURE [Part::MultiFuse] Fusion103  label="legCuts011"
  Shapes = -> [Extrude060,Fusion102]
FEATURE [Part::Cut] Cut019  label="legs"
  Base = -> Common014
  Tool = -> Fusion097
FEATURE [Part::Cut] Cut020  label="legs005"
  Base = -> Common015
  Tool = -> Fusion099
FEATURE [Part::Cut] Cut021  label="legs006"
  Base = -> Common016
  Tool = -> Fusion101
FEATURE [Part::Cut] Cut022  label="legs007"
  Base = -> Common017
  Tool = -> Fusion103
FEATURE [Part::Fillet] Fillet
  Base = -> Cut017
  Edges = 10 edges r=2: [Edge157,Edge158,Edge159,Edge160,Edge165,Edge166,Edge203,Edge286,Edge340,Edge411]
FEATURE [Part::Fillet] Fillet001
  Base = -> Fillet
  Edges = 6 edges r=1: [Edge6,Edge10,Edge11,Edge12,Edge13,Edge16]
FEATURE [Part::Fillet] Fillet002  label="level2s003"
  Base = -> Fillet001
  Edges = 1 edges r=2: [Edge334]
FEATURE [Part::Fillet] Fillet003  label="legs008"
  Base = -> Cut019
  Edges = 1 edges r=10: [Edge9]
FEATURE [Part::Fillet] Fillet004  label="legs009"
  Base = -> Cut022
  Edges = 1 edges r=10: [Edge13]
FEATURE [Part::Fillet] Fillet005  label="legs010"
  Base = -> Cut021
  Edges = 1 edges r=10: [Edge7]
FEATURE [Part::Fillet] Fillet006  label="legs011"
  Base = -> Cut020
  Edges = 1 edges r=10: [Edge13]
FEATURE [Part::Fillet] Fillet007
  Base = -> Fillet002
  Edges = 1 edges r=2: [Edge233]
FEATURE [Part::Fillet] Fillet008  label="level2s004"
  Base = -> Fillet007
  Edges = 1 edges r=10: [Edge10]
FEATURE [Part::Fillet] Fillet009
  Base = -> Cut003
  Edges = 12 edges r=5: [Edge64,Edge67,Edge69,Edge70,Edge72,Edge75,Edge77,Edge78,Edge81,Edge82,Edge85,Edge86]
FEATURE [Part::Fillet] Fillet010  label="level1s"
  Base = -> Fillet009
  Edges = 4 edges r=10: [Edge199,Edge204,Edge212,Edge220]
FEATURE [Part::Fillet] Fillet011  label="topLid002"
  Base = -> Fusion083
  Edges = 4 edges r=1: [Edge1170,Edge1338,Edge1461,Edge1559]
FEATURE [Part::Fillet] Fillet012  label="topLid003"
  Base = -> Fillet011
  Edges = 4 edges r=3: [Edge327,Edge328,Edge651,Edge658]
FEATURE [Part::Fillet] Fillet013
  Base = -> Cut018
  Edges = 5 edges r=1.5: [Edge37,Edge41,Edge45,Edge48,Edge51]
FEATURE [Part::Fillet] Fillet014  label="bottomCover"
  Base = -> Fillet013
  Edges = 4 edges r=5: [Edge1,Edge3,Edge13,Edge31]
FEATURE [Part::Fillet] Fillet015  label="level1s001"
  Base = -> Fillet010
  Edges = 4 edges r=3: [Edge184,Edge185,Edge187,Edge189]
FEATURE [Part::Fillet] Fillet016  label="level002"
  Base = -> Fillet008
  Edges = 4 edges r=5: [Edge196,Edge197,Edge199,Edge201]
FEATURE [Part::Fillet] Fillet017
  Base = -> Fillet012
  Edges = 2 edges r=3: [Edge1266,Edge1267]
FEATURE [Part::Fillet] Fillet018
  Base = -> Fillet017
  Edges = 2 edges r=5: [Edge93,Edge256]
FEATURE [Part::Fillet] Fillet019
  Base = -> Fillet018
  Edges = 1 edges r=2: [Edge314]
FEATURE [Part::Fillet] Fillet020
  Base = -> Fillet019
  Edges = 2 edges r=1: [Edge8,Edge73]
FEATURE [Part::Fillet] Fillet021
  Base = -> Fillet020
  Edges = 1 edges r=3: [Edge74]
FEATURE [Part::Fillet] Fillet022
  Base = -> Fillet021
  Edges = 1 edges r=2: [Edge104]
